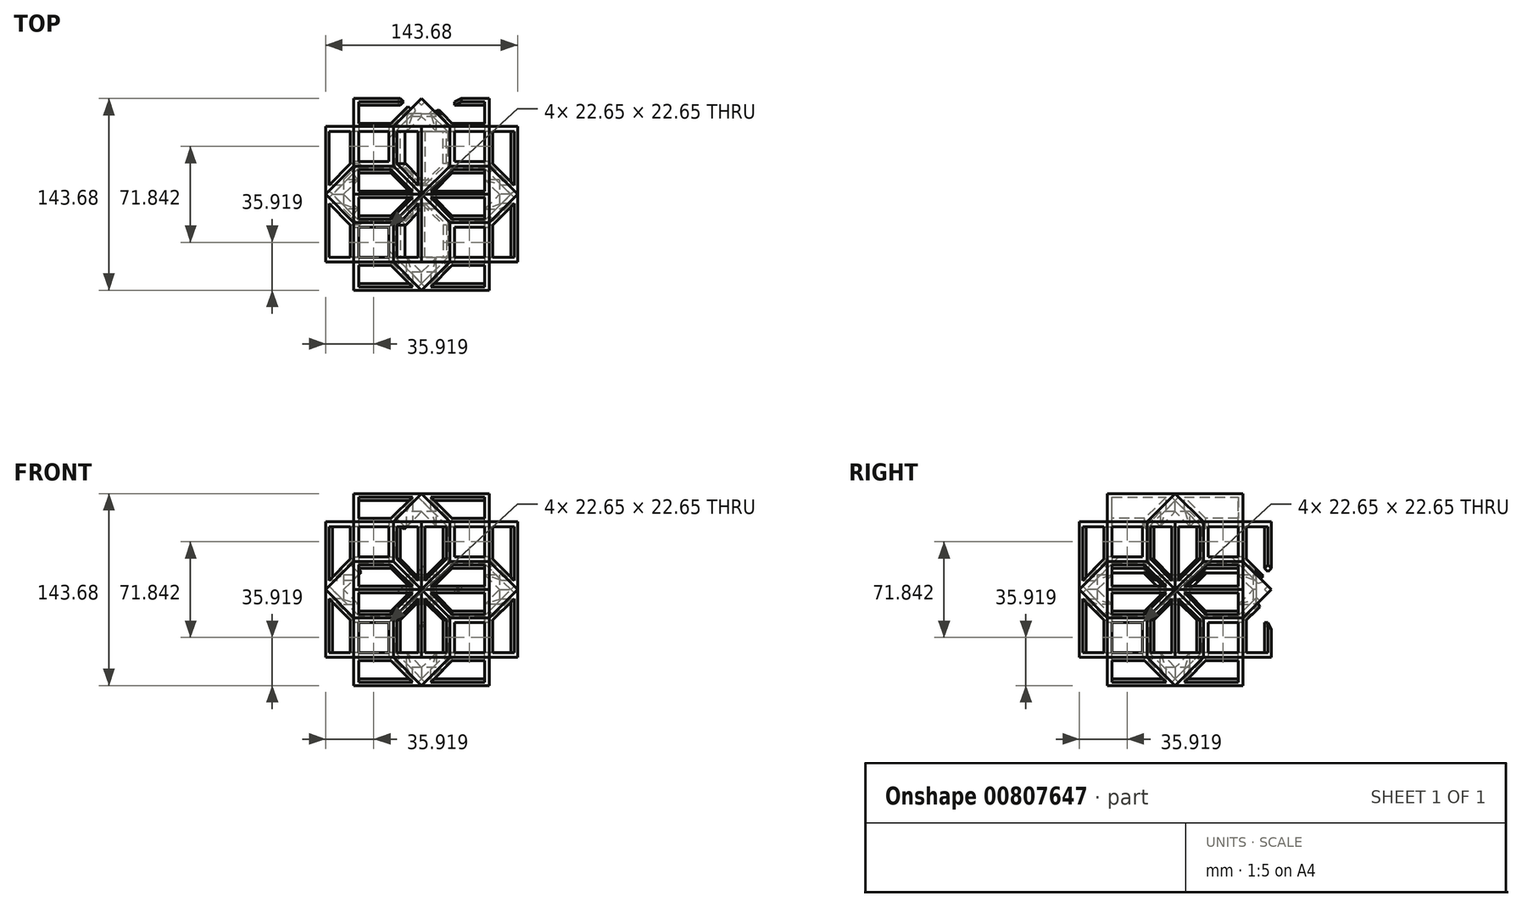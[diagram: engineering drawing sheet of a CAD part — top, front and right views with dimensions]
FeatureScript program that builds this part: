
annotation { "Feature Type Name" : "Feature", "Feature Type Description" : "" }
export const myFeature = defineFeature(function(context is Context, id is Id, definition is map)
    precondition{}
    {
        {
            var Q0;
            Q0=qCreatedBy(makeId("Top.planeOp"),FACE);
            var sketch = newSketch(context, id + "F0", { "sketchPlane" : qUnion([Q0])});
            skLineSegment(sketch, "E0.bottom", {"start": v(50.8, 50.8) * mm, "end": v(-50.8, 50.8) * mm});
            skLineSegment(sketch, "E0.top", {"start": v(50.8, -50.8) * mm, "end": v(-50.8, -50.8) * mm});
            skLineSegment(sketch, "E0.left", {"start": v(50.8, 50.8) * mm, "end": v(50.8, -50.8) * mm});
            skLineSegment(sketch, "E0.right", {"start": v(-50.8, 50.8) * mm, "end": v(-50.8, -50.8) * mm});
            skPoint(sketch, "E0.middle", {"position": v(0, 0) * mm});
            skLineSegment(sketch, "E1", {"start": v(-50.8, 50.8) * mm, "end": v(50.8, -50.8) * mm, "construction": true});
            skLineSegment(sketch, "E2", {"start": v(50.8, 50.8) * mm, "end": v(-50.8, -50.8) * mm, "construction": true});
            skLineSegment(sketch, "E3", {"start": v(0, 0) * mm, "end": v(-50.8, 0) * mm, "construction": true});
            skLineSegment(sketch, "E4", {"start": v(0, 0) * mm, "end": v(0, 50.8) * mm, "construction": true});
            skLineSegment(sketch, "E5.bottom", {"start": v(0, 71.84) * mm, "end": v(71.84, 0) * mm});
            skLineSegment(sketch, "E5.top", {"start": v(-71.84, 0) * mm, "end": v(0, -71.84) * mm});
            skLineSegment(sketch, "E5.left", {"start": v(0, 71.84) * mm, "end": v(-71.84, 0) * mm});
            skLineSegment(sketch, "E5.right", {"start": v(71.84, 0) * mm, "end": v(0, -71.84) * mm});
            skSolve(sketch);
        }
        {
            var Q0;
            {var subQ0=sQuery(id+"F0.wireOp",EDGE,"E0.right");var subQ1=sQuery(id+"F0.wireOp",EDGE,"E0.bottom");var subQ2=makeQuery(id+"F0.imprint","INTERSECT",VERTEX,{"derivedFrom":[subQ1,subQ0]});Q0=makeQuery(id+"F0.imprint","IMPRINT",FACE,{"disambiguationData":[TD([[makeQuery(id+"F0.imprint","IMPRINT",EDGE,{"disambiguationData":[TD([[subQ2,1.0]])],"derivedFrom":subQ1}),1.0]])]});}
            var Q1;
            {var subQ0=sQuery(id+"F0.wireOp",EDGE,"E5.left");var subQ1=sQuery(id+"F0.wireOp",EDGE,"E0.right");var subQ2=makeQuery(id+"F0.imprint","INTERSECT",VERTEX,{"derivedFrom":[subQ1,subQ0]});Q1=makeQuery(id+"F0.imprint","IMPRINT",FACE,{"disambiguationData":[TD([[makeQuery(id+"F0.imprint","IMPRINT",EDGE,{"disambiguationData":[TD([[subQ2,-1.0]])],"derivedFrom":subQ1}),-1.0]])]});}
            var Q2;
            {var subQ0=sQuery(id+"F0.wireOp",EDGE,"E0.right");var subQ1=sQuery(id+"F0.wireOp",EDGE,"E0.top");var subQ2=makeQuery(id+"F0.imprint","INTERSECT",VERTEX,{"derivedFrom":[subQ1,subQ0]});Q2=makeQuery(id+"F0.imprint","IMPRINT",FACE,{"disambiguationData":[TD([[makeQuery(id+"F0.imprint","IMPRINT",EDGE,{"disambiguationData":[TD([[subQ2,1.0]])],"derivedFrom":subQ1}),-1.0]])]});}
            var Q3;
            {var subQ0=sQuery(id+"F0.wireOp",EDGE,"E5.right");var subQ1=sQuery(id+"F0.wireOp",EDGE,"E0.top");var subQ2=makeQuery(id+"F0.imprint","INTERSECT",VERTEX,{"derivedFrom":[subQ1,subQ0]});Q3=makeQuery(id+"F0.imprint","IMPRINT",FACE,{"disambiguationData":[TD([[makeQuery(id+"F0.imprint","IMPRINT",EDGE,{"disambiguationData":[TD([[subQ2,-1.0]])],"derivedFrom":subQ1}),1.0]])]});}
            var Q4;
            {var subQ0=sQuery(id+"F0.wireOp",EDGE,"E0.left");var subQ1=sQuery(id+"F0.wireOp",EDGE,"E0.top");var subQ2=makeQuery(id+"F0.imprint","INTERSECT",VERTEX,{"derivedFrom":[subQ1,subQ0]});Q4=makeQuery(id+"F0.imprint","IMPRINT",FACE,{"disambiguationData":[TD([[makeQuery(id+"F0.imprint","IMPRINT",EDGE,{"disambiguationData":[TD([[subQ2,-1.0]])],"derivedFrom":subQ1}),-1.0]])]});}
            var Q5;
            {var subQ0=sQuery(id+"F0.wireOp",EDGE,"E0.left");var subQ1=sQuery(id+"F0.wireOp",EDGE,"E0.bottom");var subQ2=makeQuery(id+"F0.imprint","INTERSECT",VERTEX,{"derivedFrom":[subQ1,subQ0]});Q5=makeQuery(id+"F0.imprint","IMPRINT",FACE,{"disambiguationData":[TD([[makeQuery(id+"F0.imprint","IMPRINT",EDGE,{"disambiguationData":[TD([[subQ2,-1.0]])],"derivedFrom":subQ1}),1.0]])]});}
            var Q6;
            {var subQ0=sQuery(id+"F0.wireOp",EDGE,"E5.bottom");var subQ1=sQuery(id+"F0.wireOp",EDGE,"E0.left");var subQ2=makeQuery(id+"F0.imprint","INTERSECT",VERTEX,{"derivedFrom":[subQ1,subQ0]});Q6=makeQuery(id+"F0.imprint","IMPRINT",FACE,{"disambiguationData":[TD([[makeQuery(id+"F0.imprint","IMPRINT",EDGE,{"disambiguationData":[TD([[subQ2,-1.0]])],"derivedFrom":subQ1}),1.0]])]});}
            var Q7;
            {var subQ0=sQuery(id+"F0.wireOp",EDGE,"E5.bottom");var subQ1=sQuery(id+"F0.wireOp",EDGE,"E0.bottom");var subQ2=makeQuery(id+"F0.imprint","INTERSECT",VERTEX,{"derivedFrom":[subQ1,subQ0]});Q7=makeQuery(id+"F0.imprint","IMPRINT",FACE,{"disambiguationData":[TD([[makeQuery(id+"F0.imprint","IMPRINT",EDGE,{"disambiguationData":[TD([[subQ2,-1.0]])],"derivedFrom":subQ1}),-1.0]])]});}
            var Q8;
            {var subQ5=sQuery(id+"F0.wireOp",EDGE,"E5.bottom");var subQ13=sQuery(id+"F0.wireOp",EDGE,"E0.bottom");var subQ14=makeQuery(id+"F0.imprint","INTERSECT",VERTEX,{"derivedFrom":[subQ13,subQ5]});Q8=makeQuery(id+"F0.imprint","IMPRINT",FACE,{"disambiguationData":[TD([[makeQuery(id+"F0.imprint","IMPRINT",EDGE,{"disambiguationData":[TD([[subQ14,-1.0]])],"derivedFrom":subQ13}),1.0]])]});}
            extrude(context, id + "F1", {"entities" : qUnion([Q0, Q1, Q2, Q3, Q4, Q5, Q6, Q7, Q8]), "depth" : 101.6 * mm, "offsetDistance" : 25.4 * mm});
        }
        {
            var Q0;
            {var subQ0=sQuery(id+"F0.wireOp",EDGE,"E0.top");Q0=makeQuery(id+"F1.opExtrude","SWEPT_FACE",FACE,{"disambiguationData":[OSD([subQ0]),TDD([makeQuery(id+"F0.imprint","IMPRINT",EDGE,{"disambiguationData":[TD([[makeQuery(id+"F0.imprint","INTERSECT",VERTEX,{"derivedFrom":[subQ0,sQuery(id+"F0.wireOp",EDGE,"E0.right")]}),1.0]])],"derivedFrom":subQ0})])]});}
            var sketch = newSketch(context, id + "F2", { "sketchPlane" : qUnion([Q0])});
            skLineSegment(sketch, "E6.bottom", {"start": v(0, 122.64) * mm, "end": v(71.84, 50.8) * mm});
            skLineSegment(sketch, "E6.top", {"start": v(-71.84, 50.8) * mm, "end": v(0, -21.04) * mm});
            skLineSegment(sketch, "E6.left", {"start": v(0, 122.64) * mm, "end": v(-71.84, 50.8) * mm});
            skLineSegment(sketch, "E6.right", {"start": v(71.84, 50.8) * mm, "end": v(0, -21.04) * mm});
            skLineSegment(sketch, "E7", {"start": v(-50.8, 101.6) * mm, "end": v(50.8, 0) * mm, "construction": true});
            skLineSegment(sketch, "E8", {"start": v(50.8, 101.6) * mm, "end": v(-50.8, 0) * mm, "construction": true});
            skLineSegment(sketch, "E9", {"start": v(0, 50.8) * mm, "end": v(-50.8, 50.8) * mm, "construction": true});
            skLineSegment(sketch, "E10", {"start": v(0, 50.8) * mm, "end": v(0, 101.6) * mm, "construction": true});
            skSolve(sketch);
        }
        {
            var Q0;
            {var subQ6=sQuery(id+"F2.wireOp",EDGE,"E6.bottom");Q0=makeQuery(id+"F2.imprint","IMPRINT",FACE,{"disambiguationData":[TD([[makeQuery(id+"F2.imprint","IMPRINT",EDGE,{"derivedFrom":subQ6}),-1.0]])]});}
            var Q1;
            {var subQ0=sQuery(id+"F2.wireOp",EDGE,"E6.left");var subQ1=sQuery(id+"F2.wireOp",EDGE,"E6.top");var subQ2=makeQuery(id+"F2.imprint","INTERSECT",VERTEX,{"derivedFrom":[subQ1,subQ0]});Q1=makeQuery(id+"F2.imprint","IMPRINT",FACE,{"disambiguationData":[TD([[makeQuery(id+"F2.imprint","IMPRINT",EDGE,{"disambiguationData":[TD([[subQ2,-1.0]])],"derivedFrom":subQ1}),1.0]])]});}
            extrude(context, id + "F3", {"entities" : qUnion([Q0, Q1]), "operationType" : NewBodyOperationType.ADD, "oppositeDirection" : true, "depth" : 101.6 * mm, "offsetDistance" : 25.4 * mm});
        }
        {
            var Q0;
            {var subQ2=sQuery(id+"F0.wireOp",EDGE,"E0.right");var subQ4=sQuery(id+"F2.wireOp",EDGE,"E6.left");var subQ5=sQuery(id+"F2.wireOp",EDGE,"E6.top");var subQ7=sQuery(id+"F0.wireOp",EDGE,"E0.bottom");var subQ8=makeQuery(id+"F0.imprint","INTERSECT",VERTEX,{"derivedFrom":[subQ7,subQ2]});Q0=makeQuery(id+"F3.boolean.opBoolean","SPLIT",FACE,{"disambiguationData":[TD([makeQuery(id+"F3.opExtrude","SWEPT_FACE",FACE,{"disambiguationData":[OSD([subQ5]),TDD([makeQuery(id+"F2.imprint","IMPRINT",EDGE,{"disambiguationData":[TD([[makeQuery(id+"F2.imprint","INTERSECT",VERTEX,{"derivedFrom":[subQ5,subQ4]}),-1.0]])],"derivedFrom":subQ5})])]})])],"derivedFrom":makeQuery(id+"F1.opExtrude","SWEPT_FACE",FACE,{"disambiguationData":[OSD([subQ2]),TDD([makeQuery(id+"F0.imprint","IMPRINT",EDGE,{"disambiguationData":[TD([[subQ8,-1.0]])],"derivedFrom":subQ2})])]})});}
            var sketch = newSketch(context, id + "F4", { "sketchPlane" : qUnion([Q0])});
            skLineSegment(sketch, "E11.bottom", {"start": v(-71.84, 50.8) * mm, "end": v(0, -21.04) * mm});
            skLineSegment(sketch, "E11.top", {"start": v(0, 122.64) * mm, "end": v(71.84, 50.8) * mm});
            skLineSegment(sketch, "E11.left", {"start": v(-71.84, 50.8) * mm, "end": v(0, 122.64) * mm});
            skLineSegment(sketch, "E11.right", {"start": v(0, -21.04) * mm, "end": v(71.84, 50.8) * mm});
            skLineSegment(sketch, "E12", {"start": v(-50.8, 101.6) * mm, "end": v(50.8, 0) * mm, "construction": true});
            skLineSegment(sketch, "E13", {"start": v(50.8, 101.6) * mm, "end": v(-50.8, 0) * mm, "construction": true});
            skLineSegment(sketch, "E14", {"start": v(0, 50.8) * mm, "end": v(-50.8, 50.8) * mm, "construction": true});
            skLineSegment(sketch, "E15", {"start": v(0, 50.8) * mm, "end": v(0, 101.6) * mm, "construction": true});
            skSolve(sketch);
        }
        {
            var Q0;
            Q0=makeQuery(id+"F4.imprint","IMPRINT",FACE,{"disambiguationData":[TD([[makeQuery(id+"F4.imprint","IMPRINT",EDGE,{"derivedFrom":sQuery(id+"F4.wireOp",EDGE,"E11.top")}),-1.0]])]});
            extrude(context, id + "F5", {"entities" : qUnion([Q0]), "operationType" : NewBodyOperationType.ADD, "oppositeDirection" : true, "depth" : 101.6 * mm, "offsetDistance" : 25.4 * mm});
        }
        {
            var Q0;
            {var subQ0=sQuery(id+"F2.wireOp",EDGE,"E6.right");var subQ2=sQuery(id+"F0.wireOp",EDGE,"E0.top");var subQ3=sQuery(id+"F0.wireOp",EDGE,"E0.left");var subQ4=makeQuery(id+"F0.imprint","INTERSECT",VERTEX,{"derivedFrom":[subQ2,subQ3]});Q0=makeQuery(id+"F3.boolean.opBoolean","SPLIT",FACE,{"disambiguationData":[TD([makeQuery(id+"F3.opExtrude","SWEPT_FACE",FACE,{"disambiguationData":[OSD([subQ0])]})])],"derivedFrom":makeQuery(id+"F1.opExtrude","SWEPT_FACE",FACE,{"disambiguationData":[OSD([subQ3]),TDD([makeQuery(id+"F0.imprint","IMPRINT",EDGE,{"disambiguationData":[TD([[subQ4,1.0]])],"derivedFrom":subQ3})])]})});}
            var sketch = newSketch(context, id + "F6", { "sketchPlane" : qUnion([Q0])});
            skLineSegment(sketch, "E16.bottom", {"start": v(-50.8, 29.76) * mm, "end": v(-21.04, 29.76) * mm});
            skLineSegment(sketch, "E16.top", {"start": v(-50.8, 0) * mm, "end": v(-21.04, 0) * mm});
            skLineSegment(sketch, "E16.left", {"start": v(-50.8, 29.76) * mm, "end": v(-50.8, 0) * mm});
            skLineSegment(sketch, "E16.right", {"start": v(-21.04, 29.76) * mm, "end": v(-21.04, 0) * mm});
            skLineSegment(sketch, "E17.0", {"start": v(-24.6, 26.2) * mm, "end": v(-24.6, 3.56) * mm});
            skLineSegment(sketch, "E17.1", {"start": v(-47.24, 26.2) * mm, "end": v(-24.6, 26.2) * mm});
            skLineSegment(sketch, "E17.2", {"start": v(-47.24, 26.2) * mm, "end": v(-47.24, 3.56) * mm});
            skLineSegment(sketch, "E17.3", {"start": v(-47.24, 3.56) * mm, "end": v(-24.6, 3.56) * mm});
            skSolve(sketch);
        }
        {
            var Q0;
            Q0=makeQuery(id+"F6.imprint","IMPRINT",FACE,{"disambiguationData":[TD([[makeQuery(id+"F6.imprint","IMPRINT",EDGE,{"derivedFrom":sQuery(id+"F6.wireOp",EDGE,"E17.0")}),-1.0]])]});
            extrude(context, id + "F7", {"entities" : qUnion([Q0]), "operationType" : NewBodyOperationType.ADD, "oppositeDirection" : true, "depth" : 5.08 * mm, "offsetDistance" : 25.4 * mm});
        }
        {
            var Q0;
            {var subQ2=sQuery(id+"F0.wireOp",EDGE,"E0.right");var subQ4=sQuery(id+"F2.wireOp",EDGE,"E6.left");var subQ5=sQuery(id+"F2.wireOp",EDGE,"E6.top");var subQ7=sQuery(id+"F0.wireOp",EDGE,"E0.bottom");var subQ8=makeQuery(id+"F0.imprint","INTERSECT",VERTEX,{"derivedFrom":[subQ7,subQ2]});Q0=makeQuery(id+"F3.boolean.opBoolean","SPLIT",FACE,{"disambiguationData":[TD([makeQuery(id+"F3.opExtrude","SWEPT_FACE",FACE,{"disambiguationData":[OSD([subQ4]),TDD([makeQuery(id+"F2.imprint","IMPRINT",EDGE,{"disambiguationData":[TD([[makeQuery(id+"F2.imprint","INTERSECT",VERTEX,{"derivedFrom":[subQ5,subQ4]}),1.0]])],"derivedFrom":subQ4})])]})])],"derivedFrom":makeQuery(id+"F1.opExtrude","SWEPT_FACE",FACE,{"disambiguationData":[OSD([subQ2]),TDD([makeQuery(id+"F0.imprint","IMPRINT",EDGE,{"disambiguationData":[TD([[subQ8,-1.0]])],"derivedFrom":subQ2})])]})});}
            var Q1;
            {var subQ0=sQuery(id+"F0.wireOp",EDGE,"E0.right");var subQ1=sQuery(id+"F0.wireOp",EDGE,"E0.top");var subQ2=makeQuery(id+"F0.imprint","INTERSECT",VERTEX,{"derivedFrom":[subQ1,subQ0]});var subQ4=sQuery(id+"F2.wireOp",EDGE,"E6.left");var subQ5=sQuery(id+"F2.wireOp",EDGE,"E6.top");Q1=makeQuery(id+"F3.boolean.opBoolean","SPLIT",FACE,{"disambiguationData":[TD([makeQuery(id+"F3.opExtrude","SWEPT_FACE",FACE,{"disambiguationData":[OSD([subQ4]),TDD([makeQuery(id+"F2.imprint","IMPRINT",EDGE,{"disambiguationData":[TD([[makeQuery(id+"F2.imprint","INTERSECT",VERTEX,{"derivedFrom":[subQ5,subQ4]}),1.0]])],"derivedFrom":subQ4})])]})])],"derivedFrom":makeQuery(id+"F1.opExtrude","SWEPT_FACE",FACE,{"disambiguationData":[OSD([subQ0]),TDD([makeQuery(id+"F0.imprint","IMPRINT",EDGE,{"disambiguationData":[TD([[subQ2,1.0]])],"derivedFrom":subQ0})])]})});}
            var Q2;
            {var subQ0=sQuery(id+"F0.wireOp",EDGE,"E5.left");var subQ1=sQuery(id+"F0.wireOp",EDGE,"E5.top");var subQ2=makeQuery(id+"F0.imprint","INTERSECT",VERTEX,{"derivedFrom":[subQ1,subQ0]});var subQ3=sQuery(id+"F0.wireOp",EDGE,"E0.right");var subQ5=makeQuery(id+"F1.opExtrude","SWEPT_FACE",FACE,{"disambiguationData":[OSD([subQ0]),TDD([makeQuery(id+"F0.imprint","IMPRINT",EDGE,{"disambiguationData":[TD([[subQ2,1.0]])],"derivedFrom":subQ0})])]});var subQ9=sQuery(id+"F0.wireOp",EDGE,"E0.top");var subQ11=sQuery(id+"F0.wireOp",EDGE,"E0.bottom");Q2=makeQuery(id+"F3.boolean.opBoolean","SPLIT",FACE,{"disambiguationData":[TD([makeQuery(id+"F1.opExtrude","CAP_FACE",FACE,{"disambiguationData":[OSD([subQ11,subQ9,sQuery(id+"F0.wireOp",EDGE,"E0.left"),subQ3,sQuery(id+"F0.wireOp",EDGE,"E5.bottom"),subQ1,subQ0,sQuery(id+"F0.wireOp",EDGE,"E5.right")])],"isStart":true})])],"derivedFrom":subQ5});}
            var Q3;
            {var subQ0=sQuery(id+"F0.wireOp",EDGE,"E5.left");var subQ1=sQuery(id+"F0.wireOp",EDGE,"E5.top");var subQ2=makeQuery(id+"F0.imprint","INTERSECT",VERTEX,{"derivedFrom":[subQ1,subQ0]});var subQ3=sQuery(id+"F0.wireOp",EDGE,"E0.right");var subQ7=sQuery(id+"F0.wireOp",EDGE,"E0.top");var subQ10=makeQuery(id+"F1.opExtrude","SWEPT_FACE",FACE,{"disambiguationData":[OSD([subQ1]),TDD([makeQuery(id+"F0.imprint","IMPRINT",EDGE,{"disambiguationData":[TD([[subQ2,-1.0]])],"derivedFrom":subQ1})])]});Q3=makeQuery(id+"F3.boolean.opBoolean","SPLIT",FACE,{"disambiguationData":[TD([makeQuery(id+"F1.opExtrude","CAP_FACE",FACE,{"disambiguationData":[OSD([sQuery(id+"F0.wireOp",EDGE,"E0.bottom"),subQ7,sQuery(id+"F0.wireOp",EDGE,"E0.left"),subQ3,sQuery(id+"F0.wireOp",EDGE,"E5.bottom"),subQ1,subQ0,sQuery(id+"F0.wireOp",EDGE,"E5.right")])],"isStart":false})])],"derivedFrom":subQ10});}
            var Q4;
            {var subQ0=sQuery(id+"F0.wireOp",EDGE,"E5.right");var subQ1=sQuery(id+"F0.wireOp",EDGE,"E5.top");var subQ2=makeQuery(id+"F0.imprint","INTERSECT",VERTEX,{"derivedFrom":[subQ1,subQ0]});var subQ3=sQuery(id+"F0.wireOp",EDGE,"E0.top");var subQ5=sQuery(id+"F2.wireOp",EDGE,"E6.right");var subQ6=sQuery(id+"F2.wireOp",EDGE,"E6.left");var subQ7=sQuery(id+"F2.wireOp",EDGE,"E6.top");var subQ8=sQuery(id+"F0.wireOp",EDGE,"E0.right");var subQ9=makeQuery(id+"F0.imprint","IMPRINT",EDGE,{"disambiguationData":[TD([[makeQuery(id+"F0.imprint","INTERSECT",VERTEX,{"derivedFrom":[subQ3,subQ8]}),1.0]])],"derivedFrom":subQ3});var subQ10=sQuery(id+"F0.wireOp",EDGE,"E0.left");var subQ12=makeQuery(id+"F1.opExtrude","CAP_FACE",FACE,{"disambiguationData":[OSD([sQuery(id+"F0.wireOp",EDGE,"E0.bottom"),subQ3,subQ10,subQ8,sQuery(id+"F0.wireOp",EDGE,"E5.bottom"),subQ1,sQuery(id+"F0.wireOp",EDGE,"E5.left"),subQ0])],"isStart":true});Q4=makeQuery(id+"F3.boolean.opBoolean","SPLIT",FACE,{"disambiguationData":[TD([subQ12,makeQuery(id+"F1.opExtrude","SWEPT_FACE",FACE,{"disambiguationData":[OSD([subQ3]),TDD([makeQuery(id+"F0.imprint","IMPRINT",EDGE,{"disambiguationData":[TD([[makeQuery(id+"F0.imprint","INTERSECT",VERTEX,{"derivedFrom":[subQ3,subQ10]}),-1.0]])],"derivedFrom":subQ3})])]}),makeQuery(id+"F1.opExtrude","SWEPT_FACE",FACE,{"disambiguationData":[OSD([subQ3]),TDD([subQ9])]}),makeQuery(id+"F1.opExtrude","SWEPT_FACE",FACE,{"disambiguationData":[OSD([subQ1]),TDD([makeQuery(id+"F0.imprint","IMPRINT",EDGE,{"disambiguationData":[TD([[subQ2,1.0]])],"derivedFrom":subQ1})])]}),makeQuery(id+"F1.opExtrude","SWEPT_FACE",FACE,{"disambiguationData":[OSD([subQ0]),TDD([makeQuery(id+"F0.imprint","IMPRINT",EDGE,{"disambiguationData":[TD([[subQ2,1.0]])],"derivedFrom":subQ0})])]}),makeQuery(id+"F3.opExtrude","CAP_FACE",FACE,{"disambiguationData":[OSD([subQ3,subQ1,sQuery(id+"F2.wireOp",EDGE,"E6.bottom"),subQ7,subQ6,subQ5])],"isStart":true}),makeQuery(id+"F3.opExtrude","CAP_FACE",FACE,{"disambiguationData":[OSD([subQ3,subQ8,subQ7,subQ6])],"isStart":true}),makeQuery(id+"F3.opExtrude","SWEPT_FACE",FACE,{"disambiguationData":[OSD([subQ7]),TDD([makeQuery(id+"F2.imprint","IMPRINT",EDGE,{"disambiguationData":[TD([[makeQuery(id+"F2.imprint","INTERSECT",VERTEX,{"derivedFrom":[subQ7,subQ5]}),1.0]])],"derivedFrom":subQ7})])]}),makeQuery(id+"F3.opExtrude","SWEPT_FACE",FACE,{"disambiguationData":[OSD([subQ5])]})])],"derivedFrom":subQ12});}
            var Q5;
            {var subQ0=sQuery(id+"F2.wireOp",EDGE,"E6.right");var subQ2=sQuery(id+"F2.wireOp",EDGE,"E6.top");var subQ7=sQuery(id+"F0.wireOp",EDGE,"E0.bottom");var subQ9=sQuery(id+"F0.wireOp",EDGE,"E0.right");var subQ10=makeQuery(id+"F0.imprint","INTERSECT",VERTEX,{"derivedFrom":[subQ7,subQ9]});var subQ13=makeQuery(id+"F3.opExtrude","SWEPT_FACE",FACE,{"disambiguationData":[OSD([subQ2]),TDD([makeQuery(id+"F2.imprint","IMPRINT",EDGE,{"disambiguationData":[TD([[makeQuery(id+"F2.imprint","INTERSECT",VERTEX,{"derivedFrom":[subQ2,subQ0]}),1.0]])],"derivedFrom":subQ2})])]});Q5=makeQuery(id+"F5.boolean.opBoolean","SPLIT",FACE,{"disambiguationData":[TD([makeQuery(id+"F1.opExtrude","SWEPT_FACE",FACE,{"disambiguationData":[OSD([subQ7]),TDD([makeQuery(id+"F0.imprint","IMPRINT",EDGE,{"disambiguationData":[TD([[subQ10,1.0]])],"derivedFrom":subQ7})])]})])],"derivedFrom":subQ13});}
            var Q6;
            {var subQ0=sQuery(id+"F0.wireOp",EDGE,"E0.right");var subQ1=sQuery(id+"F0.wireOp",EDGE,"E0.bottom");var subQ2=sQuery(id+"F0.wireOp",EDGE,"E5.left");var subQ4=sQuery(id+"F0.wireOp",EDGE,"E5.bottom");var subQ5=makeQuery(id+"F0.imprint","INTERSECT",VERTEX,{"derivedFrom":[subQ4,subQ2]});var subQ6=sQuery(id+"F2.wireOp",EDGE,"E6.right");var subQ7=sQuery(id+"F2.wireOp",EDGE,"E6.left");var subQ8=sQuery(id+"F2.wireOp",EDGE,"E6.top");var subQ9=sQuery(id+"F0.wireOp",EDGE,"E5.top");var subQ10=sQuery(id+"F0.wireOp",EDGE,"E0.top");var subQ11=sQuery(id+"F0.wireOp",EDGE,"E0.left");var subQ12=makeQuery(id+"F1.opExtrude","CAP_FACE",FACE,{"disambiguationData":[OSD([subQ1,subQ10,subQ11,subQ0,subQ4,subQ9,subQ2,sQuery(id+"F0.wireOp",EDGE,"E5.right")])],"isStart":true});Q6=makeQuery(id+"F3.boolean.opBoolean","SPLIT",FACE,{"disambiguationData":[TD([makeQuery(id+"F1.opExtrude","SWEPT_FACE",FACE,{"disambiguationData":[OSD([subQ1]),TDD([makeQuery(id+"F0.imprint","IMPRINT",EDGE,{"disambiguationData":[TD([[makeQuery(id+"F0.imprint","INTERSECT",VERTEX,{"derivedFrom":[subQ1,subQ11]}),-1.0]])],"derivedFrom":subQ1})])]}),subQ12,makeQuery(id+"F1.opExtrude","SWEPT_FACE",FACE,{"disambiguationData":[OSD([subQ1]),TDD([makeQuery(id+"F0.imprint","IMPRINT",EDGE,{"disambiguationData":[TD([[makeQuery(id+"F0.imprint","INTERSECT",VERTEX,{"derivedFrom":[subQ1,subQ0]}),1.0]])],"derivedFrom":subQ1})])]}),makeQuery(id+"F1.opExtrude","SWEPT_FACE",FACE,{"disambiguationData":[OSD([subQ4]),TDD([makeQuery(id+"F0.imprint","IMPRINT",EDGE,{"disambiguationData":[TD([[subQ5,-1.0]])],"derivedFrom":subQ4})])]}),makeQuery(id+"F1.opExtrude","SWEPT_FACE",FACE,{"disambiguationData":[OSD([subQ2]),TDD([makeQuery(id+"F0.imprint","IMPRINT",EDGE,{"disambiguationData":[TD([[subQ5,-1.0]])],"derivedFrom":subQ2})])]}),makeQuery(id+"F3.opExtrude","CAP_FACE",FACE,{"disambiguationData":[OSD([subQ10,subQ9,sQuery(id+"F2.wireOp",EDGE,"E6.bottom"),subQ8,subQ7,subQ6])],"isStart":false}),makeQuery(id+"F3.opExtrude","CAP_FACE",FACE,{"disambiguationData":[OSD([subQ10,subQ0,subQ8,subQ7])],"isStart":false}),makeQuery(id+"F3.opExtrude","SWEPT_FACE",FACE,{"disambiguationData":[OSD([subQ8]),TDD([makeQuery(id+"F2.imprint","IMPRINT",EDGE,{"disambiguationData":[TD([[makeQuery(id+"F2.imprint","INTERSECT",VERTEX,{"derivedFrom":[subQ8,subQ6]}),1.0]])],"derivedFrom":subQ8})])]}),makeQuery(id+"F3.opExtrude","SWEPT_FACE",FACE,{"disambiguationData":[OSD([subQ6])]})])],"derivedFrom":subQ12});}
            var Q7;
            {var subQ0=sQuery(id+"F0.wireOp",EDGE,"E5.right");var subQ1=sQuery(id+"F0.wireOp",EDGE,"E5.top");var subQ2=makeQuery(id+"F0.imprint","INTERSECT",VERTEX,{"derivedFrom":[subQ1,subQ0]});var subQ5=sQuery(id+"F2.wireOp",EDGE,"E6.bottom");var subQ7=makeQuery(id+"F1.opExtrude","SWEPT_FACE",FACE,{"disambiguationData":[OSD([subQ0]),TDD([makeQuery(id+"F0.imprint","IMPRINT",EDGE,{"disambiguationData":[TD([[subQ2,1.0]])],"derivedFrom":subQ0})])]});Q7=makeQuery(id+"F5.boolean.opBoolean","SPLIT",FACE,{"disambiguationData":[TD([makeQuery(id+"F3.opExtrude","SWEPT_FACE",FACE,{"disambiguationData":[OSD([subQ5])]})])],"derivedFrom":subQ7});}
            var Q8;
            {var subQ0=sQuery(id+"F2.wireOp",EDGE,"E6.right");var subQ2=sQuery(id+"F2.wireOp",EDGE,"E6.top");var subQ4=sQuery(id+"F0.wireOp",EDGE,"E0.top");var subQ7=sQuery(id+"F0.wireOp",EDGE,"E0.right");var subQ8=makeQuery(id+"F0.imprint","IMPRINT",EDGE,{"disambiguationData":[TD([[makeQuery(id+"F0.imprint","INTERSECT",VERTEX,{"derivedFrom":[subQ4,subQ7]}),1.0]])],"derivedFrom":subQ4});var subQ13=makeQuery(id+"F3.opExtrude","SWEPT_FACE",FACE,{"disambiguationData":[OSD([subQ2]),TDD([makeQuery(id+"F2.imprint","IMPRINT",EDGE,{"disambiguationData":[TD([[makeQuery(id+"F2.imprint","INTERSECT",VERTEX,{"derivedFrom":[subQ2,subQ0]}),1.0]])],"derivedFrom":subQ2})])]});Q8=makeQuery(id+"F5.boolean.opBoolean","SPLIT",FACE,{"disambiguationData":[TD([makeQuery(id+"F1.opExtrude","SWEPT_FACE",FACE,{"disambiguationData":[OSD([subQ4]),TDD([subQ8])]})])],"derivedFrom":subQ13});}
            var Q9;
            {var subQ0=sQuery(id+"F2.wireOp",EDGE,"E6.right");var subQ2=sQuery(id+"F0.wireOp",EDGE,"E0.top");var subQ3=sQuery(id+"F0.wireOp",EDGE,"E0.left");var subQ4=makeQuery(id+"F0.imprint","INTERSECT",VERTEX,{"derivedFrom":[subQ2,subQ3]});Q9=makeQuery(id+"F3.boolean.opBoolean","SPLIT",FACE,{"disambiguationData":[TD([makeQuery(id+"F3.opExtrude","SWEPT_FACE",FACE,{"disambiguationData":[OSD([subQ0])]})])],"derivedFrom":makeQuery(id+"F1.opExtrude","SWEPT_FACE",FACE,{"disambiguationData":[OSD([subQ3]),TDD([makeQuery(id+"F0.imprint","IMPRINT",EDGE,{"disambiguationData":[TD([[subQ4,1.0]])],"derivedFrom":subQ3})])]})});}
            var Q10;
            {var subQ0=sQuery(id+"F0.wireOp",EDGE,"E5.right");var subQ1=sQuery(id+"F0.wireOp",EDGE,"E5.top");var subQ2=makeQuery(id+"F0.imprint","INTERSECT",VERTEX,{"derivedFrom":[subQ1,subQ0]});var subQ5=makeQuery(id+"F1.opExtrude","SWEPT_FACE",FACE,{"disambiguationData":[OSD([subQ1]),TDD([makeQuery(id+"F0.imprint","IMPRINT",EDGE,{"disambiguationData":[TD([[subQ2,1.0]])],"derivedFrom":subQ1})])]});var subQ6=sQuery(id+"F2.wireOp",EDGE,"E6.right");var subQ8=sQuery(id+"F2.wireOp",EDGE,"E6.top");Q10=makeQuery(id+"F5.boolean.opBoolean","SPLIT",FACE,{"disambiguationData":[TD([makeQuery(id+"F3.opExtrude","SWEPT_FACE",FACE,{"disambiguationData":[OSD([subQ8]),TDD([makeQuery(id+"F2.imprint","IMPRINT",EDGE,{"disambiguationData":[TD([[makeQuery(id+"F2.imprint","INTERSECT",VERTEX,{"derivedFrom":[subQ8,subQ6]}),1.0]])],"derivedFrom":subQ8})])]})])],"derivedFrom":subQ5});}
            var Q11;
            {var subQ3=sQuery(id+"F0.wireOp",EDGE,"E0.right");var subQ5=sQuery(id+"F0.wireOp",EDGE,"E0.top");var subQ6=makeQuery(id+"F0.imprint","INTERSECT",VERTEX,{"derivedFrom":[subQ5,subQ3]});var subQ7=sQuery(id+"F2.wireOp",EDGE,"E6.left");var subQ8=sQuery(id+"F2.wireOp",EDGE,"E6.top");var subQ9=makeQuery(id+"F2.imprint","INTERSECT",VERTEX,{"derivedFrom":[subQ8,subQ7]});var subQ11=makeQuery(id+"F3.opExtrude","SWEPT_FACE",FACE,{"disambiguationData":[OSD([subQ7]),TDD([makeQuery(id+"F2.imprint","IMPRINT",EDGE,{"disambiguationData":[TD([[subQ9,1.0]])],"derivedFrom":subQ7})])]});Q11=makeQuery(id+"F3.boolean.opBoolean","SPLIT",FACE,{"disambiguationData":[TD([makeQuery(id+"F1.opExtrude","SWEPT_FACE",FACE,{"disambiguationData":[OSD([subQ5]),TDD([makeQuery(id+"F0.imprint","IMPRINT",EDGE,{"disambiguationData":[TD([[subQ6,1.0]])],"derivedFrom":subQ5})])]})])],"derivedFrom":subQ11});}
            var Q12;
            {var subQ0=sQuery(id+"F0.wireOp",EDGE,"E5.left");var subQ1=sQuery(id+"F0.wireOp",EDGE,"E5.top");var subQ2=makeQuery(id+"F0.imprint","INTERSECT",VERTEX,{"derivedFrom":[subQ1,subQ0]});var subQ3=sQuery(id+"F0.wireOp",EDGE,"E0.right");var subQ7=sQuery(id+"F0.wireOp",EDGE,"E0.top");var subQ10=makeQuery(id+"F1.opExtrude","SWEPT_FACE",FACE,{"disambiguationData":[OSD([subQ1]),TDD([makeQuery(id+"F0.imprint","IMPRINT",EDGE,{"disambiguationData":[TD([[subQ2,-1.0]])],"derivedFrom":subQ1})])]});Q12=makeQuery(id+"F3.boolean.opBoolean","SPLIT",FACE,{"disambiguationData":[TD([makeQuery(id+"F1.opExtrude","CAP_FACE",FACE,{"disambiguationData":[OSD([sQuery(id+"F0.wireOp",EDGE,"E0.bottom"),subQ7,sQuery(id+"F0.wireOp",EDGE,"E0.left"),subQ3,sQuery(id+"F0.wireOp",EDGE,"E5.bottom"),subQ1,subQ0,sQuery(id+"F0.wireOp",EDGE,"E5.right")])],"isStart":true})])],"derivedFrom":subQ10});}
            var Q13;
            {var subQ2=sQuery(id+"F0.wireOp",EDGE,"E0.right");var subQ4=sQuery(id+"F2.wireOp",EDGE,"E6.left");var subQ5=sQuery(id+"F2.wireOp",EDGE,"E6.top");var subQ7=sQuery(id+"F0.wireOp",EDGE,"E0.bottom");var subQ8=makeQuery(id+"F0.imprint","INTERSECT",VERTEX,{"derivedFrom":[subQ7,subQ2]});Q13=makeQuery(id+"F3.boolean.opBoolean","SPLIT",FACE,{"disambiguationData":[TD([makeQuery(id+"F3.opExtrude","SWEPT_FACE",FACE,{"disambiguationData":[OSD([subQ5]),TDD([makeQuery(id+"F2.imprint","IMPRINT",EDGE,{"disambiguationData":[TD([[makeQuery(id+"F2.imprint","INTERSECT",VERTEX,{"derivedFrom":[subQ5,subQ4]}),-1.0]])],"derivedFrom":subQ5})])]})])],"derivedFrom":makeQuery(id+"F1.opExtrude","SWEPT_FACE",FACE,{"disambiguationData":[OSD([subQ2]),TDD([makeQuery(id+"F0.imprint","IMPRINT",EDGE,{"disambiguationData":[TD([[subQ8,-1.0]])],"derivedFrom":subQ2})])]})});}
            var Q14;
            {var subQ3=sQuery(id+"F0.wireOp",EDGE,"E0.right");var subQ5=sQuery(id+"F0.wireOp",EDGE,"E0.top");var subQ6=makeQuery(id+"F0.imprint","INTERSECT",VERTEX,{"derivedFrom":[subQ5,subQ3]});var subQ7=sQuery(id+"F2.wireOp",EDGE,"E6.left");var subQ8=sQuery(id+"F2.wireOp",EDGE,"E6.top");var subQ9=makeQuery(id+"F2.imprint","INTERSECT",VERTEX,{"derivedFrom":[subQ8,subQ7]});var subQ11=makeQuery(id+"F3.opExtrude","SWEPT_FACE",FACE,{"disambiguationData":[OSD([subQ8]),TDD([makeQuery(id+"F2.imprint","IMPRINT",EDGE,{"disambiguationData":[TD([[subQ9,-1.0]])],"derivedFrom":subQ8})])]});Q14=makeQuery(id+"F3.boolean.opBoolean","SPLIT",FACE,{"disambiguationData":[TD([makeQuery(id+"F1.opExtrude","SWEPT_FACE",FACE,{"disambiguationData":[OSD([subQ5]),TDD([makeQuery(id+"F0.imprint","IMPRINT",EDGE,{"disambiguationData":[TD([[subQ6,1.0]])],"derivedFrom":subQ5})])]})])],"derivedFrom":subQ11});}
            var Q15;
            {var subQ1=sQuery(id+"F0.wireOp",EDGE,"E5.top");var subQ3=sQuery(id+"F0.wireOp",EDGE,"E0.top");var subQ5=sQuery(id+"F2.wireOp",EDGE,"E6.right");var subQ6=sQuery(id+"F2.wireOp",EDGE,"E6.left");var subQ7=sQuery(id+"F2.wireOp",EDGE,"E6.top");var subQ8=makeQuery(id+"F3.opExtrude","CAP_FACE",FACE,{"disambiguationData":[OSD([subQ3,subQ1,sQuery(id+"F2.wireOp",EDGE,"E6.bottom"),subQ7,subQ6,subQ5])],"isStart":true});Q15=makeQuery(id+"F3.boolean.opBoolean","SPLIT",FACE,{"disambiguationData":[TD([makeQuery(id+"F3.opExtrude","SWEPT_FACE",FACE,{"disambiguationData":[OSD([subQ5])]})])],"derivedFrom":subQ8});}
            var Q16;
            {var subQ3=sQuery(id+"F0.wireOp",EDGE,"E0.right");var subQ5=sQuery(id+"F2.wireOp",EDGE,"E6.left");var subQ6=sQuery(id+"F2.wireOp",EDGE,"E6.top");var subQ7=makeQuery(id+"F2.imprint","INTERSECT",VERTEX,{"derivedFrom":[subQ6,subQ5]});var subQ10=makeQuery(id+"F3.opExtrude","SWEPT_FACE",FACE,{"disambiguationData":[OSD([subQ6]),TDD([makeQuery(id+"F2.imprint","IMPRINT",EDGE,{"disambiguationData":[TD([[subQ7,-1.0]])],"derivedFrom":subQ6})])]});var subQ11=sQuery(id+"F0.wireOp",EDGE,"E0.bottom");var subQ12=makeQuery(id+"F0.imprint","INTERSECT",VERTEX,{"derivedFrom":[subQ11,subQ3]});Q16=makeQuery(id+"F3.boolean.opBoolean","SPLIT",FACE,{"disambiguationData":[TD([makeQuery(id+"F1.opExtrude","SWEPT_FACE",FACE,{"disambiguationData":[OSD([subQ11]),TDD([makeQuery(id+"F0.imprint","IMPRINT",EDGE,{"disambiguationData":[TD([[subQ12,1.0]])],"derivedFrom":subQ11})])]})])],"derivedFrom":subQ10});}
            var Q17;
            {var subQ0=sQuery(id+"F0.wireOp",EDGE,"E5.left");var subQ1=sQuery(id+"F0.wireOp",EDGE,"E5.top");var subQ2=makeQuery(id+"F0.imprint","INTERSECT",VERTEX,{"derivedFrom":[subQ1,subQ0]});var subQ3=sQuery(id+"F0.wireOp",EDGE,"E0.right");var subQ5=makeQuery(id+"F1.opExtrude","SWEPT_FACE",FACE,{"disambiguationData":[OSD([subQ0]),TDD([makeQuery(id+"F0.imprint","IMPRINT",EDGE,{"disambiguationData":[TD([[subQ2,1.0]])],"derivedFrom":subQ0})])]});var subQ9=sQuery(id+"F0.wireOp",EDGE,"E0.top");var subQ11=sQuery(id+"F0.wireOp",EDGE,"E0.bottom");Q17=makeQuery(id+"F3.boolean.opBoolean","SPLIT",FACE,{"disambiguationData":[TD([makeQuery(id+"F1.opExtrude","CAP_FACE",FACE,{"disambiguationData":[OSD([subQ11,subQ9,sQuery(id+"F0.wireOp",EDGE,"E0.left"),subQ3,sQuery(id+"F0.wireOp",EDGE,"E5.bottom"),subQ1,subQ0,sQuery(id+"F0.wireOp",EDGE,"E5.right")])],"isStart":false})])],"derivedFrom":subQ5});}
            var Q18;
            {var subQ0=sQuery(id+"F0.wireOp",EDGE,"E5.right");var subQ1=sQuery(id+"F0.wireOp",EDGE,"E5.top");var subQ2=makeQuery(id+"F0.imprint","INTERSECT",VERTEX,{"derivedFrom":[subQ1,subQ0]});var subQ5=makeQuery(id+"F1.opExtrude","SWEPT_FACE",FACE,{"disambiguationData":[OSD([subQ1]),TDD([makeQuery(id+"F0.imprint","IMPRINT",EDGE,{"disambiguationData":[TD([[subQ2,1.0]])],"derivedFrom":subQ1})])]});var subQ7=sQuery(id+"F2.wireOp",EDGE,"E6.left");var subQ9=sQuery(id+"F2.wireOp",EDGE,"E6.bottom");Q18=makeQuery(id+"F5.boolean.opBoolean","SPLIT",FACE,{"disambiguationData":[TD([makeQuery(id+"F3.opExtrude","SWEPT_FACE",FACE,{"disambiguationData":[OSD([subQ7]),TDD([makeQuery(id+"F2.imprint","IMPRINT",EDGE,{"disambiguationData":[TD([[makeQuery(id+"F2.imprint","INTERSECT",VERTEX,{"derivedFrom":[subQ9,subQ7]}),-1.0]])],"derivedFrom":subQ7})])]})])],"derivedFrom":subQ5});}
            var Q19;
            {var subQ0=sQuery(id+"F0.wireOp",EDGE,"E5.right");var subQ1=sQuery(id+"F0.wireOp",EDGE,"E5.top");var subQ2=sQuery(id+"F0.wireOp",EDGE,"E0.top");var subQ4=sQuery(id+"F0.wireOp",EDGE,"E5.left");var subQ5=sQuery(id+"F0.wireOp",EDGE,"E0.right");var subQ6=sQuery(id+"F2.wireOp",EDGE,"E6.left");var subQ7=sQuery(id+"F2.wireOp",EDGE,"E6.top");var subQ8=sQuery(id+"F2.wireOp",EDGE,"E6.bottom");var subQ9=makeQuery(id+"F0.imprint","INTERSECT",VERTEX,{"derivedFrom":[subQ2,subQ5]});var subQ10=makeQuery(id+"F0.imprint","IMPRINT",EDGE,{"disambiguationData":[TD([[subQ9,1.0]])],"derivedFrom":subQ2});var subQ11=makeQuery(id+"F1.opExtrude","SWEPT_FACE",FACE,{"disambiguationData":[OSD([subQ2]),TDD([subQ10])]});var subQ12=makeQuery(id+"F3.opExtrude","CAP_FACE",FACE,{"disambiguationData":[OSD([subQ2,subQ5,subQ7,subQ6])],"isStart":true});var subQ13=sQuery(id+"F4.wireOp",EDGE,"E11.top");Q19=makeQuery(id+"F5.boolean.opBoolean","SPLIT",FACE,{"disambiguationData":[TD([makeQuery(id+"F1.opExtrude","CAP_FACE",FACE,{"disambiguationData":[OSD([sQuery(id+"F0.wireOp",EDGE,"E0.bottom"),subQ2,sQuery(id+"F0.wireOp",EDGE,"E0.left"),subQ5,sQuery(id+"F0.wireOp",EDGE,"E5.bottom"),subQ1,subQ4,subQ0])],"isStart":false}),subQ11,makeQuery(id+"F1.opExtrude","SWEPT_FACE",FACE,{"disambiguationData":[OSD([subQ5]),TDD([makeQuery(id+"F0.imprint","IMPRINT",EDGE,{"disambiguationData":[TD([[subQ9,1.0]])],"derivedFrom":subQ5})])]}),makeQuery(id+"F1.opExtrude","SWEPT_FACE",FACE,{"disambiguationData":[OSD([subQ1]),TDD([makeQuery(id+"F0.imprint","IMPRINT",EDGE,{"disambiguationData":[TD([[makeQuery(id+"F0.imprint","INTERSECT",VERTEX,{"derivedFrom":[subQ1,subQ0]}),1.0]])],"derivedFrom":subQ1})])]}),makeQuery(id+"F3.opExtrude","CAP_FACE",FACE,{"disambiguationData":[OSD([subQ2,subQ1,subQ8,subQ7,subQ6,sQuery(id+"F2.wireOp",EDGE,"E6.right")])],"isStart":true}),subQ12,makeQuery(id+"F3.opExtrude","SWEPT_FACE",FACE,{"disambiguationData":[OSD([subQ6]),TDD([makeQuery(id+"F2.imprint","IMPRINT",EDGE,{"disambiguationData":[TD([[makeQuery(id+"F2.imprint","INTERSECT",VERTEX,{"derivedFrom":[subQ8,subQ6]}),-1.0]])],"derivedFrom":subQ6})])]}),makeQuery(id+"F3.opExtrude","SWEPT_FACE",FACE,{"disambiguationData":[OSD([subQ6]),TDD([makeQuery(id+"F2.imprint","IMPRINT",EDGE,{"disambiguationData":[TD([[makeQuery(id+"F2.imprint","INTERSECT",VERTEX,{"derivedFrom":[subQ7,subQ6]}),1.0]])],"derivedFrom":subQ6})])]}),makeQuery(id+"F5.opExtrude","CAP_FACE",FACE,{"disambiguationData":[OSD([subQ2,subQ5,subQ4,subQ7,sQuery(id+"F4.wireOp",EDGE,"E11.bottom"),subQ13,sQuery(id+"F4.wireOp",EDGE,"E11.left"),sQuery(id+"F4.wireOp",EDGE,"E11.right")])],"isStart":true}),makeQuery(id+"F5.opExtrude","SWEPT_FACE",FACE,{"disambiguationData":[OSD([subQ13])]})])],"derivedFrom":makeQuery(id+"F3.boolean.opBoolean","MERGE",FACE,{"derivedFrom":[subQ11,subQ12]})});}
            var Q20;
            {var subQ1=sQuery(id+"F0.wireOp",EDGE,"E5.left");var subQ3=sQuery(id+"F0.wireOp",EDGE,"E5.bottom");var subQ5=sQuery(id+"F0.wireOp",EDGE,"E0.left");var subQ7=sQuery(id+"F0.wireOp",EDGE,"E0.bottom");var subQ10=sQuery(id+"F2.wireOp",EDGE,"E6.right");var subQ16=makeQuery(id+"F1.opExtrude","SWEPT_FACE",FACE,{"disambiguationData":[OSD([subQ3]),TDD([makeQuery(id+"F0.imprint","IMPRINT",EDGE,{"disambiguationData":[TD([[makeQuery(id+"F0.imprint","INTERSECT",VERTEX,{"derivedFrom":[subQ3,subQ1]}),-1.0]])],"derivedFrom":subQ3})])]});var subQ17=makeQuery(id+"F3.opExtrude","SWEPT_FACE",FACE,{"disambiguationData":[OSD([subQ10])]});var subQ18=makeQuery(id+"F1.opExtrude","SWEPT_FACE",FACE,{"disambiguationData":[OSD([subQ7]),TDD([makeQuery(id+"F0.imprint","IMPRINT",EDGE,{"disambiguationData":[TD([[makeQuery(id+"F0.imprint","INTERSECT",VERTEX,{"derivedFrom":[subQ7,subQ5]}),-1.0]])],"derivedFrom":subQ7})])]});Q20=makeQuery(id+"F5.boolean.opBoolean","SPLIT",FACE,{"disambiguationData":[TD([subQ18])],"derivedFrom":makeQuery(id+"F3.boolean.opBoolean","SPLIT",FACE,{"disambiguationData":[TD([subQ16])],"derivedFrom":subQ17})});}
            var Q21;
            {var subQ3=sQuery(id+"F0.wireOp",EDGE,"E0.top");var subQ7=sQuery(id+"F0.wireOp",EDGE,"E0.left");var subQ8=makeQuery(id+"F0.imprint","INTERSECT",VERTEX,{"derivedFrom":[subQ3,subQ7]});var subQ10=sQuery(id+"F4.wireOp",EDGE,"E11.top");var subQ11=makeQuery(id+"F5.opExtrude","SWEPT_FACE",FACE,{"disambiguationData":[OSD([subQ10])]});Q21=makeQuery(id+"F5.boolean.opBoolean","SPLIT",FACE,{"disambiguationData":[TD([makeQuery(id+"F1.opExtrude","SWEPT_FACE",FACE,{"disambiguationData":[OSD([subQ3]),TDD([makeQuery(id+"F0.imprint","IMPRINT",EDGE,{"disambiguationData":[TD([[subQ8,-1.0]])],"derivedFrom":subQ3})])]})])],"derivedFrom":subQ11});}
            var Q22;
            {var subQ0=sQuery(id+"F0.wireOp",EDGE,"E5.left");var subQ1=sQuery(id+"F0.wireOp",EDGE,"E5.top");var subQ2=makeQuery(id+"F0.imprint","INTERSECT",VERTEX,{"derivedFrom":[subQ1,subQ0]});var subQ3=sQuery(id+"F0.wireOp",EDGE,"E0.right");var subQ5=makeQuery(id+"F1.opExtrude","SWEPT_FACE",FACE,{"disambiguationData":[OSD([subQ1]),TDD([makeQuery(id+"F0.imprint","IMPRINT",EDGE,{"disambiguationData":[TD([[subQ2,-1.0]])],"derivedFrom":subQ1})])]});var subQ6=sQuery(id+"F0.wireOp",EDGE,"E5.right");var subQ7=sQuery(id+"F0.wireOp",EDGE,"E5.bottom");var subQ8=sQuery(id+"F0.wireOp",EDGE,"E0.top");var subQ9=sQuery(id+"F0.wireOp",EDGE,"E0.bottom");var subQ10=makeQuery(id+"F1.opExtrude","CAP_FACE",FACE,{"disambiguationData":[OSD([subQ9,subQ8,sQuery(id+"F0.wireOp",EDGE,"E0.left"),subQ3,subQ7,subQ1,subQ0,subQ6])],"isStart":true});var subQ11=sQuery(id+"F4.wireOp",EDGE,"E11.right");var subQ12=makeQuery(id+"F0.imprint","INTERSECT",VERTEX,{"derivedFrom":[subQ8,subQ3]});var subQ13=makeQuery(id+"F1.opExtrude","SWEPT_FACE",FACE,{"disambiguationData":[OSD([subQ3]),TDD([makeQuery(id+"F0.imprint","IMPRINT",EDGE,{"disambiguationData":[TD([[subQ12,1.0]])],"derivedFrom":subQ3})])]});var subQ14=sQuery(id+"F4.wireOp",EDGE,"E11.bottom");var subQ15=sQuery(id+"F2.wireOp",EDGE,"E6.left");var subQ16=sQuery(id+"F2.wireOp",EDGE,"E6.top");var subQ17=makeQuery(id+"F0.imprint","INTERSECT",VERTEX,{"derivedFrom":[subQ9,subQ3]});var subQ19=makeQuery(id+"F0.imprint","IMPRINT",EDGE,{"disambiguationData":[TD([[subQ17,-1.0]])],"derivedFrom":subQ3});var subQ20=makeQuery(id+"F1.opExtrude","SWEPT_FACE",FACE,{"disambiguationData":[OSD([subQ3]),TDD([subQ19])]});var subQ21=makeQuery(id+"F1.opExtrude","SWEPT_FACE",FACE,{"disambiguationData":[OSD([subQ0]),TDD([makeQuery(id+"F0.imprint","IMPRINT",EDGE,{"disambiguationData":[TD([[subQ2,1.0]])],"derivedFrom":subQ0})])]});var subQ22=sQuery(id+"F2.wireOp",EDGE,"E6.right");var subQ23=sQuery(id+"F2.wireOp",EDGE,"E6.bottom");var subQ25=makeQuery(id+"F0.imprint","IMPRINT",EDGE,{"disambiguationData":[TD([[subQ12,1.0]])],"derivedFrom":subQ8});Q22=makeQuery(id+"F5.boolean.opBoolean","SPLIT",FACE,{"disambiguationData":[TD([subQ10,subQ20,subQ13,subQ5,subQ21,makeQuery(id+"F5.opExtrude","CAP_FACE",FACE,{"disambiguationData":[OSD([subQ8,subQ3,subQ0,subQ16,subQ14,sQuery(id+"F4.wireOp",EDGE,"E11.top"),sQuery(id+"F4.wireOp",EDGE,"E11.left"),subQ11])],"isStart":true}),makeQuery(id+"F5.opExtrude","SWEPT_FACE",FACE,{"disambiguationData":[OSD([subQ14]),TDD([makeQuery(id+"F4.imprint","IMPRINT",EDGE,{"disambiguationData":[TD([[makeQuery(id+"F4.imprint","INTERSECT",VERTEX,{"derivedFrom":[subQ14,subQ11]}),1.0]])],"derivedFrom":subQ14})])]}),makeQuery(id+"F5.opExtrude","SWEPT_FACE",FACE,{"disambiguationData":[OSD([subQ11])]})])],"derivedFrom":makeQuery(id+"F3.boolean.opBoolean","SPLIT",FACE,{"disambiguationData":[TD([subQ10,makeQuery(id+"F1.opExtrude","SWEPT_FACE",FACE,{"disambiguationData":[OSD([subQ9]),TDD([makeQuery(id+"F0.imprint","IMPRINT",EDGE,{"disambiguationData":[TD([[subQ17,1.0]])],"derivedFrom":subQ9})])]}),makeQuery(id+"F1.opExtrude","SWEPT_FACE",FACE,{"disambiguationData":[OSD([subQ8]),TDD([subQ25])]}),subQ20,subQ13,subQ5,makeQuery(id+"F1.opExtrude","SWEPT_FACE",FACE,{"disambiguationData":[OSD([subQ1]),TDD([makeQuery(id+"F0.imprint","IMPRINT",EDGE,{"disambiguationData":[TD([[makeQuery(id+"F0.imprint","INTERSECT",VERTEX,{"derivedFrom":[subQ1,subQ6]}),1.0]])],"derivedFrom":subQ1})])]}),makeQuery(id+"F1.opExtrude","SWEPT_FACE",FACE,{"disambiguationData":[OSD([subQ0]),TDD([makeQuery(id+"F0.imprint","IMPRINT",EDGE,{"disambiguationData":[TD([[makeQuery(id+"F0.imprint","INTERSECT",VERTEX,{"derivedFrom":[subQ7,subQ0]}),-1.0]])],"derivedFrom":subQ0})])]}),subQ21,makeQuery(id+"F3.opExtrude","CAP_FACE",FACE,{"disambiguationData":[OSD([subQ8,subQ1,subQ23,subQ16,subQ15,subQ22])],"isStart":true}),makeQuery(id+"F3.opExtrude","CAP_FACE",FACE,{"disambiguationData":[OSD([subQ8,subQ1,subQ23,subQ16,subQ15,subQ22])],"isStart":false}),makeQuery(id+"F3.opExtrude","CAP_FACE",FACE,{"disambiguationData":[OSD([subQ8,subQ3,subQ16,subQ15])],"isStart":true}),makeQuery(id+"F3.opExtrude","CAP_FACE",FACE,{"disambiguationData":[OSD([subQ8,subQ3,subQ16,subQ15])],"isStart":false}),makeQuery(id+"F3.opExtrude","SWEPT_FACE",FACE,{"disambiguationData":[OSD([subQ16]),TDD([makeQuery(id+"F2.imprint","IMPRINT",EDGE,{"disambiguationData":[TD([[makeQuery(id+"F2.imprint","INTERSECT",VERTEX,{"derivedFrom":[subQ16,subQ22]}),1.0]])],"derivedFrom":subQ16})])]})])],"derivedFrom":subQ10})});}
            var Q23;
            {var subQ3=sQuery(id+"F0.wireOp",EDGE,"E0.bottom");var subQ5=sQuery(id+"F0.wireOp",EDGE,"E0.right");var subQ6=makeQuery(id+"F0.imprint","INTERSECT",VERTEX,{"derivedFrom":[subQ3,subQ5]});var subQ7=makeQuery(id+"F1.opExtrude","SWEPT_FACE",FACE,{"disambiguationData":[OSD([subQ3]),TDD([makeQuery(id+"F0.imprint","IMPRINT",EDGE,{"disambiguationData":[TD([[subQ6,1.0]])],"derivedFrom":subQ3})])]});var subQ14=sQuery(id+"F4.wireOp",EDGE,"E11.bottom");var subQ15=sQuery(id+"F4.wireOp",EDGE,"E11.left");var subQ16=makeQuery(id+"F5.opExtrude","SWEPT_FACE",FACE,{"disambiguationData":[OSD([subQ14]),TDD([makeQuery(id+"F4.imprint","IMPRINT",EDGE,{"disambiguationData":[TD([[makeQuery(id+"F4.imprint","INTERSECT",VERTEX,{"derivedFrom":[subQ14,subQ15]}),-1.0]])],"derivedFrom":subQ14})])]});Q23=makeQuery(id+"F5.boolean.opBoolean","SPLIT",FACE,{"disambiguationData":[TD([subQ7])],"derivedFrom":subQ16});}
            var Q24;
            {var subQ0=sQuery(id+"F0.wireOp",EDGE,"E5.left");var subQ1=sQuery(id+"F0.wireOp",EDGE,"E5.top");var subQ2=makeQuery(id+"F0.imprint","INTERSECT",VERTEX,{"derivedFrom":[subQ1,subQ0]});var subQ3=sQuery(id+"F0.wireOp",EDGE,"E0.right");var subQ5=makeQuery(id+"F1.opExtrude","SWEPT_FACE",FACE,{"disambiguationData":[OSD([subQ1]),TDD([makeQuery(id+"F0.imprint","IMPRINT",EDGE,{"disambiguationData":[TD([[subQ2,-1.0]])],"derivedFrom":subQ1})])]});var subQ6=sQuery(id+"F0.wireOp",EDGE,"E5.right");var subQ7=sQuery(id+"F0.wireOp",EDGE,"E5.bottom");var subQ8=sQuery(id+"F0.wireOp",EDGE,"E0.top");var subQ9=sQuery(id+"F0.wireOp",EDGE,"E0.bottom");var subQ10=makeQuery(id+"F1.opExtrude","CAP_FACE",FACE,{"disambiguationData":[OSD([subQ9,subQ8,sQuery(id+"F0.wireOp",EDGE,"E0.left"),subQ3,subQ7,subQ1,subQ0,subQ6])],"isStart":true});var subQ11=sQuery(id+"F4.wireOp",EDGE,"E11.right");var subQ12=makeQuery(id+"F0.imprint","INTERSECT",VERTEX,{"derivedFrom":[subQ8,subQ3]});var subQ13=makeQuery(id+"F1.opExtrude","SWEPT_FACE",FACE,{"disambiguationData":[OSD([subQ3]),TDD([makeQuery(id+"F0.imprint","IMPRINT",EDGE,{"disambiguationData":[TD([[subQ12,1.0]])],"derivedFrom":subQ3})])]});var subQ15=makeQuery(id+"F0.imprint","IMPRINT",EDGE,{"disambiguationData":[TD([[subQ12,1.0]])],"derivedFrom":subQ8});var subQ16=makeQuery(id+"F1.opExtrude","SWEPT_FACE",FACE,{"disambiguationData":[OSD([subQ8]),TDD([subQ15])]});var subQ17=sQuery(id+"F2.wireOp",EDGE,"E6.left");var subQ18=sQuery(id+"F2.wireOp",EDGE,"E6.top");var subQ19=makeQuery(id+"F3.opExtrude","CAP_FACE",FACE,{"disambiguationData":[OSD([subQ8,subQ3,subQ18,subQ17])],"isStart":true});var subQ20=makeQuery(id+"F1.opExtrude","SWEPT_FACE",FACE,{"disambiguationData":[OSD([subQ1]),TDD([makeQuery(id+"F0.imprint","IMPRINT",EDGE,{"disambiguationData":[TD([[makeQuery(id+"F0.imprint","INTERSECT",VERTEX,{"derivedFrom":[subQ1,subQ6]}),1.0]])],"derivedFrom":subQ1})])]});var subQ21=sQuery(id+"F2.wireOp",EDGE,"E6.right");var subQ22=sQuery(id+"F2.wireOp",EDGE,"E6.bottom");var subQ23=makeQuery(id+"F3.opExtrude","CAP_FACE",FACE,{"disambiguationData":[OSD([subQ8,subQ1,subQ22,subQ18,subQ17,subQ21])],"isStart":true});var subQ24=makeQuery(id+"F3.opExtrude","SWEPT_FACE",FACE,{"disambiguationData":[OSD([subQ18]),TDD([makeQuery(id+"F2.imprint","IMPRINT",EDGE,{"disambiguationData":[TD([[makeQuery(id+"F2.imprint","INTERSECT",VERTEX,{"derivedFrom":[subQ18,subQ21]}),1.0]])],"derivedFrom":subQ18})])]});var subQ27=makeQuery(id+"F0.imprint","INTERSECT",VERTEX,{"derivedFrom":[subQ9,subQ3]});Q24=makeQuery(id+"F5.boolean.opBoolean","SPLIT",FACE,{"disambiguationData":[TD([subQ10,subQ16,subQ13,subQ5,subQ20,subQ23,subQ19,subQ24,makeQuery(id+"F5.opExtrude","CAP_FACE",FACE,{"disambiguationData":[OSD([subQ8,subQ3,subQ0,subQ18,sQuery(id+"F4.wireOp",EDGE,"E11.bottom"),sQuery(id+"F4.wireOp",EDGE,"E11.top"),sQuery(id+"F4.wireOp",EDGE,"E11.left"),subQ11])],"isStart":true}),makeQuery(id+"F5.opExtrude","SWEPT_FACE",FACE,{"disambiguationData":[OSD([subQ11])]})])],"derivedFrom":makeQuery(id+"F3.boolean.opBoolean","SPLIT",FACE,{"disambiguationData":[TD([subQ10,makeQuery(id+"F1.opExtrude","SWEPT_FACE",FACE,{"disambiguationData":[OSD([subQ9]),TDD([makeQuery(id+"F0.imprint","IMPRINT",EDGE,{"disambiguationData":[TD([[subQ27,1.0]])],"derivedFrom":subQ9})])]}),subQ16,makeQuery(id+"F1.opExtrude","SWEPT_FACE",FACE,{"disambiguationData":[OSD([subQ3]),TDD([makeQuery(id+"F0.imprint","IMPRINT",EDGE,{"disambiguationData":[TD([[subQ27,-1.0]])],"derivedFrom":subQ3})])]}),subQ13,subQ5,subQ20,makeQuery(id+"F1.opExtrude","SWEPT_FACE",FACE,{"disambiguationData":[OSD([subQ0]),TDD([makeQuery(id+"F0.imprint","IMPRINT",EDGE,{"disambiguationData":[TD([[makeQuery(id+"F0.imprint","INTERSECT",VERTEX,{"derivedFrom":[subQ7,subQ0]}),-1.0]])],"derivedFrom":subQ0})])]}),makeQuery(id+"F1.opExtrude","SWEPT_FACE",FACE,{"disambiguationData":[OSD([subQ0]),TDD([makeQuery(id+"F0.imprint","IMPRINT",EDGE,{"disambiguationData":[TD([[subQ2,1.0]])],"derivedFrom":subQ0})])]}),subQ23,makeQuery(id+"F3.opExtrude","CAP_FACE",FACE,{"disambiguationData":[OSD([subQ8,subQ1,subQ22,subQ18,subQ17,subQ21])],"isStart":false}),subQ19,makeQuery(id+"F3.opExtrude","CAP_FACE",FACE,{"disambiguationData":[OSD([subQ8,subQ3,subQ18,subQ17])],"isStart":false}),subQ24])],"derivedFrom":subQ10})});}
            var Q25;
            {var subQ1=sQuery(id+"F2.wireOp",EDGE,"E6.top");var subQ3=sQuery(id+"F0.wireOp",EDGE,"E0.right");var subQ4=sQuery(id+"F0.wireOp",EDGE,"E0.top");var subQ8=sQuery(id+"F4.wireOp",EDGE,"E11.bottom");var subQ9=sQuery(id+"F0.wireOp",EDGE,"E0.bottom");var subQ10=makeQuery(id+"F0.imprint","INTERSECT",VERTEX,{"derivedFrom":[subQ9,subQ3]});var subQ11=sQuery(id+"F0.wireOp",EDGE,"E5.left");var subQ13=makeQuery(id+"F1.opExtrude","SWEPT_FACE",FACE,{"disambiguationData":[OSD([subQ9]),TDD([makeQuery(id+"F0.imprint","IMPRINT",EDGE,{"disambiguationData":[TD([[subQ10,1.0]])],"derivedFrom":subQ9})])]});var subQ14=sQuery(id+"F4.wireOp",EDGE,"E11.left");Q25=makeQuery(id+"F5.boolean.opBoolean","SPLIT",FACE,{"disambiguationData":[TD([subQ13])],"derivedFrom":makeQuery(id+"F5.opExtrude","CAP_FACE",FACE,{"disambiguationData":[OSD([subQ4,subQ3,subQ11,subQ1,subQ8,sQuery(id+"F4.wireOp",EDGE,"E11.top"),subQ14,sQuery(id+"F4.wireOp",EDGE,"E11.right")])],"isStart":true})});}
            var Q26;
            {var subQ0=sQuery(id+"F0.wireOp",EDGE,"E0.left");var subQ1=sQuery(id+"F0.wireOp",EDGE,"E0.top");var subQ2=makeQuery(id+"F0.imprint","INTERSECT",VERTEX,{"derivedFrom":[subQ1,subQ0]});var subQ3=sQuery(id+"F0.wireOp",EDGE,"E5.right");var subQ5=makeQuery(id+"F1.opExtrude","SWEPT_FACE",FACE,{"disambiguationData":[OSD([subQ0]),TDD([makeQuery(id+"F0.imprint","IMPRINT",EDGE,{"disambiguationData":[TD([[subQ2,1.0]])],"derivedFrom":subQ0})])]});var subQ6=sQuery(id+"F0.wireOp",EDGE,"E5.bottom");var subQ7=makeQuery(id+"F0.imprint","INTERSECT",VERTEX,{"derivedFrom":[subQ6,subQ3]});var subQ9=makeQuery(id+"F1.opExtrude","SWEPT_FACE",FACE,{"disambiguationData":[OSD([subQ6]),TDD([makeQuery(id+"F0.imprint","IMPRINT",EDGE,{"disambiguationData":[TD([[subQ7,1.0]])],"derivedFrom":subQ6})])]});var subQ10=sQuery(id+"F0.wireOp",EDGE,"E0.bottom");var subQ11=makeQuery(id+"F0.imprint","INTERSECT",VERTEX,{"derivedFrom":[subQ10,subQ0]});var subQ12=makeQuery(id+"F1.opExtrude","SWEPT_FACE",FACE,{"disambiguationData":[OSD([subQ0]),TDD([makeQuery(id+"F0.imprint","IMPRINT",EDGE,{"disambiguationData":[TD([[subQ11,-1.0]])],"derivedFrom":subQ0})])]});var subQ13=sQuery(id+"F0.wireOp",EDGE,"E5.left");var subQ14=sQuery(id+"F0.wireOp",EDGE,"E5.top");var subQ15=sQuery(id+"F0.wireOp",EDGE,"E0.right");var subQ16=makeQuery(id+"F1.opExtrude","CAP_FACE",FACE,{"disambiguationData":[OSD([subQ10,subQ1,subQ0,subQ15,subQ6,subQ14,subQ13,subQ3])],"isStart":true});var subQ17=sQuery(id+"F4.wireOp",EDGE,"E11.right");var subQ18=makeQuery(id+"F1.opExtrude","SWEPT_FACE",FACE,{"disambiguationData":[OSD([subQ3]),TDD([makeQuery(id+"F0.imprint","IMPRINT",EDGE,{"disambiguationData":[TD([[subQ7,-1.0]])],"derivedFrom":subQ3})])]});var subQ19=sQuery(id+"F4.wireOp",EDGE,"E11.bottom");var subQ20=sQuery(id+"F2.wireOp",EDGE,"E6.top");var subQ21=sQuery(id+"F2.wireOp",EDGE,"E6.left");var subQ24=sQuery(id+"F2.wireOp",EDGE,"E6.right");var subQ25=sQuery(id+"F2.wireOp",EDGE,"E6.bottom");Q26=makeQuery(id+"F5.boolean.opBoolean","SPLIT",FACE,{"disambiguationData":[TD([subQ16,subQ12,subQ5,subQ9,subQ18,makeQuery(id+"F5.opExtrude","CAP_FACE",FACE,{"disambiguationData":[OSD([subQ1,subQ15,subQ13,subQ20,subQ19,sQuery(id+"F4.wireOp",EDGE,"E11.top"),sQuery(id+"F4.wireOp",EDGE,"E11.left"),subQ17])],"isStart":false}),makeQuery(id+"F5.opExtrude","SWEPT_FACE",FACE,{"disambiguationData":[OSD([subQ19]),TDD([makeQuery(id+"F4.imprint","IMPRINT",EDGE,{"disambiguationData":[TD([[makeQuery(id+"F4.imprint","INTERSECT",VERTEX,{"derivedFrom":[subQ19,subQ17]}),1.0]])],"derivedFrom":subQ19})])]}),makeQuery(id+"F5.opExtrude","SWEPT_FACE",FACE,{"disambiguationData":[OSD([subQ17])]})])],"derivedFrom":makeQuery(id+"F3.boolean.opBoolean","SPLIT",FACE,{"disambiguationData":[TD([makeQuery(id+"F1.opExtrude","SWEPT_FACE",FACE,{"disambiguationData":[OSD([subQ10]),TDD([makeQuery(id+"F0.imprint","IMPRINT",EDGE,{"disambiguationData":[TD([[subQ11,-1.0]])],"derivedFrom":subQ10})])]}),subQ16,makeQuery(id+"F1.opExtrude","SWEPT_FACE",FACE,{"disambiguationData":[OSD([subQ1]),TDD([makeQuery(id+"F0.imprint","IMPRINT",EDGE,{"disambiguationData":[TD([[subQ2,-1.0]])],"derivedFrom":subQ1})])]}),subQ12,subQ5,makeQuery(id+"F1.opExtrude","SWEPT_FACE",FACE,{"disambiguationData":[OSD([subQ6]),TDD([makeQuery(id+"F0.imprint","IMPRINT",EDGE,{"disambiguationData":[TD([[makeQuery(id+"F0.imprint","INTERSECT",VERTEX,{"derivedFrom":[subQ6,subQ13]}),-1.0]])],"derivedFrom":subQ6})])]}),subQ9,subQ18,makeQuery(id+"F1.opExtrude","SWEPT_FACE",FACE,{"disambiguationData":[OSD([subQ3]),TDD([makeQuery(id+"F0.imprint","IMPRINT",EDGE,{"disambiguationData":[TD([[makeQuery(id+"F0.imprint","INTERSECT",VERTEX,{"derivedFrom":[subQ14,subQ3]}),1.0]])],"derivedFrom":subQ3})])]}),makeQuery(id+"F3.opExtrude","CAP_FACE",FACE,{"disambiguationData":[OSD([subQ1,subQ14,subQ25,subQ20,subQ21,subQ24])],"isStart":true}),makeQuery(id+"F3.opExtrude","CAP_FACE",FACE,{"disambiguationData":[OSD([subQ1,subQ14,subQ25,subQ20,subQ21,subQ24])],"isStart":false}),makeQuery(id+"F3.opExtrude","SWEPT_FACE",FACE,{"disambiguationData":[OSD([subQ24])]})])],"derivedFrom":subQ16})});}
            var Q27;
            {var subQ0=sQuery(id+"F0.wireOp",EDGE,"E5.left");var subQ3=sQuery(id+"F0.wireOp",EDGE,"E0.right");var subQ5=sQuery(id+"F0.wireOp",EDGE,"E0.top");var subQ8=sQuery(id+"F4.wireOp",EDGE,"E11.right");var subQ9=sQuery(id+"F4.wireOp",EDGE,"E11.bottom");var subQ10=sQuery(id+"F2.wireOp",EDGE,"E6.top");Q27=makeQuery(id+"F5.boolean.opBoolean","SPLIT",FACE,{"disambiguationData":[TD([makeQuery(id+"F5.opExtrude","SWEPT_FACE",FACE,{"disambiguationData":[OSD([subQ9]),TDD([makeQuery(id+"F4.imprint","IMPRINT",EDGE,{"disambiguationData":[TD([[makeQuery(id+"F4.imprint","INTERSECT",VERTEX,{"derivedFrom":[subQ9,subQ8]}),1.0]])],"derivedFrom":subQ9})])]})])],"derivedFrom":makeQuery(id+"F5.opExtrude","CAP_FACE",FACE,{"disambiguationData":[OSD([subQ5,subQ3,subQ0,subQ10,subQ9,sQuery(id+"F4.wireOp",EDGE,"E11.top"),sQuery(id+"F4.wireOp",EDGE,"E11.left"),subQ8])],"isStart":true})});}
            var Q28;
            {var subQ0=sQuery(id+"F0.wireOp",EDGE,"E0.left");var subQ1=sQuery(id+"F0.wireOp",EDGE,"E0.bottom");var subQ2=makeQuery(id+"F0.imprint","INTERSECT",VERTEX,{"derivedFrom":[subQ1,subQ0]});var subQ3=sQuery(id+"F0.wireOp",EDGE,"E5.bottom");var subQ5=makeQuery(id+"F1.opExtrude","SWEPT_FACE",FACE,{"disambiguationData":[OSD([subQ0]),TDD([makeQuery(id+"F0.imprint","IMPRINT",EDGE,{"disambiguationData":[TD([[subQ2,-1.0]])],"derivedFrom":subQ0})])]});var subQ6=sQuery(id+"F0.wireOp",EDGE,"E5.right");var subQ7=sQuery(id+"F0.wireOp",EDGE,"E5.left");var subQ8=sQuery(id+"F0.wireOp",EDGE,"E5.top");var subQ9=sQuery(id+"F0.wireOp",EDGE,"E0.right");var subQ10=sQuery(id+"F0.wireOp",EDGE,"E0.top");var subQ11=makeQuery(id+"F1.opExtrude","CAP_FACE",FACE,{"disambiguationData":[OSD([subQ1,subQ10,subQ0,subQ9,subQ3,subQ8,subQ7,subQ6])],"isStart":true});var subQ13=makeQuery(id+"F1.opExtrude","SWEPT_FACE",FACE,{"disambiguationData":[OSD([subQ3]),TDD([makeQuery(id+"F0.imprint","IMPRINT",EDGE,{"disambiguationData":[TD([[makeQuery(id+"F0.imprint","INTERSECT",VERTEX,{"derivedFrom":[subQ3,subQ7]}),-1.0]])],"derivedFrom":subQ3})])]});var subQ14=sQuery(id+"F2.wireOp",EDGE,"E6.right");var subQ15=makeQuery(id+"F3.opExtrude","SWEPT_FACE",FACE,{"disambiguationData":[OSD([subQ14])]});var subQ16=makeQuery(id+"F1.opExtrude","SWEPT_FACE",FACE,{"disambiguationData":[OSD([subQ1]),TDD([makeQuery(id+"F0.imprint","IMPRINT",EDGE,{"disambiguationData":[TD([[subQ2,-1.0]])],"derivedFrom":subQ1})])]});var subQ17=makeQuery(id+"F0.imprint","INTERSECT",VERTEX,{"derivedFrom":[subQ3,subQ6]});var subQ18=makeQuery(id+"F1.opExtrude","SWEPT_FACE",FACE,{"disambiguationData":[OSD([subQ3]),TDD([makeQuery(id+"F0.imprint","IMPRINT",EDGE,{"disambiguationData":[TD([[subQ17,1.0]])],"derivedFrom":subQ3})])]});var subQ19=sQuery(id+"F2.wireOp",EDGE,"E6.left");var subQ20=sQuery(id+"F2.wireOp",EDGE,"E6.top");var subQ21=sQuery(id+"F2.wireOp",EDGE,"E6.bottom");var subQ22=makeQuery(id+"F3.opExtrude","CAP_FACE",FACE,{"disambiguationData":[OSD([subQ10,subQ8,subQ21,subQ20,subQ19,subQ14])],"isStart":false});var subQ23=sQuery(id+"F4.wireOp",EDGE,"E11.right");var subQ24=sQuery(id+"F4.wireOp",EDGE,"E11.bottom");var subQ28=makeQuery(id+"F0.imprint","INTERSECT",VERTEX,{"derivedFrom":[subQ10,subQ0]});Q28=makeQuery(id+"F5.boolean.opBoolean","SPLIT",FACE,{"disambiguationData":[TD([subQ16,subQ11,subQ5,subQ13,subQ18,subQ22,subQ15,makeQuery(id+"F5.opExtrude","CAP_FACE",FACE,{"disambiguationData":[OSD([subQ10,subQ9,subQ7,subQ20,subQ24,sQuery(id+"F4.wireOp",EDGE,"E11.top"),sQuery(id+"F4.wireOp",EDGE,"E11.left"),subQ23])],"isStart":false}),makeQuery(id+"F5.opExtrude","SWEPT_FACE",FACE,{"disambiguationData":[OSD([subQ24]),TDD([makeQuery(id+"F4.imprint","IMPRINT",EDGE,{"disambiguationData":[TD([[makeQuery(id+"F4.imprint","INTERSECT",VERTEX,{"derivedFrom":[subQ24,subQ23]}),1.0]])],"derivedFrom":subQ24})])]})])],"derivedFrom":makeQuery(id+"F3.boolean.opBoolean","SPLIT",FACE,{"disambiguationData":[TD([subQ16,subQ11,makeQuery(id+"F1.opExtrude","SWEPT_FACE",FACE,{"disambiguationData":[OSD([subQ10]),TDD([makeQuery(id+"F0.imprint","IMPRINT",EDGE,{"disambiguationData":[TD([[subQ28,-1.0]])],"derivedFrom":subQ10})])]}),subQ5,makeQuery(id+"F1.opExtrude","SWEPT_FACE",FACE,{"disambiguationData":[OSD([subQ0]),TDD([makeQuery(id+"F0.imprint","IMPRINT",EDGE,{"disambiguationData":[TD([[subQ28,1.0]])],"derivedFrom":subQ0})])]}),subQ13,subQ18,makeQuery(id+"F1.opExtrude","SWEPT_FACE",FACE,{"disambiguationData":[OSD([subQ6]),TDD([makeQuery(id+"F0.imprint","IMPRINT",EDGE,{"disambiguationData":[TD([[subQ17,-1.0]])],"derivedFrom":subQ6})])]}),makeQuery(id+"F1.opExtrude","SWEPT_FACE",FACE,{"disambiguationData":[OSD([subQ6]),TDD([makeQuery(id+"F0.imprint","IMPRINT",EDGE,{"disambiguationData":[TD([[makeQuery(id+"F0.imprint","INTERSECT",VERTEX,{"derivedFrom":[subQ8,subQ6]}),1.0]])],"derivedFrom":subQ6})])]}),makeQuery(id+"F3.opExtrude","CAP_FACE",FACE,{"disambiguationData":[OSD([subQ10,subQ8,subQ21,subQ20,subQ19,subQ14])],"isStart":true}),subQ22,subQ15])],"derivedFrom":subQ11})});}
            var Q29;
            {var subQ6=sQuery(id+"F0.wireOp",EDGE,"E5.right");var subQ8=sQuery(id+"F0.wireOp",EDGE,"E5.bottom");var subQ12=sQuery(id+"F4.wireOp",EDGE,"E11.right");var subQ13=makeQuery(id+"F5.opExtrude","SWEPT_FACE",FACE,{"disambiguationData":[OSD([subQ12])]});Q29=makeQuery(id+"F5.boolean.opBoolean","SPLIT",FACE,{"disambiguationData":[TD([makeQuery(id+"F1.opExtrude","SWEPT_FACE",FACE,{"disambiguationData":[OSD([subQ6]),TDD([makeQuery(id+"F0.imprint","IMPRINT",EDGE,{"disambiguationData":[TD([[makeQuery(id+"F0.imprint","INTERSECT",VERTEX,{"derivedFrom":[subQ8,subQ6]}),-1.0]])],"derivedFrom":subQ6})])]})])],"derivedFrom":subQ13});}
            var Q30;
            {var subQ0=sQuery(id+"F0.wireOp",EDGE,"E0.left");var subQ1=sQuery(id+"F0.wireOp",EDGE,"E0.bottom");var subQ2=makeQuery(id+"F0.imprint","INTERSECT",VERTEX,{"derivedFrom":[subQ1,subQ0]});var subQ3=sQuery(id+"F0.wireOp",EDGE,"E5.bottom");var subQ4=sQuery(id+"F4.wireOp",EDGE,"E11.bottom");var subQ5=sQuery(id+"F0.wireOp",EDGE,"E0.right");var subQ7=sQuery(id+"F0.wireOp",EDGE,"E5.left");var subQ9=sQuery(id+"F2.wireOp",EDGE,"E6.left");var subQ10=sQuery(id+"F2.wireOp",EDGE,"E6.top");var subQ11=sQuery(id+"F0.wireOp",EDGE,"E0.top");var subQ13=sQuery(id+"F0.wireOp",EDGE,"E5.top");var subQ14=makeQuery(id+"F1.opExtrude","CAP_FACE",FACE,{"disambiguationData":[OSD([subQ1,subQ11,subQ0,subQ5,subQ3,subQ13,subQ7,sQuery(id+"F0.wireOp",EDGE,"E5.right")])],"isStart":true});var subQ15=sQuery(id+"F4.wireOp",EDGE,"E11.left");var subQ17=sQuery(id+"F2.wireOp",EDGE,"E6.right");var subQ18=makeQuery(id+"F1.opExtrude","SWEPT_FACE",FACE,{"disambiguationData":[OSD([subQ1]),TDD([makeQuery(id+"F0.imprint","IMPRINT",EDGE,{"disambiguationData":[TD([[subQ2,-1.0]])],"derivedFrom":subQ1})])]});var subQ19=makeQuery(id+"F3.opExtrude","CAP_FACE",FACE,{"disambiguationData":[OSD([subQ11,subQ13,sQuery(id+"F2.wireOp",EDGE,"E6.bottom"),subQ10,subQ9,subQ17])],"isStart":false});Q30=makeQuery(id+"F5.boolean.opBoolean","SPLIT",FACE,{"disambiguationData":[TD([subQ18,subQ14,makeQuery(id+"F1.opExtrude","SWEPT_FACE",FACE,{"disambiguationData":[OSD([subQ0]),TDD([makeQuery(id+"F0.imprint","IMPRINT",EDGE,{"disambiguationData":[TD([[subQ2,-1.0]])],"derivedFrom":subQ0})])]}),makeQuery(id+"F1.opExtrude","SWEPT_FACE",FACE,{"disambiguationData":[OSD([subQ3]),TDD([makeQuery(id+"F0.imprint","IMPRINT",EDGE,{"disambiguationData":[TD([[makeQuery(id+"F0.imprint","INTERSECT",VERTEX,{"derivedFrom":[subQ3,subQ7]}),-1.0]])],"derivedFrom":subQ3})])]}),subQ19,makeQuery(id+"F3.opExtrude","SWEPT_FACE",FACE,{"disambiguationData":[OSD([subQ17])]}),makeQuery(id+"F5.opExtrude","SWEPT_FACE",FACE,{"disambiguationData":[OSD([subQ4]),TDD([makeQuery(id+"F4.imprint","IMPRINT",EDGE,{"disambiguationData":[TD([[makeQuery(id+"F4.imprint","INTERSECT",VERTEX,{"derivedFrom":[subQ4,subQ15]}),-1.0]])],"derivedFrom":subQ4})])]}),makeQuery(id+"F5.opExtrude","CAP_FACE",FACE,{"disambiguationData":[OSD([subQ11,subQ5,subQ7,subQ10,subQ4,sQuery(id+"F4.wireOp",EDGE,"E11.top"),subQ15,sQuery(id+"F4.wireOp",EDGE,"E11.right")])],"isStart":false})])],"derivedFrom":makeQuery(id+"F3.boolean.opBoolean","MERGE",FACE,{"derivedFrom":[subQ18,subQ19]})});}
            var Q31;
            {var subQ0=sQuery(id+"F0.wireOp",EDGE,"E0.left");var subQ1=sQuery(id+"F0.wireOp",EDGE,"E0.top");var subQ2=makeQuery(id+"F0.imprint","INTERSECT",VERTEX,{"derivedFrom":[subQ1,subQ0]});var subQ3=sQuery(id+"F0.wireOp",EDGE,"E5.right");var subQ5=makeQuery(id+"F1.opExtrude","SWEPT_FACE",FACE,{"disambiguationData":[OSD([subQ0]),TDD([makeQuery(id+"F0.imprint","IMPRINT",EDGE,{"disambiguationData":[TD([[subQ2,1.0]])],"derivedFrom":subQ0})])]});var subQ7=makeQuery(id+"F1.opExtrude","SWEPT_FACE",FACE,{"disambiguationData":[OSD([subQ1]),TDD([makeQuery(id+"F0.imprint","IMPRINT",EDGE,{"disambiguationData":[TD([[subQ2,-1.0]])],"derivedFrom":subQ1})])]});var subQ8=sQuery(id+"F0.wireOp",EDGE,"E5.bottom");var subQ9=makeQuery(id+"F0.imprint","INTERSECT",VERTEX,{"derivedFrom":[subQ8,subQ3]});var subQ10=makeQuery(id+"F1.opExtrude","SWEPT_FACE",FACE,{"disambiguationData":[OSD([subQ3]),TDD([makeQuery(id+"F0.imprint","IMPRINT",EDGE,{"disambiguationData":[TD([[subQ9,-1.0]])],"derivedFrom":subQ3})])]});var subQ11=sQuery(id+"F0.wireOp",EDGE,"E5.left");var subQ12=sQuery(id+"F0.wireOp",EDGE,"E5.top");var subQ13=sQuery(id+"F0.wireOp",EDGE,"E0.right");var subQ14=sQuery(id+"F0.wireOp",EDGE,"E0.bottom");var subQ15=makeQuery(id+"F1.opExtrude","CAP_FACE",FACE,{"disambiguationData":[OSD([subQ14,subQ1,subQ0,subQ13,subQ8,subQ12,subQ11,subQ3])],"isStart":true});var subQ16=sQuery(id+"F4.wireOp",EDGE,"E11.right");var subQ17=makeQuery(id+"F1.opExtrude","SWEPT_FACE",FACE,{"disambiguationData":[OSD([subQ3]),TDD([makeQuery(id+"F0.imprint","IMPRINT",EDGE,{"disambiguationData":[TD([[makeQuery(id+"F0.imprint","INTERSECT",VERTEX,{"derivedFrom":[subQ12,subQ3]}),1.0]])],"derivedFrom":subQ3})])]});var subQ18=sQuery(id+"F2.wireOp",EDGE,"E6.right");var subQ19=sQuery(id+"F2.wireOp",EDGE,"E6.left");var subQ20=sQuery(id+"F2.wireOp",EDGE,"E6.top");var subQ21=sQuery(id+"F2.wireOp",EDGE,"E6.bottom");var subQ22=makeQuery(id+"F3.opExtrude","CAP_FACE",FACE,{"disambiguationData":[OSD([subQ1,subQ12,subQ21,subQ20,subQ19,subQ18])],"isStart":true});var subQ23=makeQuery(id+"F3.opExtrude","SWEPT_FACE",FACE,{"disambiguationData":[OSD([subQ18])]});var subQ26=makeQuery(id+"F0.imprint","INTERSECT",VERTEX,{"derivedFrom":[subQ14,subQ0]});Q31=makeQuery(id+"F5.boolean.opBoolean","SPLIT",FACE,{"disambiguationData":[TD([subQ15,subQ7,subQ5,subQ10,subQ17,subQ22,subQ23,makeQuery(id+"F5.opExtrude","CAP_FACE",FACE,{"disambiguationData":[OSD([subQ1,subQ13,subQ11,subQ20,sQuery(id+"F4.wireOp",EDGE,"E11.bottom"),sQuery(id+"F4.wireOp",EDGE,"E11.top"),sQuery(id+"F4.wireOp",EDGE,"E11.left"),subQ16])],"isStart":false}),makeQuery(id+"F5.opExtrude","SWEPT_FACE",FACE,{"disambiguationData":[OSD([subQ16])]})])],"derivedFrom":makeQuery(id+"F3.boolean.opBoolean","SPLIT",FACE,{"disambiguationData":[TD([makeQuery(id+"F1.opExtrude","SWEPT_FACE",FACE,{"disambiguationData":[OSD([subQ14]),TDD([makeQuery(id+"F0.imprint","IMPRINT",EDGE,{"disambiguationData":[TD([[subQ26,-1.0]])],"derivedFrom":subQ14})])]}),subQ15,subQ7,makeQuery(id+"F1.opExtrude","SWEPT_FACE",FACE,{"disambiguationData":[OSD([subQ0]),TDD([makeQuery(id+"F0.imprint","IMPRINT",EDGE,{"disambiguationData":[TD([[subQ26,-1.0]])],"derivedFrom":subQ0})])]}),subQ5,makeQuery(id+"F1.opExtrude","SWEPT_FACE",FACE,{"disambiguationData":[OSD([subQ8]),TDD([makeQuery(id+"F0.imprint","IMPRINT",EDGE,{"disambiguationData":[TD([[makeQuery(id+"F0.imprint","INTERSECT",VERTEX,{"derivedFrom":[subQ8,subQ11]}),-1.0]])],"derivedFrom":subQ8})])]}),makeQuery(id+"F1.opExtrude","SWEPT_FACE",FACE,{"disambiguationData":[OSD([subQ8]),TDD([makeQuery(id+"F0.imprint","IMPRINT",EDGE,{"disambiguationData":[TD([[subQ9,1.0]])],"derivedFrom":subQ8})])]}),subQ10,subQ17,subQ22,makeQuery(id+"F3.opExtrude","CAP_FACE",FACE,{"disambiguationData":[OSD([subQ1,subQ12,subQ21,subQ20,subQ19,subQ18])],"isStart":false}),subQ23])],"derivedFrom":subQ15})});}
            var Q32;
            {var subQ1=sQuery(id+"F0.wireOp",EDGE,"E0.top");var subQ8=sQuery(id+"F0.wireOp",EDGE,"E5.left");var subQ10=sQuery(id+"F0.wireOp",EDGE,"E0.right");var subQ12=sQuery(id+"F4.wireOp",EDGE,"E11.right");var subQ13=sQuery(id+"F4.wireOp",EDGE,"E11.bottom");var subQ14=sQuery(id+"F2.wireOp",EDGE,"E6.top");Q32=makeQuery(id+"F5.boolean.opBoolean","SPLIT",FACE,{"disambiguationData":[TD([makeQuery(id+"F5.opExtrude","SWEPT_FACE",FACE,{"disambiguationData":[OSD([subQ13]),TDD([makeQuery(id+"F4.imprint","IMPRINT",EDGE,{"disambiguationData":[TD([[makeQuery(id+"F4.imprint","INTERSECT",VERTEX,{"derivedFrom":[subQ13,subQ12]}),1.0]])],"derivedFrom":subQ13})])]})])],"derivedFrom":makeQuery(id+"F5.opExtrude","CAP_FACE",FACE,{"disambiguationData":[OSD([subQ1,subQ10,subQ8,subQ14,subQ13,sQuery(id+"F4.wireOp",EDGE,"E11.top"),sQuery(id+"F4.wireOp",EDGE,"E11.left"),subQ12])],"isStart":false})});}
            var Q33;
            {var subQ0=sQuery(id+"F0.wireOp",EDGE,"E5.left");var subQ1=sQuery(id+"F0.wireOp",EDGE,"E5.top");var subQ2=makeQuery(id+"F0.imprint","INTERSECT",VERTEX,{"derivedFrom":[subQ1,subQ0]});var subQ8=sQuery(id+"F4.wireOp",EDGE,"E11.right");var subQ9=makeQuery(id+"F5.opExtrude","SWEPT_FACE",FACE,{"disambiguationData":[OSD([subQ8])]});Q33=makeQuery(id+"F5.boolean.opBoolean","SPLIT",FACE,{"disambiguationData":[TD([makeQuery(id+"F1.opExtrude","SWEPT_FACE",FACE,{"disambiguationData":[OSD([subQ1]),TDD([makeQuery(id+"F0.imprint","IMPRINT",EDGE,{"disambiguationData":[TD([[subQ2,-1.0]])],"derivedFrom":subQ1})])]})])],"derivedFrom":subQ9});}
            var Q34;
            {var subQ0=sQuery(id+"F0.wireOp",EDGE,"E0.right");var subQ1=sQuery(id+"F0.wireOp",EDGE,"E0.top");var subQ2=makeQuery(id+"F0.imprint","INTERSECT",VERTEX,{"derivedFrom":[subQ1,subQ0]});var subQ3=sQuery(id+"F0.wireOp",EDGE,"E5.top");var subQ5=makeQuery(id+"F1.opExtrude","SWEPT_FACE",FACE,{"disambiguationData":[OSD([subQ0]),TDD([makeQuery(id+"F0.imprint","IMPRINT",EDGE,{"disambiguationData":[TD([[subQ2,1.0]])],"derivedFrom":subQ0})])]});var subQ6=sQuery(id+"F0.wireOp",EDGE,"E0.bottom");var subQ7=makeQuery(id+"F0.imprint","INTERSECT",VERTEX,{"derivedFrom":[subQ6,subQ0]});var subQ8=sQuery(id+"F0.wireOp",EDGE,"E5.left");var subQ10=makeQuery(id+"F1.opExtrude","SWEPT_FACE",FACE,{"disambiguationData":[OSD([subQ0]),TDD([makeQuery(id+"F0.imprint","IMPRINT",EDGE,{"disambiguationData":[TD([[subQ7,-1.0]])],"derivedFrom":subQ0})])]});var subQ11=makeQuery(id+"F0.imprint","INTERSECT",VERTEX,{"derivedFrom":[subQ3,subQ8]});var subQ12=makeQuery(id+"F1.opExtrude","SWEPT_FACE",FACE,{"disambiguationData":[OSD([subQ3]),TDD([makeQuery(id+"F0.imprint","IMPRINT",EDGE,{"disambiguationData":[TD([[subQ11,-1.0]])],"derivedFrom":subQ3})])]});var subQ13=sQuery(id+"F0.wireOp",EDGE,"E5.right");var subQ14=sQuery(id+"F0.wireOp",EDGE,"E5.bottom");var subQ15=makeQuery(id+"F1.opExtrude","CAP_FACE",FACE,{"disambiguationData":[OSD([subQ6,subQ1,sQuery(id+"F0.wireOp",EDGE,"E0.left"),subQ0,subQ14,subQ3,subQ8,subQ13])],"isStart":false});var subQ16=makeQuery(id+"F1.opExtrude","SWEPT_FACE",FACE,{"disambiguationData":[OSD([subQ8]),TDD([makeQuery(id+"F0.imprint","IMPRINT",EDGE,{"disambiguationData":[TD([[subQ11,1.0]])],"derivedFrom":subQ8})])]});var subQ17=sQuery(id+"F4.wireOp",EDGE,"E11.left");var subQ18=sQuery(id+"F4.wireOp",EDGE,"E11.top");var subQ19=sQuery(id+"F2.wireOp",EDGE,"E6.top");var subQ20=sQuery(id+"F2.wireOp",EDGE,"E6.left");var subQ21=sQuery(id+"F2.wireOp",EDGE,"E6.right");var subQ22=sQuery(id+"F2.wireOp",EDGE,"E6.bottom");var subQ24=makeQuery(id+"F0.imprint","IMPRINT",EDGE,{"disambiguationData":[TD([[subQ2,1.0]])],"derivedFrom":subQ1});Q34=makeQuery(id+"F5.boolean.opBoolean","SPLIT",FACE,{"disambiguationData":[TD([subQ15,subQ10,subQ5,subQ12,subQ16,makeQuery(id+"F5.opExtrude","CAP_FACE",FACE,{"disambiguationData":[OSD([subQ1,subQ0,subQ8,subQ19,sQuery(id+"F4.wireOp",EDGE,"E11.bottom"),subQ18,subQ17,sQuery(id+"F4.wireOp",EDGE,"E11.right")])],"isStart":true}),makeQuery(id+"F5.opExtrude","SWEPT_FACE",FACE,{"disambiguationData":[OSD([subQ18])]}),makeQuery(id+"F5.opExtrude","SWEPT_FACE",FACE,{"disambiguationData":[OSD([subQ17])]})])],"derivedFrom":makeQuery(id+"F3.boolean.opBoolean","SPLIT",FACE,{"disambiguationData":[TD([subQ15,makeQuery(id+"F1.opExtrude","SWEPT_FACE",FACE,{"disambiguationData":[OSD([subQ6]),TDD([makeQuery(id+"F0.imprint","IMPRINT",EDGE,{"disambiguationData":[TD([[subQ7,1.0]])],"derivedFrom":subQ6})])]}),makeQuery(id+"F1.opExtrude","SWEPT_FACE",FACE,{"disambiguationData":[OSD([subQ1]),TDD([subQ24])]}),subQ10,subQ5,subQ12,makeQuery(id+"F1.opExtrude","SWEPT_FACE",FACE,{"disambiguationData":[OSD([subQ3]),TDD([makeQuery(id+"F0.imprint","IMPRINT",EDGE,{"disambiguationData":[TD([[makeQuery(id+"F0.imprint","INTERSECT",VERTEX,{"derivedFrom":[subQ3,subQ13]}),1.0]])],"derivedFrom":subQ3})])]}),makeQuery(id+"F1.opExtrude","SWEPT_FACE",FACE,{"disambiguationData":[OSD([subQ8]),TDD([makeQuery(id+"F0.imprint","IMPRINT",EDGE,{"disambiguationData":[TD([[makeQuery(id+"F0.imprint","INTERSECT",VERTEX,{"derivedFrom":[subQ14,subQ8]}),-1.0]])],"derivedFrom":subQ8})])]}),subQ16,makeQuery(id+"F3.opExtrude","CAP_FACE",FACE,{"disambiguationData":[OSD([subQ1,subQ3,subQ22,subQ19,subQ20,subQ21])],"isStart":true}),makeQuery(id+"F3.opExtrude","CAP_FACE",FACE,{"disambiguationData":[OSD([subQ1,subQ3,subQ22,subQ19,subQ20,subQ21])],"isStart":false}),makeQuery(id+"F3.opExtrude","CAP_FACE",FACE,{"disambiguationData":[OSD([subQ1,subQ0,subQ19,subQ20])],"isStart":true}),makeQuery(id+"F3.opExtrude","CAP_FACE",FACE,{"disambiguationData":[OSD([subQ1,subQ0,subQ19,subQ20])],"isStart":false}),makeQuery(id+"F3.opExtrude","SWEPT_FACE",FACE,{"disambiguationData":[OSD([subQ20]),TDD([makeQuery(id+"F2.imprint","IMPRINT",EDGE,{"disambiguationData":[TD([[makeQuery(id+"F2.imprint","INTERSECT",VERTEX,{"derivedFrom":[subQ22,subQ20]}),-1.0]])],"derivedFrom":subQ20})])]})])],"derivedFrom":subQ15})});}
            var Q35;
            {var subQ1=sQuery(id+"F0.wireOp",EDGE,"E0.right");var subQ5=sQuery(id+"F4.wireOp",EDGE,"E11.right");var subQ6=sQuery(id+"F4.wireOp",EDGE,"E11.bottom");var subQ10=sQuery(id+"F0.wireOp",EDGE,"E0.bottom");var subQ11=makeQuery(id+"F0.imprint","IMPRINT",EDGE,{"disambiguationData":[TD([[makeQuery(id+"F0.imprint","INTERSECT",VERTEX,{"derivedFrom":[subQ10,subQ1]}),-1.0]])],"derivedFrom":subQ1});var subQ12=makeQuery(id+"F1.opExtrude","SWEPT_FACE",FACE,{"disambiguationData":[OSD([subQ1]),TDD([subQ11])]});var subQ14=makeQuery(id+"F5.opExtrude","SWEPT_FACE",FACE,{"disambiguationData":[OSD([subQ6]),TDD([makeQuery(id+"F4.imprint","IMPRINT",EDGE,{"disambiguationData":[TD([[makeQuery(id+"F4.imprint","INTERSECT",VERTEX,{"derivedFrom":[subQ6,subQ5]}),1.0]])],"derivedFrom":subQ6})])]});Q35=makeQuery(id+"F5.boolean.opBoolean","SPLIT",FACE,{"disambiguationData":[TD([subQ12])],"derivedFrom":subQ14});}
            var Q36;
            {var subQ3=sQuery(id+"F0.wireOp",EDGE,"E0.top");var subQ5=sQuery(id+"F0.wireOp",EDGE,"E0.right");var subQ6=makeQuery(id+"F0.imprint","INTERSECT",VERTEX,{"derivedFrom":[subQ3,subQ5]});var subQ9=sQuery(id+"F4.wireOp",EDGE,"E11.right");var subQ11=makeQuery(id+"F5.opExtrude","SWEPT_FACE",FACE,{"disambiguationData":[OSD([subQ9])]});Q36=makeQuery(id+"F5.boolean.opBoolean","SPLIT",FACE,{"disambiguationData":[TD([makeQuery(id+"F1.opExtrude","SWEPT_FACE",FACE,{"disambiguationData":[OSD([subQ3]),TDD([makeQuery(id+"F0.imprint","IMPRINT",EDGE,{"disambiguationData":[TD([[subQ6,1.0]])],"derivedFrom":subQ3})])]})])],"derivedFrom":subQ11});}
            var Q37;
            {var subQ0=sQuery(id+"F0.wireOp",EDGE,"E5.left");var subQ1=sQuery(id+"F0.wireOp",EDGE,"E5.bottom");var subQ2=sQuery(id+"F0.wireOp",EDGE,"E0.bottom");var subQ4=makeQuery(id+"F1.opExtrude","SWEPT_FACE",FACE,{"disambiguationData":[OSD([subQ0]),TDD([makeQuery(id+"F0.imprint","IMPRINT",EDGE,{"disambiguationData":[TD([[makeQuery(id+"F0.imprint","INTERSECT",VERTEX,{"derivedFrom":[subQ1,subQ0]}),-1.0]])],"derivedFrom":subQ0})])]});var subQ5=sQuery(id+"F0.wireOp",EDGE,"E0.right");var subQ6=makeQuery(id+"F0.imprint","INTERSECT",VERTEX,{"derivedFrom":[subQ2,subQ5]});var subQ7=makeQuery(id+"F1.opExtrude","SWEPT_FACE",FACE,{"disambiguationData":[OSD([subQ2]),TDD([makeQuery(id+"F0.imprint","IMPRINT",EDGE,{"disambiguationData":[TD([[subQ6,1.0]])],"derivedFrom":subQ2})])]});var subQ8=sQuery(id+"F2.wireOp",EDGE,"E6.right");var subQ9=sQuery(id+"F2.wireOp",EDGE,"E6.left");var subQ10=sQuery(id+"F2.wireOp",EDGE,"E6.top");var subQ11=sQuery(id+"F2.wireOp",EDGE,"E6.bottom");var subQ12=sQuery(id+"F0.wireOp",EDGE,"E5.top");var subQ13=sQuery(id+"F0.wireOp",EDGE,"E0.top");var subQ14=makeQuery(id+"F3.opExtrude","CAP_FACE",FACE,{"disambiguationData":[OSD([subQ13,subQ12,subQ11,subQ10,subQ9,subQ8])],"isStart":false});var subQ16=makeQuery(id+"F1.opExtrude","SWEPT_FACE",FACE,{"disambiguationData":[OSD([subQ5]),TDD([makeQuery(id+"F0.imprint","IMPRINT",EDGE,{"disambiguationData":[TD([[subQ6,-1.0]])],"derivedFrom":subQ5})])]});var subQ17=makeQuery(id+"F0.imprint","INTERSECT",VERTEX,{"derivedFrom":[subQ13,subQ5]});var subQ19=makeQuery(id+"F0.imprint","IMPRINT",EDGE,{"disambiguationData":[TD([[subQ17,1.0]])],"derivedFrom":subQ13});var subQ20=makeQuery(id+"F3.opExtrude","SWEPT_FACE",FACE,{"disambiguationData":[OSD([subQ9]),TDD([makeQuery(id+"F2.imprint","IMPRINT",EDGE,{"disambiguationData":[TD([[makeQuery(id+"F2.imprint","INTERSECT",VERTEX,{"derivedFrom":[subQ11,subQ9]}),-1.0]])],"derivedFrom":subQ9})])]});var subQ21=sQuery(id+"F0.wireOp",EDGE,"E5.right");var subQ22=makeQuery(id+"F1.opExtrude","CAP_FACE",FACE,{"disambiguationData":[OSD([subQ2,subQ13,sQuery(id+"F0.wireOp",EDGE,"E0.left"),subQ5,subQ1,subQ12,subQ0,subQ21])],"isStart":false});var subQ23=makeQuery(id+"F0.imprint","INTERSECT",VERTEX,{"derivedFrom":[subQ12,subQ0]});var subQ24=makeQuery(id+"F1.opExtrude","SWEPT_FACE",FACE,{"disambiguationData":[OSD([subQ0]),TDD([makeQuery(id+"F0.imprint","IMPRINT",EDGE,{"disambiguationData":[TD([[subQ23,1.0]])],"derivedFrom":subQ0})])]});var subQ25=makeQuery(id+"F3.opExtrude","CAP_FACE",FACE,{"disambiguationData":[OSD([subQ13,subQ5,subQ10,subQ9])],"isStart":false});var subQ26=sQuery(id+"F4.wireOp",EDGE,"E11.left");Q37=makeQuery(id+"F5.boolean.opBoolean","SPLIT",FACE,{"disambiguationData":[TD([subQ22,subQ7,subQ16,subQ4,subQ24,subQ14,subQ25,subQ20,makeQuery(id+"F5.opExtrude","CAP_FACE",FACE,{"disambiguationData":[OSD([subQ13,subQ5,subQ0,subQ10,sQuery(id+"F4.wireOp",EDGE,"E11.bottom"),sQuery(id+"F4.wireOp",EDGE,"E11.top"),subQ26,sQuery(id+"F4.wireOp",EDGE,"E11.right")])],"isStart":true}),makeQuery(id+"F5.opExtrude","SWEPT_FACE",FACE,{"disambiguationData":[OSD([subQ26])]})])],"derivedFrom":makeQuery(id+"F3.boolean.opBoolean","SPLIT",FACE,{"disambiguationData":[TD([subQ22,subQ7,makeQuery(id+"F1.opExtrude","SWEPT_FACE",FACE,{"disambiguationData":[OSD([subQ13]),TDD([subQ19])]}),subQ16,makeQuery(id+"F1.opExtrude","SWEPT_FACE",FACE,{"disambiguationData":[OSD([subQ5]),TDD([makeQuery(id+"F0.imprint","IMPRINT",EDGE,{"disambiguationData":[TD([[subQ17,1.0]])],"derivedFrom":subQ5})])]}),makeQuery(id+"F1.opExtrude","SWEPT_FACE",FACE,{"disambiguationData":[OSD([subQ12]),TDD([makeQuery(id+"F0.imprint","IMPRINT",EDGE,{"disambiguationData":[TD([[subQ23,-1.0]])],"derivedFrom":subQ12})])]}),makeQuery(id+"F1.opExtrude","SWEPT_FACE",FACE,{"disambiguationData":[OSD([subQ12]),TDD([makeQuery(id+"F0.imprint","IMPRINT",EDGE,{"disambiguationData":[TD([[makeQuery(id+"F0.imprint","INTERSECT",VERTEX,{"derivedFrom":[subQ12,subQ21]}),1.0]])],"derivedFrom":subQ12})])]}),subQ4,subQ24,makeQuery(id+"F3.opExtrude","CAP_FACE",FACE,{"disambiguationData":[OSD([subQ13,subQ12,subQ11,subQ10,subQ9,subQ8])],"isStart":true}),subQ14,makeQuery(id+"F3.opExtrude","CAP_FACE",FACE,{"disambiguationData":[OSD([subQ13,subQ5,subQ10,subQ9])],"isStart":true}),subQ25,subQ20])],"derivedFrom":subQ22})});}
            var Q38;
            {var subQ7=sQuery(id+"F0.wireOp",EDGE,"E0.left");var subQ9=sQuery(id+"F0.wireOp",EDGE,"E0.bottom");var subQ12=sQuery(id+"F4.wireOp",EDGE,"E11.right");var subQ13=sQuery(id+"F4.wireOp",EDGE,"E11.bottom");var subQ16=makeQuery(id+"F5.opExtrude","SWEPT_FACE",FACE,{"disambiguationData":[OSD([subQ13]),TDD([makeQuery(id+"F4.imprint","IMPRINT",EDGE,{"disambiguationData":[TD([[makeQuery(id+"F4.imprint","INTERSECT",VERTEX,{"derivedFrom":[subQ13,subQ12]}),1.0]])],"derivedFrom":subQ13})])]});Q38=makeQuery(id+"F5.boolean.opBoolean","SPLIT",FACE,{"disambiguationData":[TD([makeQuery(id+"F1.opExtrude","SWEPT_FACE",FACE,{"disambiguationData":[OSD([subQ7]),TDD([makeQuery(id+"F0.imprint","IMPRINT",EDGE,{"disambiguationData":[TD([[makeQuery(id+"F0.imprint","INTERSECT",VERTEX,{"derivedFrom":[subQ9,subQ7]}),-1.0]])],"derivedFrom":subQ7})])]})])],"derivedFrom":subQ16});}
            var Q39;
            {var subQ3=sQuery(id+"F0.wireOp",EDGE,"E0.top");var subQ7=sQuery(id+"F0.wireOp",EDGE,"E0.left");var subQ8=makeQuery(id+"F0.imprint","INTERSECT",VERTEX,{"derivedFrom":[subQ3,subQ7]});var subQ10=sQuery(id+"F4.wireOp",EDGE,"E11.right");var subQ11=makeQuery(id+"F5.opExtrude","SWEPT_FACE",FACE,{"disambiguationData":[OSD([subQ10])]});Q39=makeQuery(id+"F5.boolean.opBoolean","SPLIT",FACE,{"disambiguationData":[TD([makeQuery(id+"F1.opExtrude","SWEPT_FACE",FACE,{"disambiguationData":[OSD([subQ3]),TDD([makeQuery(id+"F0.imprint","IMPRINT",EDGE,{"disambiguationData":[TD([[subQ8,-1.0]])],"derivedFrom":subQ3})])]})])],"derivedFrom":subQ11});}
            var Q40;
            {var subQ0=sQuery(id+"F0.wireOp",EDGE,"E0.right");var subQ1=sQuery(id+"F0.wireOp",EDGE,"E0.top");var subQ2=makeQuery(id+"F0.imprint","INTERSECT",VERTEX,{"derivedFrom":[subQ1,subQ0]});var subQ3=sQuery(id+"F0.wireOp",EDGE,"E5.top");var subQ5=makeQuery(id+"F1.opExtrude","SWEPT_FACE",FACE,{"disambiguationData":[OSD([subQ0]),TDD([makeQuery(id+"F0.imprint","IMPRINT",EDGE,{"disambiguationData":[TD([[subQ2,1.0]])],"derivedFrom":subQ0})])]});var subQ7=makeQuery(id+"F0.imprint","IMPRINT",EDGE,{"disambiguationData":[TD([[subQ2,1.0]])],"derivedFrom":subQ1});var subQ8=makeQuery(id+"F1.opExtrude","SWEPT_FACE",FACE,{"disambiguationData":[OSD([subQ1]),TDD([subQ7])]});var subQ9=sQuery(id+"F2.wireOp",EDGE,"E6.left");var subQ10=sQuery(id+"F2.wireOp",EDGE,"E6.top");var subQ11=makeQuery(id+"F3.opExtrude","CAP_FACE",FACE,{"disambiguationData":[OSD([subQ1,subQ0,subQ10,subQ9])],"isStart":true});var subQ12=sQuery(id+"F0.wireOp",EDGE,"E5.left");var subQ13=makeQuery(id+"F0.imprint","INTERSECT",VERTEX,{"derivedFrom":[subQ3,subQ12]});var subQ14=makeQuery(id+"F1.opExtrude","SWEPT_FACE",FACE,{"disambiguationData":[OSD([subQ3]),TDD([makeQuery(id+"F0.imprint","IMPRINT",EDGE,{"disambiguationData":[TD([[subQ13,-1.0]])],"derivedFrom":subQ3})])]});var subQ15=sQuery(id+"F0.wireOp",EDGE,"E5.right");var subQ16=sQuery(id+"F0.wireOp",EDGE,"E5.bottom");var subQ17=sQuery(id+"F0.wireOp",EDGE,"E0.bottom");var subQ18=makeQuery(id+"F1.opExtrude","CAP_FACE",FACE,{"disambiguationData":[OSD([subQ17,subQ1,sQuery(id+"F0.wireOp",EDGE,"E0.left"),subQ0,subQ16,subQ3,subQ12,subQ15])],"isStart":false});var subQ19=makeQuery(id+"F1.opExtrude","SWEPT_FACE",FACE,{"disambiguationData":[OSD([subQ3]),TDD([makeQuery(id+"F0.imprint","IMPRINT",EDGE,{"disambiguationData":[TD([[makeQuery(id+"F0.imprint","INTERSECT",VERTEX,{"derivedFrom":[subQ3,subQ15]}),1.0]])],"derivedFrom":subQ3})])]});var subQ20=sQuery(id+"F2.wireOp",EDGE,"E6.right");var subQ21=sQuery(id+"F2.wireOp",EDGE,"E6.bottom");var subQ22=makeQuery(id+"F3.opExtrude","CAP_FACE",FACE,{"disambiguationData":[OSD([subQ1,subQ3,subQ21,subQ10,subQ9,subQ20])],"isStart":true});var subQ23=makeQuery(id+"F3.opExtrude","SWEPT_FACE",FACE,{"disambiguationData":[OSD([subQ9]),TDD([makeQuery(id+"F2.imprint","IMPRINT",EDGE,{"disambiguationData":[TD([[makeQuery(id+"F2.imprint","INTERSECT",VERTEX,{"derivedFrom":[subQ21,subQ9]}),-1.0]])],"derivedFrom":subQ9})])]});var subQ24=sQuery(id+"F4.wireOp",EDGE,"E11.top");var subQ27=makeQuery(id+"F0.imprint","INTERSECT",VERTEX,{"derivedFrom":[subQ17,subQ0]});Q40=makeQuery(id+"F5.boolean.opBoolean","SPLIT",FACE,{"disambiguationData":[TD([subQ18,subQ8,subQ5,subQ14,subQ19,subQ22,subQ11,subQ23,makeQuery(id+"F5.opExtrude","CAP_FACE",FACE,{"disambiguationData":[OSD([subQ1,subQ0,subQ12,subQ10,sQuery(id+"F4.wireOp",EDGE,"E11.bottom"),subQ24,sQuery(id+"F4.wireOp",EDGE,"E11.left"),sQuery(id+"F4.wireOp",EDGE,"E11.right")])],"isStart":true}),makeQuery(id+"F5.opExtrude","SWEPT_FACE",FACE,{"disambiguationData":[OSD([subQ24])]})])],"derivedFrom":makeQuery(id+"F3.boolean.opBoolean","SPLIT",FACE,{"disambiguationData":[TD([subQ18,makeQuery(id+"F1.opExtrude","SWEPT_FACE",FACE,{"disambiguationData":[OSD([subQ17]),TDD([makeQuery(id+"F0.imprint","IMPRINT",EDGE,{"disambiguationData":[TD([[subQ27,1.0]])],"derivedFrom":subQ17})])]}),subQ8,makeQuery(id+"F1.opExtrude","SWEPT_FACE",FACE,{"disambiguationData":[OSD([subQ0]),TDD([makeQuery(id+"F0.imprint","IMPRINT",EDGE,{"disambiguationData":[TD([[subQ27,-1.0]])],"derivedFrom":subQ0})])]}),subQ5,subQ14,subQ19,makeQuery(id+"F1.opExtrude","SWEPT_FACE",FACE,{"disambiguationData":[OSD([subQ12]),TDD([makeQuery(id+"F0.imprint","IMPRINT",EDGE,{"disambiguationData":[TD([[makeQuery(id+"F0.imprint","INTERSECT",VERTEX,{"derivedFrom":[subQ16,subQ12]}),-1.0]])],"derivedFrom":subQ12})])]}),makeQuery(id+"F1.opExtrude","SWEPT_FACE",FACE,{"disambiguationData":[OSD([subQ12]),TDD([makeQuery(id+"F0.imprint","IMPRINT",EDGE,{"disambiguationData":[TD([[subQ13,1.0]])],"derivedFrom":subQ12})])]}),subQ22,makeQuery(id+"F3.opExtrude","CAP_FACE",FACE,{"disambiguationData":[OSD([subQ1,subQ3,subQ21,subQ10,subQ9,subQ20])],"isStart":false}),subQ11,makeQuery(id+"F3.opExtrude","CAP_FACE",FACE,{"disambiguationData":[OSD([subQ1,subQ0,subQ10,subQ9])],"isStart":false}),subQ23])],"derivedFrom":subQ18})});}
            var Q41;
            {var subQ0=sQuery(id+"F0.wireOp",EDGE,"E0.right");var subQ1=sQuery(id+"F0.wireOp",EDGE,"E0.top");var subQ2=sQuery(id+"F0.wireOp",EDGE,"E5.top");var subQ4=sQuery(id+"F0.wireOp",EDGE,"E0.bottom");var subQ5=sQuery(id+"F0.wireOp",EDGE,"E5.left");var subQ8=sQuery(id+"F4.wireOp",EDGE,"E11.top");var subQ9=sQuery(id+"F4.wireOp",EDGE,"E11.left");Q41=makeQuery(id+"F5.boolean.opBoolean","SPLIT",FACE,{"disambiguationData":[TD([makeQuery(id+"F1.opExtrude","CAP_FACE",FACE,{"disambiguationData":[OSD([subQ4,subQ1,sQuery(id+"F0.wireOp",EDGE,"E0.left"),subQ0,sQuery(id+"F0.wireOp",EDGE,"E5.bottom"),subQ2,subQ5,sQuery(id+"F0.wireOp",EDGE,"E5.right")])],"isStart":false})])],"derivedFrom":makeQuery(id+"F5.opExtrude","CAP_FACE",FACE,{"disambiguationData":[OSD([subQ1,subQ0,subQ5,sQuery(id+"F2.wireOp",EDGE,"E6.top"),sQuery(id+"F4.wireOp",EDGE,"E11.bottom"),subQ8,subQ9,sQuery(id+"F4.wireOp",EDGE,"E11.right")])],"isStart":true})});}
            var Q42;
            {var subQ1=sQuery(id+"F2.wireOp",EDGE,"E6.top");var subQ2=sQuery(id+"F0.wireOp",EDGE,"E0.right");var subQ3=sQuery(id+"F0.wireOp",EDGE,"E0.top");var subQ4=makeQuery(id+"F0.imprint","INTERSECT",VERTEX,{"derivedFrom":[subQ3,subQ2]});var subQ8=sQuery(id+"F4.wireOp",EDGE,"E11.top");var subQ9=sQuery(id+"F4.wireOp",EDGE,"E11.right");Q42=makeQuery(id+"F5.boolean.opBoolean","SPLIT",FACE,{"disambiguationData":[TD([makeQuery(id+"F1.opExtrude","SWEPT_FACE",FACE,{"disambiguationData":[OSD([subQ3]),TDD([makeQuery(id+"F0.imprint","IMPRINT",EDGE,{"disambiguationData":[TD([[subQ4,1.0]])],"derivedFrom":subQ3})])]})])],"derivedFrom":makeQuery(id+"F5.opExtrude","CAP_FACE",FACE,{"disambiguationData":[OSD([subQ3,subQ2,sQuery(id+"F0.wireOp",EDGE,"E5.left"),subQ1,sQuery(id+"F4.wireOp",EDGE,"E11.bottom"),subQ8,sQuery(id+"F4.wireOp",EDGE,"E11.left"),subQ9])],"isStart":true})});}
            var Q43;
            {var subQ0=sQuery(id+"F0.wireOp",EDGE,"E5.right");var subQ1=sQuery(id+"F0.wireOp",EDGE,"E5.top");var subQ2=sQuery(id+"F0.wireOp",EDGE,"E0.top");var subQ4=sQuery(id+"F0.wireOp",EDGE,"E0.left");var subQ5=makeQuery(id+"F0.imprint","INTERSECT",VERTEX,{"derivedFrom":[subQ2,subQ4]});var subQ6=makeQuery(id+"F1.opExtrude","SWEPT_FACE",FACE,{"disambiguationData":[OSD([subQ2]),TDD([makeQuery(id+"F0.imprint","IMPRINT",EDGE,{"disambiguationData":[TD([[subQ5,-1.0]])],"derivedFrom":subQ2})])]});var subQ7=sQuery(id+"F0.wireOp",EDGE,"E5.left");var subQ8=sQuery(id+"F0.wireOp",EDGE,"E0.right");var subQ9=sQuery(id+"F4.wireOp",EDGE,"E11.right");var subQ10=sQuery(id+"F2.wireOp",EDGE,"E6.right");var subQ11=sQuery(id+"F2.wireOp",EDGE,"E6.top");var subQ12=makeQuery(id+"F3.opExtrude","CAP_FACE",FACE,{"disambiguationData":[OSD([subQ2,subQ1,sQuery(id+"F2.wireOp",EDGE,"E6.bottom"),subQ11,sQuery(id+"F2.wireOp",EDGE,"E6.left"),subQ10])],"isStart":true});Q43=makeQuery(id+"F5.boolean.opBoolean","SPLIT",FACE,{"disambiguationData":[TD([makeQuery(id+"F1.opExtrude","CAP_FACE",FACE,{"disambiguationData":[OSD([sQuery(id+"F0.wireOp",EDGE,"E0.bottom"),subQ2,subQ4,subQ8,sQuery(id+"F0.wireOp",EDGE,"E5.bottom"),subQ1,subQ7,subQ0])],"isStart":true}),subQ6,makeQuery(id+"F1.opExtrude","SWEPT_FACE",FACE,{"disambiguationData":[OSD([subQ4]),TDD([makeQuery(id+"F0.imprint","IMPRINT",EDGE,{"disambiguationData":[TD([[subQ5,1.0]])],"derivedFrom":subQ4})])]}),makeQuery(id+"F1.opExtrude","SWEPT_FACE",FACE,{"disambiguationData":[OSD([subQ0]),TDD([makeQuery(id+"F0.imprint","IMPRINT",EDGE,{"disambiguationData":[TD([[makeQuery(id+"F0.imprint","INTERSECT",VERTEX,{"derivedFrom":[subQ1,subQ0]}),1.0]])],"derivedFrom":subQ0})])]}),subQ12,makeQuery(id+"F3.opExtrude","SWEPT_FACE",FACE,{"disambiguationData":[OSD([subQ10])]}),makeQuery(id+"F5.opExtrude","CAP_FACE",FACE,{"disambiguationData":[OSD([subQ2,subQ8,subQ7,subQ11,sQuery(id+"F4.wireOp",EDGE,"E11.bottom"),sQuery(id+"F4.wireOp",EDGE,"E11.top"),sQuery(id+"F4.wireOp",EDGE,"E11.left"),subQ9])],"isStart":false}),makeQuery(id+"F5.opExtrude","SWEPT_FACE",FACE,{"disambiguationData":[OSD([subQ9])]})])],"derivedFrom":makeQuery(id+"F3.boolean.opBoolean","MERGE",FACE,{"derivedFrom":[subQ6,subQ12]})});}
            var Q44;
            {var subQ1=sQuery(id+"F4.wireOp",EDGE,"E11.right");var subQ2=sQuery(id+"F0.wireOp",EDGE,"E0.left");var subQ3=sQuery(id+"F0.wireOp",EDGE,"E0.top");var subQ4=makeQuery(id+"F0.imprint","INTERSECT",VERTEX,{"derivedFrom":[subQ3,subQ2]});var subQ7=sQuery(id+"F2.wireOp",EDGE,"E6.top");var subQ8=sQuery(id+"F4.wireOp",EDGE,"E11.top");Q44=makeQuery(id+"F5.boolean.opBoolean","SPLIT",FACE,{"disambiguationData":[TD([makeQuery(id+"F1.opExtrude","SWEPT_FACE",FACE,{"disambiguationData":[OSD([subQ3]),TDD([makeQuery(id+"F0.imprint","IMPRINT",EDGE,{"disambiguationData":[TD([[subQ4,-1.0]])],"derivedFrom":subQ3})])]})])],"derivedFrom":makeQuery(id+"F5.opExtrude","CAP_FACE",FACE,{"disambiguationData":[OSD([subQ3,sQuery(id+"F0.wireOp",EDGE,"E0.right"),sQuery(id+"F0.wireOp",EDGE,"E5.left"),subQ7,sQuery(id+"F4.wireOp",EDGE,"E11.bottom"),subQ8,sQuery(id+"F4.wireOp",EDGE,"E11.left"),subQ1])],"isStart":false})});}
            var Q45;
            {var subQ0=sQuery(id+"F2.wireOp",EDGE,"E6.left");var subQ1=sQuery(id+"F2.wireOp",EDGE,"E6.top");var subQ2=sQuery(id+"F0.wireOp",EDGE,"E0.right");var subQ3=sQuery(id+"F0.wireOp",EDGE,"E0.top");var subQ4=makeQuery(id+"F3.opExtrude","CAP_FACE",FACE,{"disambiguationData":[OSD([subQ3,subQ2,subQ1,subQ0])],"isStart":true});var subQ5=makeQuery(id+"F0.imprint","INTERSECT",VERTEX,{"derivedFrom":[subQ3,subQ2]});var subQ7=makeQuery(id+"F1.opExtrude","SWEPT_FACE",FACE,{"disambiguationData":[OSD([subQ3]),TDD([makeQuery(id+"F0.imprint","IMPRINT",EDGE,{"disambiguationData":[TD([[subQ5,1.0]])],"derivedFrom":subQ3})])]});var subQ8=makeQuery(id+"F2.imprint","INTERSECT",VERTEX,{"derivedFrom":[subQ1,subQ0]});var subQ10=sQuery(id+"F4.wireOp",EDGE,"E11.right");var subQ11=sQuery(id+"F4.wireOp",EDGE,"E11.top");Q45=makeQuery(id+"F5.boolean.opBoolean","SPLIT",FACE,{"disambiguationData":[TD([subQ7,makeQuery(id+"F1.opExtrude","SWEPT_FACE",FACE,{"disambiguationData":[OSD([subQ2]),TDD([makeQuery(id+"F0.imprint","IMPRINT",EDGE,{"disambiguationData":[TD([[subQ5,1.0]])],"derivedFrom":subQ2})])]}),makeQuery(id+"F3.opExtrude","SWEPT_FACE",FACE,{"disambiguationData":[OSD([subQ1]),TDD([makeQuery(id+"F2.imprint","IMPRINT",EDGE,{"disambiguationData":[TD([[subQ8,-1.0]])],"derivedFrom":subQ1})])]}),subQ4,makeQuery(id+"F3.opExtrude","SWEPT_FACE",FACE,{"disambiguationData":[OSD([subQ0]),TDD([makeQuery(id+"F2.imprint","IMPRINT",EDGE,{"disambiguationData":[TD([[subQ8,1.0]])],"derivedFrom":subQ0})])]}),makeQuery(id+"F5.opExtrude","CAP_FACE",FACE,{"disambiguationData":[OSD([subQ3,subQ2,sQuery(id+"F0.wireOp",EDGE,"E5.left"),subQ1,sQuery(id+"F4.wireOp",EDGE,"E11.bottom"),subQ11,sQuery(id+"F4.wireOp",EDGE,"E11.left"),subQ10])],"isStart":true}),makeQuery(id+"F5.opExtrude","SWEPT_FACE",FACE,{"disambiguationData":[OSD([subQ11])]}),makeQuery(id+"F5.opExtrude","SWEPT_FACE",FACE,{"disambiguationData":[OSD([subQ10])]})])],"derivedFrom":makeQuery(id+"F3.boolean.opBoolean","MERGE",FACE,{"derivedFrom":[subQ7,subQ4]})});}
            var Q46;
            {var subQ0=sQuery(id+"F0.wireOp",EDGE,"E5.right");var subQ1=sQuery(id+"F0.wireOp",EDGE,"E5.top");var subQ2=sQuery(id+"F0.wireOp",EDGE,"E0.top");var subQ4=sQuery(id+"F2.wireOp",EDGE,"E6.right");var subQ5=sQuery(id+"F2.wireOp",EDGE,"E6.left");var subQ6=sQuery(id+"F2.wireOp",EDGE,"E6.top");var subQ7=sQuery(id+"F0.wireOp",EDGE,"E0.right");var subQ8=makeQuery(id+"F0.imprint","INTERSECT",VERTEX,{"derivedFrom":[subQ2,subQ7]});var subQ9=makeQuery(id+"F0.imprint","IMPRINT",EDGE,{"disambiguationData":[TD([[subQ8,1.0]])],"derivedFrom":subQ2});var subQ10=makeQuery(id+"F1.opExtrude","SWEPT_FACE",FACE,{"disambiguationData":[OSD([subQ2]),TDD([subQ9])]});var subQ11=makeQuery(id+"F3.opExtrude","CAP_FACE",FACE,{"disambiguationData":[OSD([subQ2,subQ7,subQ6,subQ5])],"isStart":true});var subQ12=sQuery(id+"F0.wireOp",EDGE,"E5.left");var subQ13=sQuery(id+"F4.wireOp",EDGE,"E11.right");Q46=makeQuery(id+"F5.boolean.opBoolean","SPLIT",FACE,{"disambiguationData":[TD([makeQuery(id+"F1.opExtrude","CAP_FACE",FACE,{"disambiguationData":[OSD([sQuery(id+"F0.wireOp",EDGE,"E0.bottom"),subQ2,sQuery(id+"F0.wireOp",EDGE,"E0.left"),subQ7,sQuery(id+"F0.wireOp",EDGE,"E5.bottom"),subQ1,subQ12,subQ0])],"isStart":true}),subQ10,makeQuery(id+"F1.opExtrude","SWEPT_FACE",FACE,{"disambiguationData":[OSD([subQ7]),TDD([makeQuery(id+"F0.imprint","IMPRINT",EDGE,{"disambiguationData":[TD([[subQ8,1.0]])],"derivedFrom":subQ7})])]}),makeQuery(id+"F1.opExtrude","SWEPT_FACE",FACE,{"disambiguationData":[OSD([subQ1]),TDD([makeQuery(id+"F0.imprint","IMPRINT",EDGE,{"disambiguationData":[TD([[makeQuery(id+"F0.imprint","INTERSECT",VERTEX,{"derivedFrom":[subQ1,subQ0]}),1.0]])],"derivedFrom":subQ1})])]}),makeQuery(id+"F3.opExtrude","CAP_FACE",FACE,{"disambiguationData":[OSD([subQ2,subQ1,sQuery(id+"F2.wireOp",EDGE,"E6.bottom"),subQ6,subQ5,subQ4])],"isStart":true}),makeQuery(id+"F3.opExtrude","SWEPT_FACE",FACE,{"disambiguationData":[OSD([subQ6]),TDD([makeQuery(id+"F2.imprint","IMPRINT",EDGE,{"disambiguationData":[TD([[makeQuery(id+"F2.imprint","INTERSECT",VERTEX,{"derivedFrom":[subQ6,subQ5]}),-1.0]])],"derivedFrom":subQ6})])]}),subQ11,makeQuery(id+"F3.opExtrude","SWEPT_FACE",FACE,{"disambiguationData":[OSD([subQ6]),TDD([makeQuery(id+"F2.imprint","IMPRINT",EDGE,{"disambiguationData":[TD([[makeQuery(id+"F2.imprint","INTERSECT",VERTEX,{"derivedFrom":[subQ6,subQ4]}),1.0]])],"derivedFrom":subQ6})])]}),makeQuery(id+"F5.opExtrude","CAP_FACE",FACE,{"disambiguationData":[OSD([subQ2,subQ7,subQ12,subQ6,sQuery(id+"F4.wireOp",EDGE,"E11.bottom"),sQuery(id+"F4.wireOp",EDGE,"E11.top"),sQuery(id+"F4.wireOp",EDGE,"E11.left"),subQ13])],"isStart":true}),makeQuery(id+"F5.opExtrude","SWEPT_FACE",FACE,{"disambiguationData":[OSD([subQ13])]})])],"derivedFrom":makeQuery(id+"F3.boolean.opBoolean","MERGE",FACE,{"derivedFrom":[subQ10,subQ11]})});}
            var Q47;
            {var subQ2=sQuery(id+"F0.wireOp",EDGE,"E0.top");var subQ5=sQuery(id+"F2.wireOp",EDGE,"E6.right");var subQ10=sQuery(id+"F0.wireOp",EDGE,"E0.left");var subQ11=makeQuery(id+"F1.opExtrude","SWEPT_FACE",FACE,{"disambiguationData":[OSD([subQ2]),TDD([makeQuery(id+"F0.imprint","IMPRINT",EDGE,{"disambiguationData":[TD([[makeQuery(id+"F0.imprint","INTERSECT",VERTEX,{"derivedFrom":[subQ2,subQ10]}),-1.0]])],"derivedFrom":subQ2})])]});var subQ12=sQuery(id+"F0.wireOp",EDGE,"E5.left");var subQ13=sQuery(id+"F0.wireOp",EDGE,"E5.bottom");var subQ19=makeQuery(id+"F3.opExtrude","SWEPT_FACE",FACE,{"disambiguationData":[OSD([subQ5])]});Q47=makeQuery(id+"F5.boolean.opBoolean","SPLIT",FACE,{"disambiguationData":[TD([subQ11])],"derivedFrom":makeQuery(id+"F3.boolean.opBoolean","SPLIT",FACE,{"disambiguationData":[TD([makeQuery(id+"F1.opExtrude","SWEPT_FACE",FACE,{"disambiguationData":[OSD([subQ13]),TDD([makeQuery(id+"F0.imprint","IMPRINT",EDGE,{"disambiguationData":[TD([[makeQuery(id+"F0.imprint","INTERSECT",VERTEX,{"derivedFrom":[subQ13,subQ12]}),-1.0]])],"derivedFrom":subQ13})])]})])],"derivedFrom":subQ19})});}
            var Q48;
            {var subQ3=sQuery(id+"F0.wireOp",EDGE,"E0.top");var subQ5=sQuery(id+"F0.wireOp",EDGE,"E0.right");var subQ6=makeQuery(id+"F0.imprint","INTERSECT",VERTEX,{"derivedFrom":[subQ3,subQ5]});var subQ10=sQuery(id+"F4.wireOp",EDGE,"E11.top");var subQ11=makeQuery(id+"F5.opExtrude","SWEPT_FACE",FACE,{"disambiguationData":[OSD([subQ10])]});Q48=makeQuery(id+"F5.boolean.opBoolean","SPLIT",FACE,{"disambiguationData":[TD([makeQuery(id+"F1.opExtrude","SWEPT_FACE",FACE,{"disambiguationData":[OSD([subQ3]),TDD([makeQuery(id+"F0.imprint","IMPRINT",EDGE,{"disambiguationData":[TD([[subQ6,1.0]])],"derivedFrom":subQ3})])]})])],"derivedFrom":subQ11});}
            var Q49;
            {var subQ0=sQuery(id+"F0.wireOp",EDGE,"E5.left");var subQ1=sQuery(id+"F0.wireOp",EDGE,"E5.bottom");var subQ2=sQuery(id+"F0.wireOp",EDGE,"E0.bottom");var subQ4=makeQuery(id+"F1.opExtrude","SWEPT_FACE",FACE,{"disambiguationData":[OSD([subQ0]),TDD([makeQuery(id+"F0.imprint","IMPRINT",EDGE,{"disambiguationData":[TD([[makeQuery(id+"F0.imprint","INTERSECT",VERTEX,{"derivedFrom":[subQ1,subQ0]}),-1.0]])],"derivedFrom":subQ0})])]});var subQ5=sQuery(id+"F0.wireOp",EDGE,"E0.right");var subQ6=makeQuery(id+"F0.imprint","INTERSECT",VERTEX,{"derivedFrom":[subQ2,subQ5]});var subQ7=makeQuery(id+"F1.opExtrude","SWEPT_FACE",FACE,{"disambiguationData":[OSD([subQ2]),TDD([makeQuery(id+"F0.imprint","IMPRINT",EDGE,{"disambiguationData":[TD([[subQ6,1.0]])],"derivedFrom":subQ2})])]});var subQ8=sQuery(id+"F2.wireOp",EDGE,"E6.right");var subQ9=sQuery(id+"F2.wireOp",EDGE,"E6.left");var subQ10=sQuery(id+"F2.wireOp",EDGE,"E6.top");var subQ11=sQuery(id+"F2.wireOp",EDGE,"E6.bottom");var subQ12=sQuery(id+"F0.wireOp",EDGE,"E5.top");var subQ13=sQuery(id+"F0.wireOp",EDGE,"E0.top");var subQ14=makeQuery(id+"F3.opExtrude","CAP_FACE",FACE,{"disambiguationData":[OSD([subQ13,subQ12,subQ11,subQ10,subQ9,subQ8])],"isStart":false});var subQ16=makeQuery(id+"F0.imprint","IMPRINT",EDGE,{"disambiguationData":[TD([[subQ6,-1.0]])],"derivedFrom":subQ5});var subQ17=makeQuery(id+"F1.opExtrude","SWEPT_FACE",FACE,{"disambiguationData":[OSD([subQ5]),TDD([subQ16])]});var subQ18=sQuery(id+"F0.wireOp",EDGE,"E5.right");var subQ19=makeQuery(id+"F1.opExtrude","CAP_FACE",FACE,{"disambiguationData":[OSD([subQ2,subQ13,sQuery(id+"F0.wireOp",EDGE,"E0.left"),subQ5,subQ1,subQ12,subQ0,subQ18])],"isStart":true});var subQ20=makeQuery(id+"F0.imprint","INTERSECT",VERTEX,{"derivedFrom":[subQ12,subQ0]});var subQ21=makeQuery(id+"F1.opExtrude","SWEPT_FACE",FACE,{"disambiguationData":[OSD([subQ0]),TDD([makeQuery(id+"F0.imprint","IMPRINT",EDGE,{"disambiguationData":[TD([[subQ20,1.0]])],"derivedFrom":subQ0})])]});var subQ22=makeQuery(id+"F3.opExtrude","CAP_FACE",FACE,{"disambiguationData":[OSD([subQ13,subQ5,subQ10,subQ9])],"isStart":false});var subQ23=makeQuery(id+"F0.imprint","INTERSECT",VERTEX,{"derivedFrom":[subQ13,subQ5]});var subQ25=makeQuery(id+"F0.imprint","IMPRINT",EDGE,{"disambiguationData":[TD([[subQ23,1.0]])],"derivedFrom":subQ13});var subQ26=makeQuery(id+"F3.opExtrude","SWEPT_FACE",FACE,{"disambiguationData":[OSD([subQ10]),TDD([makeQuery(id+"F2.imprint","IMPRINT",EDGE,{"disambiguationData":[TD([[makeQuery(id+"F2.imprint","INTERSECT",VERTEX,{"derivedFrom":[subQ10,subQ8]}),1.0]])],"derivedFrom":subQ10})])]});var subQ27=sQuery(id+"F4.wireOp",EDGE,"E11.right");var subQ28=sQuery(id+"F4.wireOp",EDGE,"E11.bottom");Q49=makeQuery(id+"F5.boolean.opBoolean","SPLIT",FACE,{"disambiguationData":[TD([subQ19,subQ7,subQ17,subQ4,subQ21,subQ14,subQ22,subQ26,makeQuery(id+"F5.opExtrude","CAP_FACE",FACE,{"disambiguationData":[OSD([subQ13,subQ5,subQ0,subQ10,subQ28,sQuery(id+"F4.wireOp",EDGE,"E11.top"),sQuery(id+"F4.wireOp",EDGE,"E11.left"),subQ27])],"isStart":true}),makeQuery(id+"F5.opExtrude","SWEPT_FACE",FACE,{"disambiguationData":[OSD([subQ28]),TDD([makeQuery(id+"F4.imprint","IMPRINT",EDGE,{"disambiguationData":[TD([[makeQuery(id+"F4.imprint","INTERSECT",VERTEX,{"derivedFrom":[subQ28,subQ27]}),1.0]])],"derivedFrom":subQ28})])]})])],"derivedFrom":makeQuery(id+"F3.boolean.opBoolean","SPLIT",FACE,{"disambiguationData":[TD([subQ19,subQ7,makeQuery(id+"F1.opExtrude","SWEPT_FACE",FACE,{"disambiguationData":[OSD([subQ13]),TDD([subQ25])]}),subQ17,makeQuery(id+"F1.opExtrude","SWEPT_FACE",FACE,{"disambiguationData":[OSD([subQ5]),TDD([makeQuery(id+"F0.imprint","IMPRINT",EDGE,{"disambiguationData":[TD([[subQ23,1.0]])],"derivedFrom":subQ5})])]}),makeQuery(id+"F1.opExtrude","SWEPT_FACE",FACE,{"disambiguationData":[OSD([subQ12]),TDD([makeQuery(id+"F0.imprint","IMPRINT",EDGE,{"disambiguationData":[TD([[subQ20,-1.0]])],"derivedFrom":subQ12})])]}),makeQuery(id+"F1.opExtrude","SWEPT_FACE",FACE,{"disambiguationData":[OSD([subQ12]),TDD([makeQuery(id+"F0.imprint","IMPRINT",EDGE,{"disambiguationData":[TD([[makeQuery(id+"F0.imprint","INTERSECT",VERTEX,{"derivedFrom":[subQ12,subQ18]}),1.0]])],"derivedFrom":subQ12})])]}),subQ4,subQ21,makeQuery(id+"F3.opExtrude","CAP_FACE",FACE,{"disambiguationData":[OSD([subQ13,subQ12,subQ11,subQ10,subQ9,subQ8])],"isStart":true}),subQ14,makeQuery(id+"F3.opExtrude","CAP_FACE",FACE,{"disambiguationData":[OSD([subQ13,subQ5,subQ10,subQ9])],"isStart":true}),subQ22,subQ26])],"derivedFrom":subQ19})});}
            var Q50;
            {var subQ0=sQuery(id+"F0.wireOp",EDGE,"E5.right");var subQ1=sQuery(id+"F0.wireOp",EDGE,"E5.top");var subQ2=makeQuery(id+"F0.imprint","INTERSECT",VERTEX,{"derivedFrom":[subQ1,subQ0]});var subQ3=sQuery(id+"F0.wireOp",EDGE,"E0.top");var subQ5=sQuery(id+"F0.wireOp",EDGE,"E0.right");var subQ6=sQuery(id+"F0.wireOp",EDGE,"E0.left");var subQ7=makeQuery(id+"F1.opExtrude","CAP_FACE",FACE,{"disambiguationData":[OSD([sQuery(id+"F0.wireOp",EDGE,"E0.bottom"),subQ3,subQ6,subQ5,sQuery(id+"F0.wireOp",EDGE,"E5.bottom"),subQ1,sQuery(id+"F0.wireOp",EDGE,"E5.left"),subQ0])],"isStart":false});var subQ8=sQuery(id+"F2.wireOp",EDGE,"E6.left");var subQ9=sQuery(id+"F2.wireOp",EDGE,"E6.top");var subQ10=sQuery(id+"F2.wireOp",EDGE,"E6.bottom");var subQ11=makeQuery(id+"F0.imprint","IMPRINT",EDGE,{"disambiguationData":[TD([[makeQuery(id+"F0.imprint","INTERSECT",VERTEX,{"derivedFrom":[subQ3,subQ5]}),1.0]])],"derivedFrom":subQ3});Q50=makeQuery(id+"F3.boolean.opBoolean","SPLIT",FACE,{"disambiguationData":[TD([subQ7,makeQuery(id+"F1.opExtrude","SWEPT_FACE",FACE,{"disambiguationData":[OSD([subQ3]),TDD([makeQuery(id+"F0.imprint","IMPRINT",EDGE,{"disambiguationData":[TD([[makeQuery(id+"F0.imprint","INTERSECT",VERTEX,{"derivedFrom":[subQ3,subQ6]}),-1.0]])],"derivedFrom":subQ3})])]}),makeQuery(id+"F1.opExtrude","SWEPT_FACE",FACE,{"disambiguationData":[OSD([subQ3]),TDD([subQ11])]}),makeQuery(id+"F1.opExtrude","SWEPT_FACE",FACE,{"disambiguationData":[OSD([subQ1]),TDD([makeQuery(id+"F0.imprint","IMPRINT",EDGE,{"disambiguationData":[TD([[subQ2,1.0]])],"derivedFrom":subQ1})])]}),makeQuery(id+"F1.opExtrude","SWEPT_FACE",FACE,{"disambiguationData":[OSD([subQ0]),TDD([makeQuery(id+"F0.imprint","IMPRINT",EDGE,{"disambiguationData":[TD([[subQ2,1.0]])],"derivedFrom":subQ0})])]}),makeQuery(id+"F3.opExtrude","SWEPT_FACE",FACE,{"disambiguationData":[OSD([subQ10])]}),makeQuery(id+"F3.opExtrude","CAP_FACE",FACE,{"disambiguationData":[OSD([subQ3,subQ1,subQ10,subQ9,subQ8,sQuery(id+"F2.wireOp",EDGE,"E6.right")])],"isStart":true}),makeQuery(id+"F3.opExtrude","CAP_FACE",FACE,{"disambiguationData":[OSD([subQ3,subQ5,subQ9,subQ8])],"isStart":true}),makeQuery(id+"F3.opExtrude","SWEPT_FACE",FACE,{"disambiguationData":[OSD([subQ8]),TDD([makeQuery(id+"F2.imprint","IMPRINT",EDGE,{"disambiguationData":[TD([[makeQuery(id+"F2.imprint","INTERSECT",VERTEX,{"derivedFrom":[subQ10,subQ8]}),-1.0]])],"derivedFrom":subQ8})])]})])],"derivedFrom":subQ7});}
            var Q51;
            {var subQ2=sQuery(id+"F0.wireOp",EDGE,"E0.right");var subQ4=sQuery(id+"F0.wireOp",EDGE,"E0.top");var subQ5=makeQuery(id+"F0.imprint","INTERSECT",VERTEX,{"derivedFrom":[subQ4,subQ2]});var subQ6=sQuery(id+"F2.wireOp",EDGE,"E6.left");var subQ7=sQuery(id+"F2.wireOp",EDGE,"E6.top");Q51=makeQuery(id+"F3.boolean.opBoolean","SPLIT",FACE,{"disambiguationData":[TD([makeQuery(id+"F3.opExtrude","SWEPT_FACE",FACE,{"disambiguationData":[OSD([subQ7]),TDD([makeQuery(id+"F2.imprint","IMPRINT",EDGE,{"disambiguationData":[TD([[makeQuery(id+"F2.imprint","INTERSECT",VERTEX,{"derivedFrom":[subQ7,subQ6]}),-1.0]])],"derivedFrom":subQ7})])]})])],"derivedFrom":makeQuery(id+"F1.opExtrude","SWEPT_FACE",FACE,{"disambiguationData":[OSD([subQ2]),TDD([makeQuery(id+"F0.imprint","IMPRINT",EDGE,{"disambiguationData":[TD([[subQ5,1.0]])],"derivedFrom":subQ2})])]})});}
            var Q52;
            {var subQ0=sQuery(id+"F0.wireOp",EDGE,"E5.right");var subQ1=sQuery(id+"F0.wireOp",EDGE,"E5.bottom");var subQ2=makeQuery(id+"F0.imprint","INTERSECT",VERTEX,{"derivedFrom":[subQ1,subQ0]});var subQ3=sQuery(id+"F0.wireOp",EDGE,"E0.left");var subQ5=makeQuery(id+"F1.opExtrude","SWEPT_FACE",FACE,{"disambiguationData":[OSD([subQ1]),TDD([makeQuery(id+"F0.imprint","IMPRINT",EDGE,{"disambiguationData":[TD([[subQ2,1.0]])],"derivedFrom":subQ1})])]});var subQ6=sQuery(id+"F0.wireOp",EDGE,"E0.bottom");Q52=makeQuery(id+"F3.boolean.opBoolean","SPLIT",FACE,{"disambiguationData":[TD([makeQuery(id+"F1.opExtrude","CAP_FACE",FACE,{"disambiguationData":[OSD([subQ6,sQuery(id+"F0.wireOp",EDGE,"E0.top"),subQ3,sQuery(id+"F0.wireOp",EDGE,"E0.right"),subQ1,sQuery(id+"F0.wireOp",EDGE,"E5.top"),sQuery(id+"F0.wireOp",EDGE,"E5.left"),subQ0])],"isStart":false})])],"derivedFrom":subQ5});}
            var Q53;
            {var subQ2=sQuery(id+"F0.wireOp",EDGE,"E0.left");var subQ4=sQuery(id+"F0.wireOp",EDGE,"E0.bottom");var subQ5=makeQuery(id+"F0.imprint","INTERSECT",VERTEX,{"derivedFrom":[subQ4,subQ2]});var subQ8=sQuery(id+"F2.wireOp",EDGE,"E6.right");Q53=makeQuery(id+"F3.boolean.opBoolean","SPLIT",FACE,{"disambiguationData":[TD([makeQuery(id+"F3.opExtrude","SWEPT_FACE",FACE,{"disambiguationData":[OSD([subQ8])]})])],"derivedFrom":makeQuery(id+"F1.opExtrude","SWEPT_FACE",FACE,{"disambiguationData":[OSD([subQ2]),TDD([makeQuery(id+"F0.imprint","IMPRINT",EDGE,{"disambiguationData":[TD([[subQ5,-1.0]])],"derivedFrom":subQ2})])]})});}
            var Q54;
            {var subQ0=sQuery(id+"F0.wireOp",EDGE,"E5.left");var subQ1=sQuery(id+"F0.wireOp",EDGE,"E5.bottom");var subQ2=makeQuery(id+"F0.imprint","INTERSECT",VERTEX,{"derivedFrom":[subQ1,subQ0]});var subQ5=sQuery(id+"F2.wireOp",EDGE,"E6.right");var subQ14=makeQuery(id+"F1.opExtrude","SWEPT_FACE",FACE,{"disambiguationData":[OSD([subQ1]),TDD([makeQuery(id+"F0.imprint","IMPRINT",EDGE,{"disambiguationData":[TD([[subQ2,-1.0]])],"derivedFrom":subQ1})])]});Q54=makeQuery(id+"F5.boolean.opBoolean","SPLIT",FACE,{"disambiguationData":[TD([makeQuery(id+"F3.opExtrude","SWEPT_FACE",FACE,{"disambiguationData":[OSD([subQ5])]})])],"derivedFrom":subQ14});}
            var Q55;
            {var subQ0=sQuery(id+"F0.wireOp",EDGE,"E5.right");var subQ1=sQuery(id+"F0.wireOp",EDGE,"E5.bottom");var subQ2=makeQuery(id+"F0.imprint","INTERSECT",VERTEX,{"derivedFrom":[subQ1,subQ0]});var subQ3=sQuery(id+"F0.wireOp",EDGE,"E0.left");var subQ5=makeQuery(id+"F1.opExtrude","SWEPT_FACE",FACE,{"disambiguationData":[OSD([subQ1]),TDD([makeQuery(id+"F0.imprint","IMPRINT",EDGE,{"disambiguationData":[TD([[subQ2,1.0]])],"derivedFrom":subQ1})])]});var subQ6=sQuery(id+"F0.wireOp",EDGE,"E0.bottom");Q55=makeQuery(id+"F3.boolean.opBoolean","SPLIT",FACE,{"disambiguationData":[TD([makeQuery(id+"F1.opExtrude","CAP_FACE",FACE,{"disambiguationData":[OSD([subQ6,sQuery(id+"F0.wireOp",EDGE,"E0.top"),subQ3,sQuery(id+"F0.wireOp",EDGE,"E0.right"),subQ1,sQuery(id+"F0.wireOp",EDGE,"E5.top"),sQuery(id+"F0.wireOp",EDGE,"E5.left"),subQ0])],"isStart":true})])],"derivedFrom":subQ5});}
            var Q56;
            {var subQ3=sQuery(id+"F0.wireOp",EDGE,"E0.left");var subQ5=sQuery(id+"F0.wireOp",EDGE,"E0.bottom");var subQ6=makeQuery(id+"F0.imprint","INTERSECT",VERTEX,{"derivedFrom":[subQ5,subQ3]});var subQ7=sQuery(id+"F2.wireOp",EDGE,"E6.bottom");var subQ8=makeQuery(id+"F3.opExtrude","SWEPT_FACE",FACE,{"disambiguationData":[OSD([subQ7])]});Q56=makeQuery(id+"F3.boolean.opBoolean","SPLIT",FACE,{"disambiguationData":[TD([makeQuery(id+"F1.opExtrude","SWEPT_FACE",FACE,{"disambiguationData":[OSD([subQ3]),TDD([makeQuery(id+"F0.imprint","IMPRINT",EDGE,{"disambiguationData":[TD([[subQ6,-1.0]])],"derivedFrom":subQ3})])]})])],"derivedFrom":subQ8});}
            var Q57;
            {var subQ1=sQuery(id+"F0.wireOp",EDGE,"E5.top");var subQ3=sQuery(id+"F0.wireOp",EDGE,"E0.top");var subQ7=sQuery(id+"F2.wireOp",EDGE,"E6.left");var subQ8=sQuery(id+"F2.wireOp",EDGE,"E6.top");var subQ9=sQuery(id+"F2.wireOp",EDGE,"E6.bottom");var subQ10=makeQuery(id+"F3.opExtrude","CAP_FACE",FACE,{"disambiguationData":[OSD([subQ3,subQ1,subQ9,subQ8,subQ7,sQuery(id+"F2.wireOp",EDGE,"E6.right")])],"isStart":true});Q57=makeQuery(id+"F3.boolean.opBoolean","SPLIT",FACE,{"disambiguationData":[TD([makeQuery(id+"F3.opExtrude","SWEPT_FACE",FACE,{"disambiguationData":[OSD([subQ9])]})])],"derivedFrom":subQ10});}
            var Q58;
            {var subQ0=sQuery(id+"F0.wireOp",EDGE,"E0.right");var subQ1=sQuery(id+"F0.wireOp",EDGE,"E0.bottom");var subQ2=sQuery(id+"F0.wireOp",EDGE,"E5.left");var subQ4=sQuery(id+"F0.wireOp",EDGE,"E5.bottom");var subQ5=makeQuery(id+"F0.imprint","INTERSECT",VERTEX,{"derivedFrom":[subQ4,subQ2]});var subQ6=sQuery(id+"F2.wireOp",EDGE,"E6.left");var subQ7=sQuery(id+"F2.wireOp",EDGE,"E6.top");var subQ8=sQuery(id+"F2.wireOp",EDGE,"E6.bottom");var subQ9=sQuery(id+"F0.wireOp",EDGE,"E5.top");var subQ10=sQuery(id+"F0.wireOp",EDGE,"E0.top");var subQ11=sQuery(id+"F0.wireOp",EDGE,"E0.left");var subQ12=makeQuery(id+"F1.opExtrude","CAP_FACE",FACE,{"disambiguationData":[OSD([subQ1,subQ10,subQ11,subQ0,subQ4,subQ9,subQ2,sQuery(id+"F0.wireOp",EDGE,"E5.right")])],"isStart":false});Q58=makeQuery(id+"F3.boolean.opBoolean","SPLIT",FACE,{"disambiguationData":[TD([makeQuery(id+"F1.opExtrude","SWEPT_FACE",FACE,{"disambiguationData":[OSD([subQ1]),TDD([makeQuery(id+"F0.imprint","IMPRINT",EDGE,{"disambiguationData":[TD([[makeQuery(id+"F0.imprint","INTERSECT",VERTEX,{"derivedFrom":[subQ1,subQ11]}),-1.0]])],"derivedFrom":subQ1})])]}),subQ12,makeQuery(id+"F1.opExtrude","SWEPT_FACE",FACE,{"disambiguationData":[OSD([subQ1]),TDD([makeQuery(id+"F0.imprint","IMPRINT",EDGE,{"disambiguationData":[TD([[makeQuery(id+"F0.imprint","INTERSECT",VERTEX,{"derivedFrom":[subQ1,subQ0]}),1.0]])],"derivedFrom":subQ1})])]}),makeQuery(id+"F1.opExtrude","SWEPT_FACE",FACE,{"disambiguationData":[OSD([subQ4]),TDD([makeQuery(id+"F0.imprint","IMPRINT",EDGE,{"disambiguationData":[TD([[subQ5,-1.0]])],"derivedFrom":subQ4})])]}),makeQuery(id+"F1.opExtrude","SWEPT_FACE",FACE,{"disambiguationData":[OSD([subQ2]),TDD([makeQuery(id+"F0.imprint","IMPRINT",EDGE,{"disambiguationData":[TD([[subQ5,-1.0]])],"derivedFrom":subQ2})])]}),makeQuery(id+"F3.opExtrude","SWEPT_FACE",FACE,{"disambiguationData":[OSD([subQ8])]}),makeQuery(id+"F3.opExtrude","CAP_FACE",FACE,{"disambiguationData":[OSD([subQ10,subQ9,subQ8,subQ7,subQ6,sQuery(id+"F2.wireOp",EDGE,"E6.right")])],"isStart":false}),makeQuery(id+"F3.opExtrude","CAP_FACE",FACE,{"disambiguationData":[OSD([subQ10,subQ0,subQ7,subQ6])],"isStart":false}),makeQuery(id+"F3.opExtrude","SWEPT_FACE",FACE,{"disambiguationData":[OSD([subQ6]),TDD([makeQuery(id+"F2.imprint","IMPRINT",EDGE,{"disambiguationData":[TD([[makeQuery(id+"F2.imprint","INTERSECT",VERTEX,{"derivedFrom":[subQ8,subQ6]}),-1.0]])],"derivedFrom":subQ6})])]})])],"derivedFrom":subQ12});}
            var Q59;
            {var subQ3=sQuery(id+"F0.wireOp",EDGE,"E0.right");var subQ5=sQuery(id+"F2.wireOp",EDGE,"E6.left");var subQ6=sQuery(id+"F2.wireOp",EDGE,"E6.top");var subQ7=makeQuery(id+"F2.imprint","INTERSECT",VERTEX,{"derivedFrom":[subQ6,subQ5]});var subQ10=sQuery(id+"F0.wireOp",EDGE,"E0.bottom");var subQ11=makeQuery(id+"F0.imprint","INTERSECT",VERTEX,{"derivedFrom":[subQ10,subQ3]});var subQ12=makeQuery(id+"F3.opExtrude","SWEPT_FACE",FACE,{"disambiguationData":[OSD([subQ5]),TDD([makeQuery(id+"F2.imprint","IMPRINT",EDGE,{"disambiguationData":[TD([[subQ7,1.0]])],"derivedFrom":subQ5})])]});Q59=makeQuery(id+"F3.boolean.opBoolean","SPLIT",FACE,{"disambiguationData":[TD([makeQuery(id+"F1.opExtrude","SWEPT_FACE",FACE,{"disambiguationData":[OSD([subQ10]),TDD([makeQuery(id+"F0.imprint","IMPRINT",EDGE,{"disambiguationData":[TD([[subQ11,1.0]])],"derivedFrom":subQ10})])]})])],"derivedFrom":subQ12});}
            var Q60;
            {var subQ6=sQuery(id+"F2.wireOp",EDGE,"E6.right");var subQ7=sQuery(id+"F2.wireOp",EDGE,"E6.left");var subQ8=sQuery(id+"F2.wireOp",EDGE,"E6.top");var subQ9=sQuery(id+"F0.wireOp",EDGE,"E5.top");var subQ10=sQuery(id+"F0.wireOp",EDGE,"E0.top");var subQ11=makeQuery(id+"F3.opExtrude","CAP_FACE",FACE,{"disambiguationData":[OSD([subQ10,subQ9,sQuery(id+"F2.wireOp",EDGE,"E6.bottom"),subQ8,subQ7,subQ6])],"isStart":false});Q60=makeQuery(id+"F3.boolean.opBoolean","SPLIT",FACE,{"disambiguationData":[TD([makeQuery(id+"F3.opExtrude","SWEPT_FACE",FACE,{"disambiguationData":[OSD([subQ6])]})])],"derivedFrom":subQ11});}
            var Q61;
            {var subQ6=sQuery(id+"F2.wireOp",EDGE,"E6.left");var subQ7=sQuery(id+"F2.wireOp",EDGE,"E6.top");var subQ8=sQuery(id+"F2.wireOp",EDGE,"E6.bottom");var subQ9=sQuery(id+"F0.wireOp",EDGE,"E5.top");var subQ10=sQuery(id+"F0.wireOp",EDGE,"E0.top");var subQ11=makeQuery(id+"F3.opExtrude","CAP_FACE",FACE,{"disambiguationData":[OSD([subQ10,subQ9,subQ8,subQ7,subQ6,sQuery(id+"F2.wireOp",EDGE,"E6.right")])],"isStart":false});Q61=makeQuery(id+"F3.boolean.opBoolean","SPLIT",FACE,{"disambiguationData":[TD([makeQuery(id+"F3.opExtrude","SWEPT_FACE",FACE,{"disambiguationData":[OSD([subQ8])]})])],"derivedFrom":subQ11});}
            var Q62;
            {var subQ3=sQuery(id+"F0.wireOp",EDGE,"E0.left");var subQ5=sQuery(id+"F0.wireOp",EDGE,"E0.top");var subQ6=makeQuery(id+"F0.imprint","INTERSECT",VERTEX,{"derivedFrom":[subQ5,subQ3]});var subQ7=sQuery(id+"F2.wireOp",EDGE,"E6.bottom");var subQ8=makeQuery(id+"F3.opExtrude","SWEPT_FACE",FACE,{"disambiguationData":[OSD([subQ7])]});Q62=makeQuery(id+"F3.boolean.opBoolean","SPLIT",FACE,{"disambiguationData":[TD([makeQuery(id+"F1.opExtrude","SWEPT_FACE",FACE,{"disambiguationData":[OSD([subQ3]),TDD([makeQuery(id+"F0.imprint","IMPRINT",EDGE,{"disambiguationData":[TD([[subQ6,1.0]])],"derivedFrom":subQ3})])]})])],"derivedFrom":subQ8});}
            var Q63;
            {var subQ0=sQuery(id+"F0.wireOp",EDGE,"E5.left");var subQ1=sQuery(id+"F0.wireOp",EDGE,"E5.bottom");var subQ2=makeQuery(id+"F0.imprint","INTERSECT",VERTEX,{"derivedFrom":[subQ1,subQ0]});var subQ7=sQuery(id+"F2.wireOp",EDGE,"E6.bottom");var subQ14=makeQuery(id+"F1.opExtrude","SWEPT_FACE",FACE,{"disambiguationData":[OSD([subQ1]),TDD([makeQuery(id+"F0.imprint","IMPRINT",EDGE,{"disambiguationData":[TD([[subQ2,-1.0]])],"derivedFrom":subQ1})])]});Q63=makeQuery(id+"F5.boolean.opBoolean","SPLIT",FACE,{"disambiguationData":[TD([makeQuery(id+"F3.opExtrude","SWEPT_FACE",FACE,{"disambiguationData":[OSD([subQ7])]})])],"derivedFrom":subQ14});}
            var Q64;
            {var subQ0=sQuery(id+"F2.wireOp",EDGE,"E6.bottom");var subQ3=sQuery(id+"F0.wireOp",EDGE,"E0.left");var subQ5=sQuery(id+"F0.wireOp",EDGE,"E0.top");var subQ6=makeQuery(id+"F0.imprint","INTERSECT",VERTEX,{"derivedFrom":[subQ5,subQ3]});Q64=makeQuery(id+"F3.boolean.opBoolean","SPLIT",FACE,{"disambiguationData":[TD([makeQuery(id+"F3.opExtrude","SWEPT_FACE",FACE,{"disambiguationData":[OSD([subQ0])]})])],"derivedFrom":makeQuery(id+"F1.opExtrude","SWEPT_FACE",FACE,{"disambiguationData":[OSD([subQ3]),TDD([makeQuery(id+"F0.imprint","IMPRINT",EDGE,{"disambiguationData":[TD([[subQ6,1.0]])],"derivedFrom":subQ3})])]})});}
            var Q65;
            {var subQ0=sQuery(id+"F2.wireOp",EDGE,"E6.bottom");var subQ3=sQuery(id+"F0.wireOp",EDGE,"E0.left");var subQ5=sQuery(id+"F0.wireOp",EDGE,"E0.bottom");var subQ6=makeQuery(id+"F0.imprint","INTERSECT",VERTEX,{"derivedFrom":[subQ5,subQ3]});Q65=makeQuery(id+"F3.boolean.opBoolean","SPLIT",FACE,{"disambiguationData":[TD([makeQuery(id+"F3.opExtrude","SWEPT_FACE",FACE,{"disambiguationData":[OSD([subQ0])]})])],"derivedFrom":makeQuery(id+"F1.opExtrude","SWEPT_FACE",FACE,{"disambiguationData":[OSD([subQ3]),TDD([makeQuery(id+"F0.imprint","IMPRINT",EDGE,{"disambiguationData":[TD([[subQ6,-1.0]])],"derivedFrom":subQ3})])]})});}
            var Q66;
            {var subQ3=sQuery(id+"F0.wireOp",EDGE,"E0.left");var subQ5=sQuery(id+"F0.wireOp",EDGE,"E0.bottom");var subQ6=makeQuery(id+"F0.imprint","INTERSECT",VERTEX,{"derivedFrom":[subQ5,subQ3]});var subQ8=sQuery(id+"F2.wireOp",EDGE,"E6.right");var subQ9=makeQuery(id+"F3.opExtrude","SWEPT_FACE",FACE,{"disambiguationData":[OSD([subQ8])]});Q66=makeQuery(id+"F3.boolean.opBoolean","SPLIT",FACE,{"disambiguationData":[TD([makeQuery(id+"F1.opExtrude","SWEPT_FACE",FACE,{"disambiguationData":[OSD([subQ3]),TDD([makeQuery(id+"F0.imprint","IMPRINT",EDGE,{"disambiguationData":[TD([[subQ6,-1.0]])],"derivedFrom":subQ3})])]})])],"derivedFrom":subQ9});}
            var Q67;
            {var subQ3=sQuery(id+"F0.wireOp",EDGE,"E0.left");var subQ5=sQuery(id+"F0.wireOp",EDGE,"E0.top");var subQ6=makeQuery(id+"F0.imprint","INTERSECT",VERTEX,{"derivedFrom":[subQ5,subQ3]});var subQ8=sQuery(id+"F2.wireOp",EDGE,"E6.right");var subQ9=makeQuery(id+"F3.opExtrude","SWEPT_FACE",FACE,{"disambiguationData":[OSD([subQ8])]});Q67=makeQuery(id+"F3.boolean.opBoolean","SPLIT",FACE,{"disambiguationData":[TD([makeQuery(id+"F1.opExtrude","SWEPT_FACE",FACE,{"disambiguationData":[OSD([subQ3]),TDD([makeQuery(id+"F0.imprint","IMPRINT",EDGE,{"disambiguationData":[TD([[subQ6,1.0]])],"derivedFrom":subQ3})])]})])],"derivedFrom":subQ9});}
            var Q68;
            {var subQ0=sQuery(id+"F0.wireOp",EDGE,"E0.left");var subQ1=sQuery(id+"F0.wireOp",EDGE,"E0.top");var subQ2=sQuery(id+"F0.wireOp",EDGE,"E5.right");var subQ4=sQuery(id+"F0.wireOp",EDGE,"E5.bottom");var subQ5=makeQuery(id+"F0.imprint","INTERSECT",VERTEX,{"derivedFrom":[subQ4,subQ2]});var subQ6=makeQuery(id+"F1.opExtrude","SWEPT_FACE",FACE,{"disambiguationData":[OSD([subQ2]),TDD([makeQuery(id+"F0.imprint","IMPRINT",EDGE,{"disambiguationData":[TD([[subQ5,-1.0]])],"derivedFrom":subQ2})])]});Q68=makeQuery(id+"F3.boolean.opBoolean","SPLIT",FACE,{"disambiguationData":[TD([makeQuery(id+"F1.opExtrude","CAP_FACE",FACE,{"disambiguationData":[OSD([sQuery(id+"F0.wireOp",EDGE,"E0.bottom"),subQ1,subQ0,sQuery(id+"F0.wireOp",EDGE,"E0.right"),subQ4,sQuery(id+"F0.wireOp",EDGE,"E5.top"),sQuery(id+"F0.wireOp",EDGE,"E5.left"),subQ2])],"isStart":true})])],"derivedFrom":subQ6});}
            var Q69;
            {var subQ0=sQuery(id+"F0.wireOp",EDGE,"E5.right");var subQ1=sQuery(id+"F0.wireOp",EDGE,"E5.bottom");var subQ2=makeQuery(id+"F0.imprint","INTERSECT",VERTEX,{"derivedFrom":[subQ1,subQ0]});var subQ3=sQuery(id+"F0.wireOp",EDGE,"E0.left");var subQ5=makeQuery(id+"F1.opExtrude","SWEPT_FACE",FACE,{"disambiguationData":[OSD([subQ0]),TDD([makeQuery(id+"F0.imprint","IMPRINT",EDGE,{"disambiguationData":[TD([[subQ2,-1.0]])],"derivedFrom":subQ0})])]});var subQ6=sQuery(id+"F0.wireOp",EDGE,"E0.top");Q69=makeQuery(id+"F3.boolean.opBoolean","SPLIT",FACE,{"disambiguationData":[TD([makeQuery(id+"F1.opExtrude","CAP_FACE",FACE,{"disambiguationData":[OSD([sQuery(id+"F0.wireOp",EDGE,"E0.bottom"),subQ6,subQ3,sQuery(id+"F0.wireOp",EDGE,"E0.right"),subQ1,sQuery(id+"F0.wireOp",EDGE,"E5.top"),sQuery(id+"F0.wireOp",EDGE,"E5.left"),subQ0])],"isStart":false})])],"derivedFrom":subQ5});}
            var Q70;
            {var subQ0=sQuery(id+"F0.wireOp",EDGE,"E5.left");var subQ1=sQuery(id+"F0.wireOp",EDGE,"E5.bottom");var subQ2=makeQuery(id+"F0.imprint","INTERSECT",VERTEX,{"derivedFrom":[subQ1,subQ0]});var subQ5=makeQuery(id+"F1.opExtrude","SWEPT_FACE",FACE,{"disambiguationData":[OSD([subQ0]),TDD([makeQuery(id+"F0.imprint","IMPRINT",EDGE,{"disambiguationData":[TD([[subQ2,-1.0]])],"derivedFrom":subQ0})])]});var subQ9=sQuery(id+"F2.wireOp",EDGE,"E6.right");var subQ11=sQuery(id+"F2.wireOp",EDGE,"E6.top");Q70=makeQuery(id+"F5.boolean.opBoolean","SPLIT",FACE,{"disambiguationData":[TD([makeQuery(id+"F3.opExtrude","SWEPT_FACE",FACE,{"disambiguationData":[OSD([subQ11]),TDD([makeQuery(id+"F2.imprint","IMPRINT",EDGE,{"disambiguationData":[TD([[makeQuery(id+"F2.imprint","INTERSECT",VERTEX,{"derivedFrom":[subQ11,subQ9]}),1.0]])],"derivedFrom":subQ11})])]})])],"derivedFrom":subQ5});}
            var Q71;
            {var subQ0=sQuery(id+"F0.wireOp",EDGE,"E5.left");var subQ1=sQuery(id+"F0.wireOp",EDGE,"E5.bottom");var subQ2=makeQuery(id+"F0.imprint","INTERSECT",VERTEX,{"derivedFrom":[subQ1,subQ0]});var subQ5=makeQuery(id+"F1.opExtrude","SWEPT_FACE",FACE,{"disambiguationData":[OSD([subQ0]),TDD([makeQuery(id+"F0.imprint","IMPRINT",EDGE,{"disambiguationData":[TD([[subQ2,-1.0]])],"derivedFrom":subQ0})])]});var subQ9=sQuery(id+"F2.wireOp",EDGE,"E6.left");var subQ11=sQuery(id+"F2.wireOp",EDGE,"E6.bottom");Q71=makeQuery(id+"F5.boolean.opBoolean","SPLIT",FACE,{"disambiguationData":[TD([makeQuery(id+"F3.opExtrude","SWEPT_FACE",FACE,{"disambiguationData":[OSD([subQ9]),TDD([makeQuery(id+"F2.imprint","IMPRINT",EDGE,{"disambiguationData":[TD([[makeQuery(id+"F2.imprint","INTERSECT",VERTEX,{"derivedFrom":[subQ11,subQ9]}),-1.0]])],"derivedFrom":subQ9})])]})])],"derivedFrom":subQ5});}
            var Q72;
            {var subQ0=sQuery(id+"F0.wireOp",EDGE,"E5.right");var subQ1=sQuery(id+"F0.wireOp",EDGE,"E5.top");var subQ2=makeQuery(id+"F0.imprint","INTERSECT",VERTEX,{"derivedFrom":[subQ1,subQ0]});var subQ5=makeQuery(id+"F1.opExtrude","SWEPT_FACE",FACE,{"disambiguationData":[OSD([subQ0]),TDD([makeQuery(id+"F0.imprint","IMPRINT",EDGE,{"disambiguationData":[TD([[subQ2,1.0]])],"derivedFrom":subQ0})])]});var subQ6=sQuery(id+"F2.wireOp",EDGE,"E6.right");Q72=makeQuery(id+"F5.boolean.opBoolean","SPLIT",FACE,{"disambiguationData":[TD([makeQuery(id+"F3.opExtrude","SWEPT_FACE",FACE,{"disambiguationData":[OSD([subQ6])]})])],"derivedFrom":subQ5});}
            var Q73;
            {var subQ5=sQuery(id+"F2.wireOp",EDGE,"E6.right");var subQ12=sQuery(id+"F4.wireOp",EDGE,"E11.bottom");var subQ17=sQuery(id+"F4.wireOp",EDGE,"E11.left");var subQ18=makeQuery(id+"F5.opExtrude","SWEPT_FACE",FACE,{"disambiguationData":[OSD([subQ12]),TDD([makeQuery(id+"F4.imprint","IMPRINT",EDGE,{"disambiguationData":[TD([[makeQuery(id+"F4.imprint","INTERSECT",VERTEX,{"derivedFrom":[subQ12,subQ17]}),-1.0]])],"derivedFrom":subQ12})])]});Q73=makeQuery(id+"F5.boolean.opBoolean","SPLIT",FACE,{"disambiguationData":[TD([makeQuery(id+"F3.opExtrude","SWEPT_FACE",FACE,{"disambiguationData":[OSD([subQ5])]})])],"derivedFrom":subQ18});}
            var Q74;
            {var subQ3=sQuery(id+"F0.wireOp",EDGE,"E0.bottom");var subQ10=sQuery(id+"F0.wireOp",EDGE,"E0.left");var subQ11=makeQuery(id+"F0.imprint","INTERSECT",VERTEX,{"derivedFrom":[subQ3,subQ10]});var subQ17=sQuery(id+"F4.wireOp",EDGE,"E11.left");var subQ19=makeQuery(id+"F5.opExtrude","SWEPT_FACE",FACE,{"disambiguationData":[OSD([subQ17])]});Q74=makeQuery(id+"F5.boolean.opBoolean","SPLIT",FACE,{"disambiguationData":[TD([makeQuery(id+"F1.opExtrude","SWEPT_FACE",FACE,{"disambiguationData":[OSD([subQ3]),TDD([makeQuery(id+"F0.imprint","IMPRINT",EDGE,{"disambiguationData":[TD([[subQ11,-1.0]])],"derivedFrom":subQ3})])]})])],"derivedFrom":subQ19});}
            var Q75;
            {var subQ3=sQuery(id+"F0.wireOp",EDGE,"E0.bottom");var subQ5=sQuery(id+"F0.wireOp",EDGE,"E0.right");var subQ6=makeQuery(id+"F0.imprint","INTERSECT",VERTEX,{"derivedFrom":[subQ3,subQ5]});var subQ7=makeQuery(id+"F1.opExtrude","SWEPT_FACE",FACE,{"disambiguationData":[OSD([subQ3]),TDD([makeQuery(id+"F0.imprint","IMPRINT",EDGE,{"disambiguationData":[TD([[subQ6,1.0]])],"derivedFrom":subQ3})])]});var subQ17=sQuery(id+"F4.wireOp",EDGE,"E11.left");var subQ18=makeQuery(id+"F5.opExtrude","SWEPT_FACE",FACE,{"disambiguationData":[OSD([subQ17])]});Q75=makeQuery(id+"F5.boolean.opBoolean","SPLIT",FACE,{"disambiguationData":[TD([subQ7])],"derivedFrom":subQ18});}
            var Q76;
            {var subQ0=sQuery(id+"F2.wireOp",EDGE,"E6.bottom");var subQ3=sQuery(id+"F0.wireOp",EDGE,"E0.top");var subQ5=sQuery(id+"F0.wireOp",EDGE,"E0.right");var subQ6=sQuery(id+"F2.wireOp",EDGE,"E6.left");var subQ8=makeQuery(id+"F0.imprint","IMPRINT",EDGE,{"disambiguationData":[TD([[makeQuery(id+"F0.imprint","INTERSECT",VERTEX,{"derivedFrom":[subQ3,subQ5]}),1.0]])],"derivedFrom":subQ3});var subQ9=makeQuery(id+"F3.opExtrude","SWEPT_FACE",FACE,{"disambiguationData":[OSD([subQ6]),TDD([makeQuery(id+"F2.imprint","IMPRINT",EDGE,{"disambiguationData":[TD([[makeQuery(id+"F2.imprint","INTERSECT",VERTEX,{"derivedFrom":[subQ0,subQ6]}),-1.0]])],"derivedFrom":subQ6})])]});Q76=makeQuery(id+"F5.boolean.opBoolean","SPLIT",FACE,{"disambiguationData":[TD([makeQuery(id+"F1.opExtrude","SWEPT_FACE",FACE,{"disambiguationData":[OSD([subQ3]),TDD([subQ8])]})])],"derivedFrom":subQ9});}
            var Q77;
            {var subQ1=sQuery(id+"F0.wireOp",EDGE,"E5.right");var subQ2=sQuery(id+"F0.wireOp",EDGE,"E5.bottom");var subQ5=sQuery(id+"F4.wireOp",EDGE,"E11.left");var subQ6=makeQuery(id+"F5.opExtrude","SWEPT_FACE",FACE,{"disambiguationData":[OSD([subQ5])]});Q77=makeQuery(id+"F5.boolean.opBoolean","SPLIT",FACE,{"disambiguationData":[TD([makeQuery(id+"F1.opExtrude","SWEPT_FACE",FACE,{"disambiguationData":[OSD([subQ2]),TDD([makeQuery(id+"F0.imprint","IMPRINT",EDGE,{"disambiguationData":[TD([[makeQuery(id+"F0.imprint","INTERSECT",VERTEX,{"derivedFrom":[subQ2,subQ1]}),1.0]])],"derivedFrom":subQ2})])]})])],"derivedFrom":subQ6});}
            var Q78;
            {var subQ2=sQuery(id+"F0.wireOp",EDGE,"E0.bottom");var subQ4=sQuery(id+"F0.wireOp",EDGE,"E0.right");var subQ5=sQuery(id+"F2.wireOp",EDGE,"E6.left");var subQ7=sQuery(id+"F2.wireOp",EDGE,"E6.bottom");var subQ10=makeQuery(id+"F3.opExtrude","SWEPT_FACE",FACE,{"disambiguationData":[OSD([subQ5]),TDD([makeQuery(id+"F2.imprint","IMPRINT",EDGE,{"disambiguationData":[TD([[makeQuery(id+"F2.imprint","INTERSECT",VERTEX,{"derivedFrom":[subQ7,subQ5]}),-1.0]])],"derivedFrom":subQ5})])]});Q78=makeQuery(id+"F5.boolean.opBoolean","SPLIT",FACE,{"disambiguationData":[TD([makeQuery(id+"F1.opExtrude","SWEPT_FACE",FACE,{"disambiguationData":[OSD([subQ2]),TDD([makeQuery(id+"F0.imprint","IMPRINT",EDGE,{"disambiguationData":[TD([[makeQuery(id+"F0.imprint","INTERSECT",VERTEX,{"derivedFrom":[subQ2,subQ4]}),1.0]])],"derivedFrom":subQ2})])]})])],"derivedFrom":subQ10});}
            var Q79;
            {var subQ0=sQuery(id+"F0.wireOp",EDGE,"E5.left");var subQ1=sQuery(id+"F0.wireOp",EDGE,"E5.top");var subQ8=sQuery(id+"F4.wireOp",EDGE,"E11.left");var subQ10=makeQuery(id+"F5.opExtrude","SWEPT_FACE",FACE,{"disambiguationData":[OSD([subQ8])]});Q79=makeQuery(id+"F5.boolean.opBoolean","SPLIT",FACE,{"disambiguationData":[TD([makeQuery(id+"F1.opExtrude","SWEPT_FACE",FACE,{"disambiguationData":[OSD([subQ0]),TDD([makeQuery(id+"F0.imprint","IMPRINT",EDGE,{"disambiguationData":[TD([[makeQuery(id+"F0.imprint","INTERSECT",VERTEX,{"derivedFrom":[subQ1,subQ0]}),1.0]])],"derivedFrom":subQ0})])]})])],"derivedFrom":subQ10});}
            var Q80;
            {var subQ0=sQuery(id+"F2.wireOp",EDGE,"E6.bottom");var subQ1=sQuery(id+"F0.wireOp",EDGE,"E0.left");var subQ2=sQuery(id+"F0.wireOp",EDGE,"E0.bottom");var subQ3=makeQuery(id+"F0.imprint","INTERSECT",VERTEX,{"derivedFrom":[subQ2,subQ1]});var subQ5=sQuery(id+"F4.wireOp",EDGE,"E11.bottom");var subQ6=sQuery(id+"F0.wireOp",EDGE,"E0.right");var subQ8=sQuery(id+"F0.wireOp",EDGE,"E5.left");var subQ10=sQuery(id+"F2.wireOp",EDGE,"E6.left");var subQ11=sQuery(id+"F2.wireOp",EDGE,"E6.top");var subQ12=sQuery(id+"F0.wireOp",EDGE,"E0.top");var subQ14=sQuery(id+"F0.wireOp",EDGE,"E5.top");var subQ15=sQuery(id+"F4.wireOp",EDGE,"E11.left");var subQ16=sQuery(id+"F2.wireOp",EDGE,"E6.right");var subQ17=makeQuery(id+"F3.opExtrude","CAP_FACE",FACE,{"disambiguationData":[OSD([subQ12,subQ14,subQ0,subQ11,subQ10,subQ16])],"isStart":false});var subQ18=makeQuery(id+"F1.opExtrude","SWEPT_FACE",FACE,{"disambiguationData":[OSD([subQ2]),TDD([makeQuery(id+"F0.imprint","IMPRINT",EDGE,{"disambiguationData":[TD([[subQ3,-1.0]])],"derivedFrom":subQ2})])]});Q80=makeQuery(id+"F5.boolean.opBoolean","SPLIT",FACE,{"disambiguationData":[TD([subQ18,makeQuery(id+"F1.opExtrude","SWEPT_FACE",FACE,{"disambiguationData":[OSD([subQ1]),TDD([makeQuery(id+"F0.imprint","IMPRINT",EDGE,{"disambiguationData":[TD([[subQ3,-1.0]])],"derivedFrom":subQ1})])]}),makeQuery(id+"F3.opExtrude","SWEPT_FACE",FACE,{"disambiguationData":[OSD([subQ0])]}),subQ17,makeQuery(id+"F3.opExtrude","SWEPT_FACE",FACE,{"disambiguationData":[OSD([subQ16])]}),makeQuery(id+"F5.opExtrude","SWEPT_FACE",FACE,{"disambiguationData":[OSD([subQ5]),TDD([makeQuery(id+"F4.imprint","IMPRINT",EDGE,{"disambiguationData":[TD([[makeQuery(id+"F4.imprint","INTERSECT",VERTEX,{"derivedFrom":[subQ5,subQ15]}),-1.0]])],"derivedFrom":subQ5})])]}),makeQuery(id+"F5.opExtrude","CAP_FACE",FACE,{"disambiguationData":[OSD([subQ12,subQ6,subQ8,subQ11,subQ5,sQuery(id+"F4.wireOp",EDGE,"E11.top"),subQ15,sQuery(id+"F4.wireOp",EDGE,"E11.right")])],"isStart":false}),makeQuery(id+"F5.opExtrude","SWEPT_FACE",FACE,{"disambiguationData":[OSD([subQ15])]})])],"derivedFrom":makeQuery(id+"F3.boolean.opBoolean","MERGE",FACE,{"derivedFrom":[subQ18,subQ17]})});}
            var Q81;
            {var subQ1=sQuery(id+"F0.wireOp",EDGE,"E0.left");var subQ2=sQuery(id+"F0.wireOp",EDGE,"E0.bottom");var subQ3=makeQuery(id+"F0.imprint","INTERSECT",VERTEX,{"derivedFrom":[subQ2,subQ1]});var subQ5=sQuery(id+"F4.wireOp",EDGE,"E11.bottom");var subQ6=sQuery(id+"F0.wireOp",EDGE,"E0.right");var subQ8=sQuery(id+"F0.wireOp",EDGE,"E5.left");var subQ11=sQuery(id+"F2.wireOp",EDGE,"E6.top");var subQ12=sQuery(id+"F0.wireOp",EDGE,"E0.top");var subQ15=sQuery(id+"F4.wireOp",EDGE,"E11.left");Q81=makeQuery(id+"F5.boolean.opBoolean","SPLIT",FACE,{"disambiguationData":[TD([makeQuery(id+"F1.opExtrude","SWEPT_FACE",FACE,{"disambiguationData":[OSD([subQ2]),TDD([makeQuery(id+"F0.imprint","IMPRINT",EDGE,{"disambiguationData":[TD([[subQ3,-1.0]])],"derivedFrom":subQ2})])]})])],"derivedFrom":makeQuery(id+"F5.opExtrude","CAP_FACE",FACE,{"disambiguationData":[OSD([subQ12,subQ6,subQ8,subQ11,subQ5,sQuery(id+"F4.wireOp",EDGE,"E11.top"),subQ15,sQuery(id+"F4.wireOp",EDGE,"E11.right")])],"isStart":false})});}
            var Q82;
            {var subQ0=sQuery(id+"F0.wireOp",EDGE,"E0.left");var subQ1=sQuery(id+"F0.wireOp",EDGE,"E0.bottom");var subQ2=makeQuery(id+"F0.imprint","INTERSECT",VERTEX,{"derivedFrom":[subQ1,subQ0]});var subQ3=sQuery(id+"F0.wireOp",EDGE,"E5.bottom");var subQ4=sQuery(id+"F0.wireOp",EDGE,"E5.left");var subQ5=sQuery(id+"F0.wireOp",EDGE,"E5.top");var subQ6=sQuery(id+"F0.wireOp",EDGE,"E0.right");var subQ7=sQuery(id+"F0.wireOp",EDGE,"E0.top");var subQ9=makeQuery(id+"F1.opExtrude","SWEPT_FACE",FACE,{"disambiguationData":[OSD([subQ1]),TDD([makeQuery(id+"F0.imprint","IMPRINT",EDGE,{"disambiguationData":[TD([[subQ2,-1.0]])],"derivedFrom":subQ1})])]});var subQ10=sQuery(id+"F4.wireOp",EDGE,"E11.left");var subQ11=sQuery(id+"F2.wireOp",EDGE,"E6.bottom");var subQ12=sQuery(id+"F2.wireOp",EDGE,"E6.top");var subQ13=makeQuery(id+"F3.opExtrude","CAP_FACE",FACE,{"disambiguationData":[OSD([subQ7,subQ5,subQ11,subQ12,sQuery(id+"F2.wireOp",EDGE,"E6.left"),sQuery(id+"F2.wireOp",EDGE,"E6.right")])],"isStart":false});Q82=makeQuery(id+"F5.boolean.opBoolean","SPLIT",FACE,{"disambiguationData":[TD([subQ9,makeQuery(id+"F1.opExtrude","CAP_FACE",FACE,{"disambiguationData":[OSD([subQ1,subQ7,subQ0,subQ6,subQ3,subQ5,subQ4,sQuery(id+"F0.wireOp",EDGE,"E5.right")])],"isStart":false}),makeQuery(id+"F1.opExtrude","SWEPT_FACE",FACE,{"disambiguationData":[OSD([subQ0]),TDD([makeQuery(id+"F0.imprint","IMPRINT",EDGE,{"disambiguationData":[TD([[subQ2,-1.0]])],"derivedFrom":subQ0})])]}),makeQuery(id+"F1.opExtrude","SWEPT_FACE",FACE,{"disambiguationData":[OSD([subQ3]),TDD([makeQuery(id+"F0.imprint","IMPRINT",EDGE,{"disambiguationData":[TD([[makeQuery(id+"F0.imprint","INTERSECT",VERTEX,{"derivedFrom":[subQ3,subQ4]}),-1.0]])],"derivedFrom":subQ3})])]}),makeQuery(id+"F3.opExtrude","SWEPT_FACE",FACE,{"disambiguationData":[OSD([subQ11])]}),subQ13,makeQuery(id+"F5.opExtrude","CAP_FACE",FACE,{"disambiguationData":[OSD([subQ7,subQ6,subQ4,subQ12,sQuery(id+"F4.wireOp",EDGE,"E11.bottom"),sQuery(id+"F4.wireOp",EDGE,"E11.top"),subQ10,sQuery(id+"F4.wireOp",EDGE,"E11.right")])],"isStart":false}),makeQuery(id+"F5.opExtrude","SWEPT_FACE",FACE,{"disambiguationData":[OSD([subQ10])]})])],"derivedFrom":makeQuery(id+"F3.boolean.opBoolean","MERGE",FACE,{"derivedFrom":[subQ9,subQ13]})});}
            var Q83;
            {var subQ0=sQuery(id+"F2.wireOp",EDGE,"E6.left");var subQ1=sQuery(id+"F2.wireOp",EDGE,"E6.top");var subQ2=makeQuery(id+"F2.imprint","INTERSECT",VERTEX,{"derivedFrom":[subQ1,subQ0]});var subQ3=sQuery(id+"F0.wireOp",EDGE,"E0.right");var subQ4=sQuery(id+"F0.wireOp",EDGE,"E0.top");var subQ6=makeQuery(id+"F3.opExtrude","SWEPT_FACE",FACE,{"disambiguationData":[OSD([subQ1]),TDD([makeQuery(id+"F2.imprint","IMPRINT",EDGE,{"disambiguationData":[TD([[subQ2,-1.0]])],"derivedFrom":subQ1})])]});var subQ7=makeQuery(id+"F3.opExtrude","CAP_FACE",FACE,{"disambiguationData":[OSD([subQ4,subQ3,subQ1,subQ0])],"isStart":false});var subQ8=sQuery(id+"F4.wireOp",EDGE,"E11.bottom");var subQ9=sQuery(id+"F0.wireOp",EDGE,"E0.bottom");var subQ10=makeQuery(id+"F0.imprint","INTERSECT",VERTEX,{"derivedFrom":[subQ9,subQ3]});var subQ11=sQuery(id+"F0.wireOp",EDGE,"E5.left");var subQ12=makeQuery(id+"F1.opExtrude","SWEPT_FACE",FACE,{"disambiguationData":[OSD([subQ3]),TDD([makeQuery(id+"F0.imprint","IMPRINT",EDGE,{"disambiguationData":[TD([[subQ10,-1.0]])],"derivedFrom":subQ3})])]});var subQ13=makeQuery(id+"F1.opExtrude","SWEPT_FACE",FACE,{"disambiguationData":[OSD([subQ9]),TDD([makeQuery(id+"F0.imprint","IMPRINT",EDGE,{"disambiguationData":[TD([[subQ10,1.0]])],"derivedFrom":subQ9})])]});var subQ14=sQuery(id+"F4.wireOp",EDGE,"E11.left");Q83=makeQuery(id+"F5.boolean.opBoolean","SPLIT",FACE,{"disambiguationData":[TD([subQ13,subQ12,subQ6,subQ7,makeQuery(id+"F3.opExtrude","SWEPT_FACE",FACE,{"disambiguationData":[OSD([subQ0]),TDD([makeQuery(id+"F2.imprint","IMPRINT",EDGE,{"disambiguationData":[TD([[subQ2,1.0]])],"derivedFrom":subQ0})])]}),makeQuery(id+"F5.opExtrude","SWEPT_FACE",FACE,{"disambiguationData":[OSD([subQ8]),TDD([makeQuery(id+"F4.imprint","IMPRINT",EDGE,{"disambiguationData":[TD([[makeQuery(id+"F4.imprint","INTERSECT",VERTEX,{"derivedFrom":[subQ8,subQ14]}),-1.0]])],"derivedFrom":subQ8})])]}),makeQuery(id+"F5.opExtrude","CAP_FACE",FACE,{"disambiguationData":[OSD([subQ4,subQ3,subQ11,subQ1,subQ8,sQuery(id+"F4.wireOp",EDGE,"E11.top"),subQ14,sQuery(id+"F4.wireOp",EDGE,"E11.right")])],"isStart":true}),makeQuery(id+"F5.opExtrude","SWEPT_FACE",FACE,{"disambiguationData":[OSD([subQ14])]})])],"derivedFrom":makeQuery(id+"F3.boolean.opBoolean","MERGE",FACE,{"derivedFrom":[subQ13,subQ7]})});}
            var Q84;
            {var subQ0=sQuery(id+"F0.wireOp",EDGE,"E5.left");var subQ1=sQuery(id+"F0.wireOp",EDGE,"E5.bottom");var subQ2=sQuery(id+"F0.wireOp",EDGE,"E0.bottom");var subQ4=sQuery(id+"F0.wireOp",EDGE,"E0.right");var subQ5=makeQuery(id+"F0.imprint","INTERSECT",VERTEX,{"derivedFrom":[subQ2,subQ4]});var subQ6=makeQuery(id+"F1.opExtrude","SWEPT_FACE",FACE,{"disambiguationData":[OSD([subQ2]),TDD([makeQuery(id+"F0.imprint","IMPRINT",EDGE,{"disambiguationData":[TD([[subQ5,1.0]])],"derivedFrom":subQ2})])]});var subQ7=sQuery(id+"F2.wireOp",EDGE,"E6.right");var subQ8=sQuery(id+"F2.wireOp",EDGE,"E6.left");var subQ9=sQuery(id+"F2.wireOp",EDGE,"E6.top");var subQ10=sQuery(id+"F0.wireOp",EDGE,"E5.top");var subQ11=sQuery(id+"F0.wireOp",EDGE,"E0.top");var subQ12=makeQuery(id+"F1.opExtrude","SWEPT_FACE",FACE,{"disambiguationData":[OSD([subQ4]),TDD([makeQuery(id+"F0.imprint","IMPRINT",EDGE,{"disambiguationData":[TD([[subQ5,-1.0]])],"derivedFrom":subQ4})])]});var subQ13=makeQuery(id+"F1.opExtrude","CAP_FACE",FACE,{"disambiguationData":[OSD([subQ2,subQ11,sQuery(id+"F0.wireOp",EDGE,"E0.left"),subQ4,subQ1,subQ10,subQ0,sQuery(id+"F0.wireOp",EDGE,"E5.right")])],"isStart":true});var subQ14=makeQuery(id+"F3.opExtrude","SWEPT_FACE",FACE,{"disambiguationData":[OSD([subQ9]),TDD([makeQuery(id+"F2.imprint","IMPRINT",EDGE,{"disambiguationData":[TD([[makeQuery(id+"F2.imprint","INTERSECT",VERTEX,{"derivedFrom":[subQ9,subQ8]}),-1.0]])],"derivedFrom":subQ9})])]});var subQ15=makeQuery(id+"F3.opExtrude","CAP_FACE",FACE,{"disambiguationData":[OSD([subQ11,subQ4,subQ9,subQ8])],"isStart":false});var subQ16=sQuery(id+"F4.wireOp",EDGE,"E11.bottom");var subQ17=sQuery(id+"F4.wireOp",EDGE,"E11.left");Q84=makeQuery(id+"F5.boolean.opBoolean","SPLIT",FACE,{"disambiguationData":[TD([subQ13,subQ6,subQ12,makeQuery(id+"F1.opExtrude","SWEPT_FACE",FACE,{"disambiguationData":[OSD([subQ0]),TDD([makeQuery(id+"F0.imprint","IMPRINT",EDGE,{"disambiguationData":[TD([[makeQuery(id+"F0.imprint","INTERSECT",VERTEX,{"derivedFrom":[subQ1,subQ0]}),-1.0]])],"derivedFrom":subQ0})])]}),makeQuery(id+"F3.opExtrude","CAP_FACE",FACE,{"disambiguationData":[OSD([subQ11,subQ10,sQuery(id+"F2.wireOp",EDGE,"E6.bottom"),subQ9,subQ8,subQ7])],"isStart":false}),subQ14,subQ15,makeQuery(id+"F3.opExtrude","SWEPT_FACE",FACE,{"disambiguationData":[OSD([subQ9]),TDD([makeQuery(id+"F2.imprint","IMPRINT",EDGE,{"disambiguationData":[TD([[makeQuery(id+"F2.imprint","INTERSECT",VERTEX,{"derivedFrom":[subQ9,subQ7]}),1.0]])],"derivedFrom":subQ9})])]}),makeQuery(id+"F5.opExtrude","SWEPT_FACE",FACE,{"disambiguationData":[OSD([subQ16]),TDD([makeQuery(id+"F4.imprint","IMPRINT",EDGE,{"disambiguationData":[TD([[makeQuery(id+"F4.imprint","INTERSECT",VERTEX,{"derivedFrom":[subQ16,subQ17]}),-1.0]])],"derivedFrom":subQ16})])]}),makeQuery(id+"F5.opExtrude","CAP_FACE",FACE,{"disambiguationData":[OSD([subQ11,subQ4,subQ0,subQ9,subQ16,sQuery(id+"F4.wireOp",EDGE,"E11.top"),subQ17,sQuery(id+"F4.wireOp",EDGE,"E11.right")])],"isStart":true})])],"derivedFrom":makeQuery(id+"F3.boolean.opBoolean","MERGE",FACE,{"derivedFrom":[subQ6,subQ15]})});}
            var Q85;
            {var subQ0=sQuery(id+"F0.wireOp",EDGE,"E5.left");var subQ1=sQuery(id+"F0.wireOp",EDGE,"E5.bottom");var subQ2=sQuery(id+"F0.wireOp",EDGE,"E0.bottom");var subQ4=sQuery(id+"F0.wireOp",EDGE,"E0.right");var subQ5=makeQuery(id+"F0.imprint","INTERSECT",VERTEX,{"derivedFrom":[subQ2,subQ4]});var subQ6=makeQuery(id+"F1.opExtrude","SWEPT_FACE",FACE,{"disambiguationData":[OSD([subQ2]),TDD([makeQuery(id+"F0.imprint","IMPRINT",EDGE,{"disambiguationData":[TD([[subQ5,1.0]])],"derivedFrom":subQ2})])]});var subQ7=sQuery(id+"F2.wireOp",EDGE,"E6.left");var subQ8=sQuery(id+"F2.wireOp",EDGE,"E6.top");var subQ9=sQuery(id+"F2.wireOp",EDGE,"E6.bottom");var subQ10=sQuery(id+"F0.wireOp",EDGE,"E5.top");var subQ11=sQuery(id+"F0.wireOp",EDGE,"E0.top");var subQ12=makeQuery(id+"F3.opExtrude","CAP_FACE",FACE,{"disambiguationData":[OSD([subQ11,subQ4,subQ8,subQ7])],"isStart":false});var subQ13=sQuery(id+"F4.wireOp",EDGE,"E11.left");Q85=makeQuery(id+"F5.boolean.opBoolean","SPLIT",FACE,{"disambiguationData":[TD([makeQuery(id+"F1.opExtrude","CAP_FACE",FACE,{"disambiguationData":[OSD([subQ2,subQ11,sQuery(id+"F0.wireOp",EDGE,"E0.left"),subQ4,subQ1,subQ10,subQ0,sQuery(id+"F0.wireOp",EDGE,"E5.right")])],"isStart":false}),subQ6,makeQuery(id+"F1.opExtrude","SWEPT_FACE",FACE,{"disambiguationData":[OSD([subQ4]),TDD([makeQuery(id+"F0.imprint","IMPRINT",EDGE,{"disambiguationData":[TD([[subQ5,-1.0]])],"derivedFrom":subQ4})])]}),makeQuery(id+"F1.opExtrude","SWEPT_FACE",FACE,{"disambiguationData":[OSD([subQ0]),TDD([makeQuery(id+"F0.imprint","IMPRINT",EDGE,{"disambiguationData":[TD([[makeQuery(id+"F0.imprint","INTERSECT",VERTEX,{"derivedFrom":[subQ1,subQ0]}),-1.0]])],"derivedFrom":subQ0})])]}),makeQuery(id+"F3.opExtrude","CAP_FACE",FACE,{"disambiguationData":[OSD([subQ11,subQ10,subQ9,subQ8,subQ7,sQuery(id+"F2.wireOp",EDGE,"E6.right")])],"isStart":false}),subQ12,makeQuery(id+"F3.opExtrude","SWEPT_FACE",FACE,{"disambiguationData":[OSD([subQ7]),TDD([makeQuery(id+"F2.imprint","IMPRINT",EDGE,{"disambiguationData":[TD([[makeQuery(id+"F2.imprint","INTERSECT",VERTEX,{"derivedFrom":[subQ9,subQ7]}),-1.0]])],"derivedFrom":subQ7})])]}),makeQuery(id+"F3.opExtrude","SWEPT_FACE",FACE,{"disambiguationData":[OSD([subQ7]),TDD([makeQuery(id+"F2.imprint","IMPRINT",EDGE,{"disambiguationData":[TD([[makeQuery(id+"F2.imprint","INTERSECT",VERTEX,{"derivedFrom":[subQ8,subQ7]}),1.0]])],"derivedFrom":subQ7})])]}),makeQuery(id+"F5.opExtrude","CAP_FACE",FACE,{"disambiguationData":[OSD([subQ11,subQ4,subQ0,subQ8,sQuery(id+"F4.wireOp",EDGE,"E11.bottom"),sQuery(id+"F4.wireOp",EDGE,"E11.top"),subQ13,sQuery(id+"F4.wireOp",EDGE,"E11.right")])],"isStart":true}),makeQuery(id+"F5.opExtrude","SWEPT_FACE",FACE,{"disambiguationData":[OSD([subQ13])]})])],"derivedFrom":makeQuery(id+"F3.boolean.opBoolean","MERGE",FACE,{"derivedFrom":[subQ6,subQ12]})});}
            var Q86;
            {var subQ0=sQuery(id+"F0.wireOp",EDGE,"E5.right");var subQ1=sQuery(id+"F0.wireOp",EDGE,"E5.bottom");var subQ2=makeQuery(id+"F0.imprint","INTERSECT",VERTEX,{"derivedFrom":[subQ1,subQ0]});var subQ3=sQuery(id+"F0.wireOp",EDGE,"E0.left");var subQ5=makeQuery(id+"F1.opExtrude","SWEPT_FACE",FACE,{"disambiguationData":[OSD([subQ1]),TDD([makeQuery(id+"F0.imprint","IMPRINT",EDGE,{"disambiguationData":[TD([[subQ2,1.0]])],"derivedFrom":subQ1})])]});var subQ6=sQuery(id+"F4.wireOp",EDGE,"E11.left");var subQ7=sQuery(id+"F0.wireOp",EDGE,"E0.bottom");var subQ8=makeQuery(id+"F0.imprint","INTERSECT",VERTEX,{"derivedFrom":[subQ7,subQ3]});var subQ9=makeQuery(id+"F1.opExtrude","SWEPT_FACE",FACE,{"disambiguationData":[OSD([subQ3]),TDD([makeQuery(id+"F0.imprint","IMPRINT",EDGE,{"disambiguationData":[TD([[subQ8,-1.0]])],"derivedFrom":subQ3})])]});var subQ10=sQuery(id+"F0.wireOp",EDGE,"E0.top");var subQ11=makeQuery(id+"F0.imprint","INTERSECT",VERTEX,{"derivedFrom":[subQ10,subQ3]});var subQ13=makeQuery(id+"F1.opExtrude","SWEPT_FACE",FACE,{"disambiguationData":[OSD([subQ3]),TDD([makeQuery(id+"F0.imprint","IMPRINT",EDGE,{"disambiguationData":[TD([[subQ11,1.0]])],"derivedFrom":subQ3})])]});var subQ14=sQuery(id+"F0.wireOp",EDGE,"E5.left");var subQ15=sQuery(id+"F0.wireOp",EDGE,"E5.top");var subQ16=sQuery(id+"F0.wireOp",EDGE,"E0.right");var subQ17=makeQuery(id+"F1.opExtrude","CAP_FACE",FACE,{"disambiguationData":[OSD([subQ7,subQ10,subQ3,subQ16,subQ1,subQ15,subQ14,subQ0])],"isStart":false});var subQ18=makeQuery(id+"F1.opExtrude","SWEPT_FACE",FACE,{"disambiguationData":[OSD([subQ0]),TDD([makeQuery(id+"F0.imprint","IMPRINT",EDGE,{"disambiguationData":[TD([[subQ2,-1.0]])],"derivedFrom":subQ0})])]});var subQ19=sQuery(id+"F4.wireOp",EDGE,"E11.top");var subQ20=sQuery(id+"F2.wireOp",EDGE,"E6.top");var subQ21=sQuery(id+"F2.wireOp",EDGE,"E6.bottom");var subQ24=sQuery(id+"F2.wireOp",EDGE,"E6.right");var subQ25=sQuery(id+"F2.wireOp",EDGE,"E6.left");Q86=makeQuery(id+"F5.boolean.opBoolean","SPLIT",FACE,{"disambiguationData":[TD([subQ17,subQ9,subQ13,subQ5,subQ18,makeQuery(id+"F5.opExtrude","CAP_FACE",FACE,{"disambiguationData":[OSD([subQ10,subQ16,subQ14,subQ20,sQuery(id+"F4.wireOp",EDGE,"E11.bottom"),subQ19,subQ6,sQuery(id+"F4.wireOp",EDGE,"E11.right")])],"isStart":false}),makeQuery(id+"F5.opExtrude","SWEPT_FACE",FACE,{"disambiguationData":[OSD([subQ19])]}),makeQuery(id+"F5.opExtrude","SWEPT_FACE",FACE,{"disambiguationData":[OSD([subQ6])]})])],"derivedFrom":makeQuery(id+"F3.boolean.opBoolean","SPLIT",FACE,{"disambiguationData":[TD([makeQuery(id+"F1.opExtrude","SWEPT_FACE",FACE,{"disambiguationData":[OSD([subQ7]),TDD([makeQuery(id+"F0.imprint","IMPRINT",EDGE,{"disambiguationData":[TD([[subQ8,-1.0]])],"derivedFrom":subQ7})])]}),subQ17,makeQuery(id+"F1.opExtrude","SWEPT_FACE",FACE,{"disambiguationData":[OSD([subQ10]),TDD([makeQuery(id+"F0.imprint","IMPRINT",EDGE,{"disambiguationData":[TD([[subQ11,-1.0]])],"derivedFrom":subQ10})])]}),subQ9,subQ13,makeQuery(id+"F1.opExtrude","SWEPT_FACE",FACE,{"disambiguationData":[OSD([subQ1]),TDD([makeQuery(id+"F0.imprint","IMPRINT",EDGE,{"disambiguationData":[TD([[makeQuery(id+"F0.imprint","INTERSECT",VERTEX,{"derivedFrom":[subQ1,subQ14]}),-1.0]])],"derivedFrom":subQ1})])]}),subQ5,subQ18,makeQuery(id+"F1.opExtrude","SWEPT_FACE",FACE,{"disambiguationData":[OSD([subQ0]),TDD([makeQuery(id+"F0.imprint","IMPRINT",EDGE,{"disambiguationData":[TD([[makeQuery(id+"F0.imprint","INTERSECT",VERTEX,{"derivedFrom":[subQ15,subQ0]}),1.0]])],"derivedFrom":subQ0})])]}),makeQuery(id+"F3.opExtrude","SWEPT_FACE",FACE,{"disambiguationData":[OSD([subQ21])]}),makeQuery(id+"F3.opExtrude","CAP_FACE",FACE,{"disambiguationData":[OSD([subQ10,subQ15,subQ21,subQ20,subQ25,subQ24])],"isStart":true}),makeQuery(id+"F3.opExtrude","CAP_FACE",FACE,{"disambiguationData":[OSD([subQ10,subQ15,subQ21,subQ20,subQ25,subQ24])],"isStart":false})])],"derivedFrom":subQ17})});}
            var Q87;
            {var subQ0=sQuery(id+"F2.wireOp",EDGE,"E6.bottom");var subQ1=sQuery(id+"F4.wireOp",EDGE,"E11.right");var subQ2=sQuery(id+"F0.wireOp",EDGE,"E0.left");var subQ3=sQuery(id+"F0.wireOp",EDGE,"E0.top");var subQ4=makeQuery(id+"F0.imprint","INTERSECT",VERTEX,{"derivedFrom":[subQ3,subQ2]});var subQ6=sQuery(id+"F2.wireOp",EDGE,"E6.right");var subQ7=sQuery(id+"F2.wireOp",EDGE,"E6.top");var subQ8=makeQuery(id+"F3.opExtrude","CAP_FACE",FACE,{"disambiguationData":[OSD([subQ3,sQuery(id+"F0.wireOp",EDGE,"E5.top"),subQ0,subQ7,sQuery(id+"F2.wireOp",EDGE,"E6.left"),subQ6])],"isStart":true});var subQ9=makeQuery(id+"F1.opExtrude","SWEPT_FACE",FACE,{"disambiguationData":[OSD([subQ3]),TDD([makeQuery(id+"F0.imprint","IMPRINT",EDGE,{"disambiguationData":[TD([[subQ4,-1.0]])],"derivedFrom":subQ3})])]});var subQ10=sQuery(id+"F4.wireOp",EDGE,"E11.top");Q87=makeQuery(id+"F5.boolean.opBoolean","SPLIT",FACE,{"disambiguationData":[TD([subQ9,makeQuery(id+"F1.opExtrude","SWEPT_FACE",FACE,{"disambiguationData":[OSD([subQ2]),TDD([makeQuery(id+"F0.imprint","IMPRINT",EDGE,{"disambiguationData":[TD([[subQ4,1.0]])],"derivedFrom":subQ2})])]}),makeQuery(id+"F3.opExtrude","SWEPT_FACE",FACE,{"disambiguationData":[OSD([subQ0])]}),subQ8,makeQuery(id+"F3.opExtrude","SWEPT_FACE",FACE,{"disambiguationData":[OSD([subQ6])]}),makeQuery(id+"F5.opExtrude","CAP_FACE",FACE,{"disambiguationData":[OSD([subQ3,sQuery(id+"F0.wireOp",EDGE,"E0.right"),sQuery(id+"F0.wireOp",EDGE,"E5.left"),subQ7,sQuery(id+"F4.wireOp",EDGE,"E11.bottom"),subQ10,sQuery(id+"F4.wireOp",EDGE,"E11.left"),subQ1])],"isStart":false}),makeQuery(id+"F5.opExtrude","SWEPT_FACE",FACE,{"disambiguationData":[OSD([subQ10])]}),makeQuery(id+"F5.opExtrude","SWEPT_FACE",FACE,{"disambiguationData":[OSD([subQ1])]})])],"derivedFrom":makeQuery(id+"F3.boolean.opBoolean","MERGE",FACE,{"derivedFrom":[subQ9,subQ8]})});}
            var Q88;
            {var subQ0=sQuery(id+"F0.wireOp",EDGE,"E0.left");var subQ1=sQuery(id+"F0.wireOp",EDGE,"E0.bottom");var subQ2=makeQuery(id+"F0.imprint","INTERSECT",VERTEX,{"derivedFrom":[subQ1,subQ0]});var subQ3=sQuery(id+"F0.wireOp",EDGE,"E5.bottom");var subQ5=makeQuery(id+"F1.opExtrude","SWEPT_FACE",FACE,{"disambiguationData":[OSD([subQ0]),TDD([makeQuery(id+"F0.imprint","IMPRINT",EDGE,{"disambiguationData":[TD([[subQ2,-1.0]])],"derivedFrom":subQ0})])]});var subQ6=sQuery(id+"F0.wireOp",EDGE,"E5.right");var subQ7=sQuery(id+"F0.wireOp",EDGE,"E5.left");var subQ8=sQuery(id+"F0.wireOp",EDGE,"E5.top");var subQ9=sQuery(id+"F0.wireOp",EDGE,"E0.right");var subQ10=sQuery(id+"F0.wireOp",EDGE,"E0.top");var subQ11=makeQuery(id+"F1.opExtrude","CAP_FACE",FACE,{"disambiguationData":[OSD([subQ1,subQ10,subQ0,subQ9,subQ3,subQ8,subQ7,subQ6])],"isStart":false});var subQ13=makeQuery(id+"F1.opExtrude","SWEPT_FACE",FACE,{"disambiguationData":[OSD([subQ3]),TDD([makeQuery(id+"F0.imprint","IMPRINT",EDGE,{"disambiguationData":[TD([[makeQuery(id+"F0.imprint","INTERSECT",VERTEX,{"derivedFrom":[subQ3,subQ7]}),-1.0]])],"derivedFrom":subQ3})])]});var subQ14=makeQuery(id+"F1.opExtrude","SWEPT_FACE",FACE,{"disambiguationData":[OSD([subQ1]),TDD([makeQuery(id+"F0.imprint","IMPRINT",EDGE,{"disambiguationData":[TD([[subQ2,-1.0]])],"derivedFrom":subQ1})])]});var subQ15=makeQuery(id+"F0.imprint","INTERSECT",VERTEX,{"derivedFrom":[subQ3,subQ6]});var subQ16=makeQuery(id+"F1.opExtrude","SWEPT_FACE",FACE,{"disambiguationData":[OSD([subQ3]),TDD([makeQuery(id+"F0.imprint","IMPRINT",EDGE,{"disambiguationData":[TD([[subQ15,1.0]])],"derivedFrom":subQ3})])]});var subQ17=sQuery(id+"F4.wireOp",EDGE,"E11.left");var subQ18=sQuery(id+"F2.wireOp",EDGE,"E6.bottom");var subQ19=makeQuery(id+"F3.opExtrude","SWEPT_FACE",FACE,{"disambiguationData":[OSD([subQ18])]});var subQ20=sQuery(id+"F2.wireOp",EDGE,"E6.right");var subQ21=sQuery(id+"F2.wireOp",EDGE,"E6.left");var subQ22=sQuery(id+"F2.wireOp",EDGE,"E6.top");var subQ23=makeQuery(id+"F3.opExtrude","CAP_FACE",FACE,{"disambiguationData":[OSD([subQ10,subQ8,subQ18,subQ22,subQ21,subQ20])],"isStart":false});var subQ24=makeQuery(id+"F0.imprint","INTERSECT",VERTEX,{"derivedFrom":[subQ10,subQ0]});Q88=makeQuery(id+"F5.boolean.opBoolean","SPLIT",FACE,{"disambiguationData":[TD([subQ14,subQ11,subQ5,subQ13,subQ16,subQ19,subQ23,makeQuery(id+"F5.opExtrude","CAP_FACE",FACE,{"disambiguationData":[OSD([subQ10,subQ9,subQ7,subQ22,sQuery(id+"F4.wireOp",EDGE,"E11.bottom"),sQuery(id+"F4.wireOp",EDGE,"E11.top"),subQ17,sQuery(id+"F4.wireOp",EDGE,"E11.right")])],"isStart":false}),makeQuery(id+"F5.opExtrude","SWEPT_FACE",FACE,{"disambiguationData":[OSD([subQ17])]})])],"derivedFrom":makeQuery(id+"F3.boolean.opBoolean","SPLIT",FACE,{"disambiguationData":[TD([subQ14,subQ11,makeQuery(id+"F1.opExtrude","SWEPT_FACE",FACE,{"disambiguationData":[OSD([subQ10]),TDD([makeQuery(id+"F0.imprint","IMPRINT",EDGE,{"disambiguationData":[TD([[subQ24,-1.0]])],"derivedFrom":subQ10})])]}),subQ5,makeQuery(id+"F1.opExtrude","SWEPT_FACE",FACE,{"disambiguationData":[OSD([subQ0]),TDD([makeQuery(id+"F0.imprint","IMPRINT",EDGE,{"disambiguationData":[TD([[subQ24,1.0]])],"derivedFrom":subQ0})])]}),subQ13,subQ16,makeQuery(id+"F1.opExtrude","SWEPT_FACE",FACE,{"disambiguationData":[OSD([subQ6]),TDD([makeQuery(id+"F0.imprint","IMPRINT",EDGE,{"disambiguationData":[TD([[subQ15,-1.0]])],"derivedFrom":subQ6})])]}),makeQuery(id+"F1.opExtrude","SWEPT_FACE",FACE,{"disambiguationData":[OSD([subQ6]),TDD([makeQuery(id+"F0.imprint","IMPRINT",EDGE,{"disambiguationData":[TD([[makeQuery(id+"F0.imprint","INTERSECT",VERTEX,{"derivedFrom":[subQ8,subQ6]}),1.0]])],"derivedFrom":subQ6})])]}),subQ19,makeQuery(id+"F3.opExtrude","CAP_FACE",FACE,{"disambiguationData":[OSD([subQ10,subQ8,subQ18,subQ22,subQ21,subQ20])],"isStart":true}),subQ23])],"derivedFrom":subQ11})});}
            var Q89;
            {var subQ0=sQuery(id+"F0.wireOp",EDGE,"E5.right");var subQ1=sQuery(id+"F0.wireOp",EDGE,"E5.bottom");var subQ3=sQuery(id+"F0.wireOp",EDGE,"E0.left");var subQ5=sQuery(id+"F4.wireOp",EDGE,"E11.left");var subQ6=sQuery(id+"F0.wireOp",EDGE,"E0.bottom");var subQ7=sQuery(id+"F0.wireOp",EDGE,"E0.top");var subQ9=sQuery(id+"F0.wireOp",EDGE,"E5.left");var subQ10=sQuery(id+"F0.wireOp",EDGE,"E0.right");var subQ11=sQuery(id+"F4.wireOp",EDGE,"E11.top");Q89=makeQuery(id+"F5.boolean.opBoolean","SPLIT",FACE,{"disambiguationData":[TD([makeQuery(id+"F1.opExtrude","CAP_FACE",FACE,{"disambiguationData":[OSD([subQ6,subQ7,subQ3,subQ10,subQ1,sQuery(id+"F0.wireOp",EDGE,"E5.top"),subQ9,subQ0])],"isStart":false})])],"derivedFrom":makeQuery(id+"F5.opExtrude","CAP_FACE",FACE,{"disambiguationData":[OSD([subQ7,subQ10,subQ9,sQuery(id+"F2.wireOp",EDGE,"E6.top"),sQuery(id+"F4.wireOp",EDGE,"E11.bottom"),subQ11,subQ5,sQuery(id+"F4.wireOp",EDGE,"E11.right")])],"isStart":false})});}
            var Q90;
            {var subQ0=sQuery(id+"F0.wireOp",EDGE,"E5.right");var subQ1=sQuery(id+"F0.wireOp",EDGE,"E5.bottom");var subQ2=makeQuery(id+"F0.imprint","INTERSECT",VERTEX,{"derivedFrom":[subQ1,subQ0]});var subQ3=sQuery(id+"F0.wireOp",EDGE,"E0.left");var subQ5=makeQuery(id+"F1.opExtrude","SWEPT_FACE",FACE,{"disambiguationData":[OSD([subQ0]),TDD([makeQuery(id+"F0.imprint","IMPRINT",EDGE,{"disambiguationData":[TD([[subQ2,-1.0]])],"derivedFrom":subQ0})])]});var subQ6=sQuery(id+"F0.wireOp",EDGE,"E0.top");var subQ7=makeQuery(id+"F0.imprint","INTERSECT",VERTEX,{"derivedFrom":[subQ6,subQ3]});var subQ9=makeQuery(id+"F1.opExtrude","SWEPT_FACE",FACE,{"disambiguationData":[OSD([subQ6]),TDD([makeQuery(id+"F0.imprint","IMPRINT",EDGE,{"disambiguationData":[TD([[subQ7,-1.0]])],"derivedFrom":subQ6})])]});var subQ10=makeQuery(id+"F1.opExtrude","SWEPT_FACE",FACE,{"disambiguationData":[OSD([subQ3]),TDD([makeQuery(id+"F0.imprint","IMPRINT",EDGE,{"disambiguationData":[TD([[subQ7,1.0]])],"derivedFrom":subQ3})])]});var subQ11=sQuery(id+"F0.wireOp",EDGE,"E5.left");var subQ12=sQuery(id+"F0.wireOp",EDGE,"E5.top");var subQ13=sQuery(id+"F0.wireOp",EDGE,"E0.right");var subQ14=sQuery(id+"F0.wireOp",EDGE,"E0.bottom");var subQ15=makeQuery(id+"F1.opExtrude","CAP_FACE",FACE,{"disambiguationData":[OSD([subQ14,subQ6,subQ3,subQ13,subQ1,subQ12,subQ11,subQ0])],"isStart":false});var subQ16=sQuery(id+"F2.wireOp",EDGE,"E6.right");var subQ17=sQuery(id+"F2.wireOp",EDGE,"E6.left");var subQ18=sQuery(id+"F2.wireOp",EDGE,"E6.top");var subQ19=sQuery(id+"F2.wireOp",EDGE,"E6.bottom");var subQ20=makeQuery(id+"F3.opExtrude","CAP_FACE",FACE,{"disambiguationData":[OSD([subQ6,subQ12,subQ19,subQ18,subQ17,subQ16])],"isStart":true});var subQ21=makeQuery(id+"F1.opExtrude","SWEPT_FACE",FACE,{"disambiguationData":[OSD([subQ0]),TDD([makeQuery(id+"F0.imprint","IMPRINT",EDGE,{"disambiguationData":[TD([[makeQuery(id+"F0.imprint","INTERSECT",VERTEX,{"derivedFrom":[subQ12,subQ0]}),1.0]])],"derivedFrom":subQ0})])]});var subQ22=makeQuery(id+"F3.opExtrude","SWEPT_FACE",FACE,{"disambiguationData":[OSD([subQ19])]});var subQ23=sQuery(id+"F4.wireOp",EDGE,"E11.top");var subQ26=makeQuery(id+"F0.imprint","INTERSECT",VERTEX,{"derivedFrom":[subQ14,subQ3]});Q90=makeQuery(id+"F5.boolean.opBoolean","SPLIT",FACE,{"disambiguationData":[TD([subQ15,subQ9,subQ10,subQ5,subQ21,subQ22,subQ20,makeQuery(id+"F5.opExtrude","CAP_FACE",FACE,{"disambiguationData":[OSD([subQ6,subQ13,subQ11,subQ18,sQuery(id+"F4.wireOp",EDGE,"E11.bottom"),subQ23,sQuery(id+"F4.wireOp",EDGE,"E11.left"),sQuery(id+"F4.wireOp",EDGE,"E11.right")])],"isStart":false}),makeQuery(id+"F5.opExtrude","SWEPT_FACE",FACE,{"disambiguationData":[OSD([subQ23])]})])],"derivedFrom":makeQuery(id+"F3.boolean.opBoolean","SPLIT",FACE,{"disambiguationData":[TD([makeQuery(id+"F1.opExtrude","SWEPT_FACE",FACE,{"disambiguationData":[OSD([subQ14]),TDD([makeQuery(id+"F0.imprint","IMPRINT",EDGE,{"disambiguationData":[TD([[subQ26,-1.0]])],"derivedFrom":subQ14})])]}),subQ15,subQ9,makeQuery(id+"F1.opExtrude","SWEPT_FACE",FACE,{"disambiguationData":[OSD([subQ3]),TDD([makeQuery(id+"F0.imprint","IMPRINT",EDGE,{"disambiguationData":[TD([[subQ26,-1.0]])],"derivedFrom":subQ3})])]}),subQ10,makeQuery(id+"F1.opExtrude","SWEPT_FACE",FACE,{"disambiguationData":[OSD([subQ1]),TDD([makeQuery(id+"F0.imprint","IMPRINT",EDGE,{"disambiguationData":[TD([[makeQuery(id+"F0.imprint","INTERSECT",VERTEX,{"derivedFrom":[subQ1,subQ11]}),-1.0]])],"derivedFrom":subQ1})])]}),makeQuery(id+"F1.opExtrude","SWEPT_FACE",FACE,{"disambiguationData":[OSD([subQ1]),TDD([makeQuery(id+"F0.imprint","IMPRINT",EDGE,{"disambiguationData":[TD([[subQ2,1.0]])],"derivedFrom":subQ1})])]}),subQ5,subQ21,subQ22,subQ20,makeQuery(id+"F3.opExtrude","CAP_FACE",FACE,{"disambiguationData":[OSD([subQ6,subQ12,subQ19,subQ18,subQ17,subQ16])],"isStart":false})])],"derivedFrom":subQ15})});}
            var Q91;
            {var subQ0=sQuery(id+"F0.wireOp",EDGE,"E0.left");var subQ1=sQuery(id+"F0.wireOp",EDGE,"E0.top");var subQ2=makeQuery(id+"F0.imprint","INTERSECT",VERTEX,{"derivedFrom":[subQ1,subQ0]});var subQ3=sQuery(id+"F0.wireOp",EDGE,"E5.right");var subQ5=makeQuery(id+"F1.opExtrude","SWEPT_FACE",FACE,{"disambiguationData":[OSD([subQ1]),TDD([makeQuery(id+"F0.imprint","IMPRINT",EDGE,{"disambiguationData":[TD([[subQ2,-1.0]])],"derivedFrom":subQ1})])]});var subQ6=sQuery(id+"F0.wireOp",EDGE,"E5.top");var subQ7=sQuery(id+"F0.wireOp",EDGE,"E5.left");var subQ8=sQuery(id+"F0.wireOp",EDGE,"E0.right");var subQ9=sQuery(id+"F2.wireOp",EDGE,"E6.top");var subQ10=sQuery(id+"F2.wireOp",EDGE,"E6.bottom");var subQ11=makeQuery(id+"F3.opExtrude","CAP_FACE",FACE,{"disambiguationData":[OSD([subQ1,subQ6,subQ10,subQ9,sQuery(id+"F2.wireOp",EDGE,"E6.left"),sQuery(id+"F2.wireOp",EDGE,"E6.right")])],"isStart":true});var subQ12=sQuery(id+"F4.wireOp",EDGE,"E11.top");Q91=makeQuery(id+"F5.boolean.opBoolean","SPLIT",FACE,{"disambiguationData":[TD([makeQuery(id+"F1.opExtrude","CAP_FACE",FACE,{"disambiguationData":[OSD([sQuery(id+"F0.wireOp",EDGE,"E0.bottom"),subQ1,subQ0,subQ8,sQuery(id+"F0.wireOp",EDGE,"E5.bottom"),subQ6,subQ7,subQ3])],"isStart":false}),subQ5,makeQuery(id+"F1.opExtrude","SWEPT_FACE",FACE,{"disambiguationData":[OSD([subQ0]),TDD([makeQuery(id+"F0.imprint","IMPRINT",EDGE,{"disambiguationData":[TD([[subQ2,1.0]])],"derivedFrom":subQ0})])]}),makeQuery(id+"F1.opExtrude","SWEPT_FACE",FACE,{"disambiguationData":[OSD([subQ3]),TDD([makeQuery(id+"F0.imprint","IMPRINT",EDGE,{"disambiguationData":[TD([[makeQuery(id+"F0.imprint","INTERSECT",VERTEX,{"derivedFrom":[subQ6,subQ3]}),1.0]])],"derivedFrom":subQ3})])]}),makeQuery(id+"F3.opExtrude","SWEPT_FACE",FACE,{"disambiguationData":[OSD([subQ10])]}),subQ11,makeQuery(id+"F5.opExtrude","CAP_FACE",FACE,{"disambiguationData":[OSD([subQ1,subQ8,subQ7,subQ9,sQuery(id+"F4.wireOp",EDGE,"E11.bottom"),subQ12,sQuery(id+"F4.wireOp",EDGE,"E11.left"),sQuery(id+"F4.wireOp",EDGE,"E11.right")])],"isStart":false}),makeQuery(id+"F5.opExtrude","SWEPT_FACE",FACE,{"disambiguationData":[OSD([subQ12])]})])],"derivedFrom":makeQuery(id+"F3.boolean.opBoolean","MERGE",FACE,{"derivedFrom":[subQ5,subQ11]})});}
            var Q92;
            {var subQ0=sQuery(id+"F2.wireOp",EDGE,"E6.bottom");var subQ1=makeQuery(id+"F3.opExtrude","SWEPT_FACE",FACE,{"disambiguationData":[OSD([subQ0])]});var subQ2=sQuery(id+"F0.wireOp",EDGE,"E0.left");var subQ3=sQuery(id+"F0.wireOp",EDGE,"E0.top");var subQ6=makeQuery(id+"F1.opExtrude","SWEPT_FACE",FACE,{"disambiguationData":[OSD([subQ3]),TDD([makeQuery(id+"F0.imprint","IMPRINT",EDGE,{"disambiguationData":[TD([[makeQuery(id+"F0.imprint","INTERSECT",VERTEX,{"derivedFrom":[subQ3,subQ2]}),-1.0]])],"derivedFrom":subQ3})])]});var subQ9=sQuery(id+"F0.wireOp",EDGE,"E5.left");var subQ10=sQuery(id+"F0.wireOp",EDGE,"E5.bottom");Q92=makeQuery(id+"F5.boolean.opBoolean","SPLIT",FACE,{"disambiguationData":[TD([subQ6])],"derivedFrom":makeQuery(id+"F3.boolean.opBoolean","SPLIT",FACE,{"disambiguationData":[TD([makeQuery(id+"F1.opExtrude","SWEPT_FACE",FACE,{"disambiguationData":[OSD([subQ10]),TDD([makeQuery(id+"F0.imprint","IMPRINT",EDGE,{"disambiguationData":[TD([[makeQuery(id+"F0.imprint","INTERSECT",VERTEX,{"derivedFrom":[subQ10,subQ9]}),-1.0]])],"derivedFrom":subQ10})])]})])],"derivedFrom":subQ1})});}
            var Q93;
            {var subQ1=sQuery(id+"F0.wireOp",EDGE,"E5.right");var subQ2=sQuery(id+"F0.wireOp",EDGE,"E5.bottom");var subQ11=sQuery(id+"F4.wireOp",EDGE,"E11.top");var subQ12=makeQuery(id+"F5.opExtrude","SWEPT_FACE",FACE,{"disambiguationData":[OSD([subQ11])]});Q93=makeQuery(id+"F5.boolean.opBoolean","SPLIT",FACE,{"disambiguationData":[TD([makeQuery(id+"F1.opExtrude","SWEPT_FACE",FACE,{"disambiguationData":[OSD([subQ1]),TDD([makeQuery(id+"F0.imprint","IMPRINT",EDGE,{"disambiguationData":[TD([[makeQuery(id+"F0.imprint","INTERSECT",VERTEX,{"derivedFrom":[subQ2,subQ1]}),-1.0]])],"derivedFrom":subQ1})])]})])],"derivedFrom":subQ12});}
            var Q94;
            {var subQ0=sQuery(id+"F2.wireOp",EDGE,"E6.bottom");var subQ1=makeQuery(id+"F3.opExtrude","SWEPT_FACE",FACE,{"disambiguationData":[OSD([subQ0])]});var subQ3=sQuery(id+"F0.wireOp",EDGE,"E5.left");var subQ5=sQuery(id+"F0.wireOp",EDGE,"E5.bottom");var subQ7=sQuery(id+"F0.wireOp",EDGE,"E0.left");var subQ9=sQuery(id+"F0.wireOp",EDGE,"E0.bottom");var subQ12=makeQuery(id+"F1.opExtrude","SWEPT_FACE",FACE,{"disambiguationData":[OSD([subQ5]),TDD([makeQuery(id+"F0.imprint","IMPRINT",EDGE,{"disambiguationData":[TD([[makeQuery(id+"F0.imprint","INTERSECT",VERTEX,{"derivedFrom":[subQ5,subQ3]}),-1.0]])],"derivedFrom":subQ5})])]});var subQ13=makeQuery(id+"F1.opExtrude","SWEPT_FACE",FACE,{"disambiguationData":[OSD([subQ9]),TDD([makeQuery(id+"F0.imprint","IMPRINT",EDGE,{"disambiguationData":[TD([[makeQuery(id+"F0.imprint","INTERSECT",VERTEX,{"derivedFrom":[subQ9,subQ7]}),-1.0]])],"derivedFrom":subQ9})])]});Q94=makeQuery(id+"F5.boolean.opBoolean","SPLIT",FACE,{"disambiguationData":[TD([subQ13])],"derivedFrom":makeQuery(id+"F3.boolean.opBoolean","SPLIT",FACE,{"disambiguationData":[TD([subQ12])],"derivedFrom":subQ1})});}
            var Q95;
            {var subQ1=sQuery(id+"F0.wireOp",EDGE,"E5.left");var subQ2=sQuery(id+"F0.wireOp",EDGE,"E5.top");var subQ9=sQuery(id+"F4.wireOp",EDGE,"E11.top");var subQ10=makeQuery(id+"F5.opExtrude","SWEPT_FACE",FACE,{"disambiguationData":[OSD([subQ9])]});Q95=makeQuery(id+"F5.boolean.opBoolean","SPLIT",FACE,{"disambiguationData":[TD([makeQuery(id+"F1.opExtrude","SWEPT_FACE",FACE,{"disambiguationData":[OSD([subQ2]),TDD([makeQuery(id+"F0.imprint","IMPRINT",EDGE,{"disambiguationData":[TD([[makeQuery(id+"F0.imprint","INTERSECT",VERTEX,{"derivedFrom":[subQ2,subQ1]}),-1.0]])],"derivedFrom":subQ2})])]})])],"derivedFrom":subQ10});}
            var Q96;
            Q96=makeQuery(id+"F1.opExtrude","SWEPT_BODY",BODY,{"disambiguationData":[OSD([sQuery(id+"F0.wireOp",EDGE,"E0.bottom"),sQuery(id+"F0.wireOp",EDGE,"E0.top"),sQuery(id+"F0.wireOp",EDGE,"E0.left"),sQuery(id+"F0.wireOp",EDGE,"E0.right"),sQuery(id+"F0.wireOp",EDGE,"E5.bottom"),sQuery(id+"F0.wireOp",EDGE,"E5.top"),sQuery(id+"F0.wireOp",EDGE,"E5.left"),sQuery(id+"F0.wireOp",EDGE,"E5.right")])]});
            shell(context, id + "F8", {"isHollow" : true, "entities" : qUnion([Q0, Q1, Q2, Q3, Q4, Q5, Q6, Q7, Q8, Q9, Q10, Q11, Q12, Q13, Q14, Q15, Q16, Q17, Q18, Q19, Q20, Q21, Q22, Q23, Q24, Q25, Q26, Q27, Q28, Q29, Q30, Q31, Q32, Q33, Q34, Q35, Q36, Q37, Q38, Q39, Q40, Q41, Q42, Q43, Q44, Q45, Q46, Q47, Q48, Q49, Q50, Q51, Q52, Q53, Q54, Q55, Q56, Q57, Q58, Q59, Q60, Q61, Q62, Q63, Q64, Q65, Q66, Q67, Q68, Q69, Q70, Q71, Q72, Q73, Q74, Q75, Q76, Q77, Q78, Q79, Q80, Q81, Q82, Q83, Q84, Q85, Q86, Q87, Q88, Q89, Q90, Q91, Q92, Q93, Q94, Q95]), "parts" : qUnion([Q96]), "thickness" : 9.52 * mm});
        }
        {
            var Q0;
            {var subQ0=sQuery(id+"F0.wireOp",EDGE,"E0.left");var subQ1=sQuery(id+"F0.wireOp",EDGE,"E0.bottom");var subQ2=makeQuery(id+"F0.imprint","INTERSECT",VERTEX,{"derivedFrom":[subQ1,subQ0]});var subQ3=sQuery(id+"F0.wireOp",EDGE,"E5.bottom");var subQ5=makeQuery(id+"F1.opExtrude","SWEPT_FACE",FACE,{"disambiguationData":[OSD([subQ0]),TDD([makeQuery(id+"F0.imprint","IMPRINT",EDGE,{"disambiguationData":[TD([[subQ2,-1.0]])],"derivedFrom":subQ0})])]});var subQ6=sQuery(id+"F0.wireOp",EDGE,"E5.right");var subQ7=sQuery(id+"F0.wireOp",EDGE,"E5.left");var subQ8=sQuery(id+"F0.wireOp",EDGE,"E5.top");var subQ9=sQuery(id+"F0.wireOp",EDGE,"E0.right");var subQ10=sQuery(id+"F0.wireOp",EDGE,"E0.top");var subQ11=makeQuery(id+"F1.opExtrude","CAP_FACE",FACE,{"disambiguationData":[OSD([subQ1,subQ10,subQ0,subQ9,subQ3,subQ8,subQ7,subQ6])],"isStart":true});var subQ13=makeQuery(id+"F1.opExtrude","SWEPT_FACE",FACE,{"disambiguationData":[OSD([subQ3]),TDD([makeQuery(id+"F0.imprint","IMPRINT",EDGE,{"disambiguationData":[TD([[makeQuery(id+"F0.imprint","INTERSECT",VERTEX,{"derivedFrom":[subQ3,subQ7]}),-1.0]])],"derivedFrom":subQ3})])]});var subQ14=sQuery(id+"F2.wireOp",EDGE,"E6.right");var subQ15=makeQuery(id+"F3.opExtrude","SWEPT_FACE",FACE,{"disambiguationData":[OSD([subQ14])]});var subQ16=makeQuery(id+"F1.opExtrude","SWEPT_FACE",FACE,{"disambiguationData":[OSD([subQ1]),TDD([makeQuery(id+"F0.imprint","IMPRINT",EDGE,{"disambiguationData":[TD([[subQ2,-1.0]])],"derivedFrom":subQ1})])]});var subQ17=makeQuery(id+"F0.imprint","INTERSECT",VERTEX,{"derivedFrom":[subQ3,subQ6]});var subQ18=makeQuery(id+"F1.opExtrude","SWEPT_FACE",FACE,{"disambiguationData":[OSD([subQ3]),TDD([makeQuery(id+"F0.imprint","IMPRINT",EDGE,{"disambiguationData":[TD([[subQ17,1.0]])],"derivedFrom":subQ3})])]});var subQ19=sQuery(id+"F2.wireOp",EDGE,"E6.left");var subQ20=sQuery(id+"F2.wireOp",EDGE,"E6.top");var subQ21=sQuery(id+"F2.wireOp",EDGE,"E6.bottom");var subQ22=makeQuery(id+"F3.opExtrude","CAP_FACE",FACE,{"disambiguationData":[OSD([subQ10,subQ8,subQ21,subQ20,subQ19,subQ14])],"isStart":false});var subQ23=sQuery(id+"F4.wireOp",EDGE,"E11.right");var subQ24=sQuery(id+"F4.wireOp",EDGE,"E11.bottom");var subQ28=makeQuery(id+"F0.imprint","INTERSECT",VERTEX,{"derivedFrom":[subQ10,subQ0]});Q0=makeQuery(id+"F5.boolean.opBoolean","SPLIT",FACE,{"disambiguationData":[TD([subQ16,subQ11,subQ5,subQ13,subQ18,subQ22,subQ15,makeQuery(id+"F5.opExtrude","CAP_FACE",FACE,{"disambiguationData":[OSD([subQ10,subQ9,subQ7,subQ20,subQ24,sQuery(id+"F4.wireOp",EDGE,"E11.top"),sQuery(id+"F4.wireOp",EDGE,"E11.left"),subQ23])],"isStart":false}),makeQuery(id+"F5.opExtrude","SWEPT_FACE",FACE,{"disambiguationData":[OSD([subQ24]),TDD([makeQuery(id+"F4.imprint","IMPRINT",EDGE,{"disambiguationData":[TD([[makeQuery(id+"F4.imprint","INTERSECT",VERTEX,{"derivedFrom":[subQ24,subQ23]}),1.0]])],"derivedFrom":subQ24})])]})])],"derivedFrom":makeQuery(id+"F3.boolean.opBoolean","SPLIT",FACE,{"disambiguationData":[TD([subQ16,subQ11,makeQuery(id+"F1.opExtrude","SWEPT_FACE",FACE,{"disambiguationData":[OSD([subQ10]),TDD([makeQuery(id+"F0.imprint","IMPRINT",EDGE,{"disambiguationData":[TD([[subQ28,-1.0]])],"derivedFrom":subQ10})])]}),subQ5,makeQuery(id+"F1.opExtrude","SWEPT_FACE",FACE,{"disambiguationData":[OSD([subQ0]),TDD([makeQuery(id+"F0.imprint","IMPRINT",EDGE,{"disambiguationData":[TD([[subQ28,1.0]])],"derivedFrom":subQ0})])]}),subQ13,subQ18,makeQuery(id+"F1.opExtrude","SWEPT_FACE",FACE,{"disambiguationData":[OSD([subQ6]),TDD([makeQuery(id+"F0.imprint","IMPRINT",EDGE,{"disambiguationData":[TD([[subQ17,-1.0]])],"derivedFrom":subQ6})])]}),makeQuery(id+"F1.opExtrude","SWEPT_FACE",FACE,{"disambiguationData":[OSD([subQ6]),TDD([makeQuery(id+"F0.imprint","IMPRINT",EDGE,{"disambiguationData":[TD([[makeQuery(id+"F0.imprint","INTERSECT",VERTEX,{"derivedFrom":[subQ8,subQ6]}),1.0]])],"derivedFrom":subQ6})])]}),makeQuery(id+"F3.opExtrude","CAP_FACE",FACE,{"disambiguationData":[OSD([subQ10,subQ8,subQ21,subQ20,subQ19,subQ14])],"isStart":true}),subQ22,subQ15])],"derivedFrom":subQ11})});}
            var sketch = newSketch(context, id + "F9", { "sketchPlane" : qUnion([Q0])});
            skLineSegment(sketch, "E18.bottom", {"start": v(21.04, -21.04) * mm, "end": v(50.8, -21.04) * mm});
            skLineSegment(sketch, "E18.top", {"start": v(21.04, -50.8) * mm, "end": v(50.8, -50.8) * mm});
            skLineSegment(sketch, "E18.left", {"start": v(21.04, -21.04) * mm, "end": v(21.04, -50.8) * mm});
            skLineSegment(sketch, "E18.right", {"start": v(50.8, -21.04) * mm, "end": v(50.8, -50.8) * mm});
            skLineSegment(sketch, "E19.0", {"start": v(47.24, -24.6) * mm, "end": v(47.24, -47.24) * mm});
            skLineSegment(sketch, "E19.1", {"start": v(24.6, -24.6) * mm, "end": v(47.24, -24.6) * mm});
            skLineSegment(sketch, "E19.2", {"start": v(24.6, -24.6) * mm, "end": v(24.6, -47.24) * mm});
            skLineSegment(sketch, "E19.3", {"start": v(24.6, -47.24) * mm, "end": v(47.24, -47.24) * mm});
            skSolve(sketch);
        }
        {
            var Q0;
            Q0=makeQuery(id+"F9.imprint","IMPRINT",FACE,{"disambiguationData":[TD([[makeQuery(id+"F9.imprint","IMPRINT",EDGE,{"derivedFrom":sQuery(id+"F9.wireOp",EDGE,"E19.0")}),-1.0]])]});
            extrude(context, id + "F10", {"entities" : qUnion([Q0]), "operationType" : NewBodyOperationType.REMOVE, "oppositeDirection" : true, "depth" : 254 * mm, "offsetDistance" : 25.4 * mm});
        }
        {
            var Q0;
            {var subQ0=sQuery(id+"F0.wireOp",EDGE,"E5.left");var subQ1=sQuery(id+"F0.wireOp",EDGE,"E5.bottom");var subQ2=sQuery(id+"F0.wireOp",EDGE,"E0.bottom");var subQ4=makeQuery(id+"F1.opExtrude","SWEPT_FACE",FACE,{"disambiguationData":[OSD([subQ0]),TDD([makeQuery(id+"F0.imprint","IMPRINT",EDGE,{"disambiguationData":[TD([[makeQuery(id+"F0.imprint","INTERSECT",VERTEX,{"derivedFrom":[subQ1,subQ0]}),-1.0]])],"derivedFrom":subQ0})])]});var subQ5=sQuery(id+"F0.wireOp",EDGE,"E0.right");var subQ6=makeQuery(id+"F0.imprint","INTERSECT",VERTEX,{"derivedFrom":[subQ2,subQ5]});var subQ7=makeQuery(id+"F1.opExtrude","SWEPT_FACE",FACE,{"disambiguationData":[OSD([subQ2]),TDD([makeQuery(id+"F0.imprint","IMPRINT",EDGE,{"disambiguationData":[TD([[subQ6,1.0]])],"derivedFrom":subQ2})])]});var subQ8=sQuery(id+"F2.wireOp",EDGE,"E6.right");var subQ9=sQuery(id+"F2.wireOp",EDGE,"E6.left");var subQ10=sQuery(id+"F2.wireOp",EDGE,"E6.top");var subQ11=sQuery(id+"F2.wireOp",EDGE,"E6.bottom");var subQ12=sQuery(id+"F0.wireOp",EDGE,"E5.top");var subQ13=sQuery(id+"F0.wireOp",EDGE,"E0.top");var subQ14=makeQuery(id+"F3.opExtrude","CAP_FACE",FACE,{"disambiguationData":[OSD([subQ13,subQ12,subQ11,subQ10,subQ9,subQ8])],"isStart":false});var subQ16=makeQuery(id+"F0.imprint","IMPRINT",EDGE,{"disambiguationData":[TD([[subQ6,-1.0]])],"derivedFrom":subQ5});var subQ17=makeQuery(id+"F1.opExtrude","SWEPT_FACE",FACE,{"disambiguationData":[OSD([subQ5]),TDD([subQ16])]});var subQ18=sQuery(id+"F0.wireOp",EDGE,"E5.right");var subQ19=makeQuery(id+"F1.opExtrude","CAP_FACE",FACE,{"disambiguationData":[OSD([subQ2,subQ13,sQuery(id+"F0.wireOp",EDGE,"E0.left"),subQ5,subQ1,subQ12,subQ0,subQ18])],"isStart":true});var subQ20=makeQuery(id+"F0.imprint","INTERSECT",VERTEX,{"derivedFrom":[subQ12,subQ0]});var subQ21=makeQuery(id+"F1.opExtrude","SWEPT_FACE",FACE,{"disambiguationData":[OSD([subQ0]),TDD([makeQuery(id+"F0.imprint","IMPRINT",EDGE,{"disambiguationData":[TD([[subQ20,1.0]])],"derivedFrom":subQ0})])]});var subQ22=makeQuery(id+"F3.opExtrude","CAP_FACE",FACE,{"disambiguationData":[OSD([subQ13,subQ5,subQ10,subQ9])],"isStart":false});var subQ23=makeQuery(id+"F0.imprint","INTERSECT",VERTEX,{"derivedFrom":[subQ13,subQ5]});var subQ25=makeQuery(id+"F0.imprint","IMPRINT",EDGE,{"disambiguationData":[TD([[subQ23,1.0]])],"derivedFrom":subQ13});var subQ26=makeQuery(id+"F3.opExtrude","SWEPT_FACE",FACE,{"disambiguationData":[OSD([subQ10]),TDD([makeQuery(id+"F2.imprint","IMPRINT",EDGE,{"disambiguationData":[TD([[makeQuery(id+"F2.imprint","INTERSECT",VERTEX,{"derivedFrom":[subQ10,subQ8]}),1.0]])],"derivedFrom":subQ10})])]});var subQ27=sQuery(id+"F4.wireOp",EDGE,"E11.right");var subQ28=sQuery(id+"F4.wireOp",EDGE,"E11.bottom");Q0=makeQuery(id+"F5.boolean.opBoolean","SPLIT",FACE,{"disambiguationData":[TD([subQ19,subQ7,subQ17,subQ4,subQ21,subQ14,subQ22,subQ26,makeQuery(id+"F5.opExtrude","CAP_FACE",FACE,{"disambiguationData":[OSD([subQ13,subQ5,subQ0,subQ10,subQ28,sQuery(id+"F4.wireOp",EDGE,"E11.top"),sQuery(id+"F4.wireOp",EDGE,"E11.left"),subQ27])],"isStart":true}),makeQuery(id+"F5.opExtrude","SWEPT_FACE",FACE,{"disambiguationData":[OSD([subQ28]),TDD([makeQuery(id+"F4.imprint","IMPRINT",EDGE,{"disambiguationData":[TD([[makeQuery(id+"F4.imprint","INTERSECT",VERTEX,{"derivedFrom":[subQ28,subQ27]}),1.0]])],"derivedFrom":subQ28})])]})])],"derivedFrom":makeQuery(id+"F3.boolean.opBoolean","SPLIT",FACE,{"disambiguationData":[TD([subQ19,subQ7,makeQuery(id+"F1.opExtrude","SWEPT_FACE",FACE,{"disambiguationData":[OSD([subQ13]),TDD([subQ25])]}),subQ17,makeQuery(id+"F1.opExtrude","SWEPT_FACE",FACE,{"disambiguationData":[OSD([subQ5]),TDD([makeQuery(id+"F0.imprint","IMPRINT",EDGE,{"disambiguationData":[TD([[subQ23,1.0]])],"derivedFrom":subQ5})])]}),makeQuery(id+"F1.opExtrude","SWEPT_FACE",FACE,{"disambiguationData":[OSD([subQ12]),TDD([makeQuery(id+"F0.imprint","IMPRINT",EDGE,{"disambiguationData":[TD([[subQ20,-1.0]])],"derivedFrom":subQ12})])]}),makeQuery(id+"F1.opExtrude","SWEPT_FACE",FACE,{"disambiguationData":[OSD([subQ12]),TDD([makeQuery(id+"F0.imprint","IMPRINT",EDGE,{"disambiguationData":[TD([[makeQuery(id+"F0.imprint","INTERSECT",VERTEX,{"derivedFrom":[subQ12,subQ18]}),1.0]])],"derivedFrom":subQ12})])]}),subQ4,subQ21,makeQuery(id+"F3.opExtrude","CAP_FACE",FACE,{"disambiguationData":[OSD([subQ13,subQ12,subQ11,subQ10,subQ9,subQ8])],"isStart":true}),subQ14,makeQuery(id+"F3.opExtrude","CAP_FACE",FACE,{"disambiguationData":[OSD([subQ13,subQ5,subQ10,subQ9])],"isStart":true}),subQ22,subQ26])],"derivedFrom":subQ19})});}
            var sketch = newSketch(context, id + "F11", { "sketchPlane" : qUnion([Q0])});
            skLineSegment(sketch, "E20.bottom", {"start": v(-50.8, -21.04) * mm, "end": v(-21.04, -21.04) * mm});
            skLineSegment(sketch, "E20.top", {"start": v(-50.8, -50.8) * mm, "end": v(-21.04, -50.8) * mm});
            skLineSegment(sketch, "E20.left", {"start": v(-50.8, -21.04) * mm, "end": v(-50.8, -50.8) * mm});
            skLineSegment(sketch, "E20.right", {"start": v(-21.04, -21.04) * mm, "end": v(-21.04, -50.8) * mm});
            skLineSegment(sketch, "E21.0", {"start": v(-47.24, -24.6) * mm, "end": v(-24.6, -24.6) * mm});
            skLineSegment(sketch, "E21.1", {"start": v(-47.24, -24.6) * mm, "end": v(-47.24, -47.24) * mm});
            skLineSegment(sketch, "E21.2", {"start": v(-47.24, -47.24) * mm, "end": v(-24.6, -47.24) * mm});
            skLineSegment(sketch, "E21.3", {"start": v(-24.6, -24.6) * mm, "end": v(-24.6, -47.24) * mm});
            skSolve(sketch);
        }
        {
            var Q0;
            Q0=makeQuery(id+"F11.imprint","IMPRINT",FACE,{"disambiguationData":[TD([[makeQuery(id+"F11.imprint","IMPRINT",EDGE,{"derivedFrom":sQuery(id+"F11.wireOp",EDGE,"E21.0")}),-1.0]])]});
            extrude(context, id + "F12", {"entities" : qUnion([Q0]), "operationType" : NewBodyOperationType.REMOVE, "oppositeDirection" : true, "depth" : 200.66 * mm, "offsetDistance" : 25.4 * mm});
        }
        {
            var Q0;
            {var subQ0=sQuery(id+"F0.wireOp",EDGE,"E0.left");var subQ1=sQuery(id+"F0.wireOp",EDGE,"E0.top");var subQ2=makeQuery(id+"F0.imprint","INTERSECT",VERTEX,{"derivedFrom":[subQ1,subQ0]});var subQ3=sQuery(id+"F0.wireOp",EDGE,"E5.right");var subQ5=makeQuery(id+"F1.opExtrude","SWEPT_FACE",FACE,{"disambiguationData":[OSD([subQ0]),TDD([makeQuery(id+"F0.imprint","IMPRINT",EDGE,{"disambiguationData":[TD([[subQ2,1.0]])],"derivedFrom":subQ0})])]});var subQ7=makeQuery(id+"F1.opExtrude","SWEPT_FACE",FACE,{"disambiguationData":[OSD([subQ1]),TDD([makeQuery(id+"F0.imprint","IMPRINT",EDGE,{"disambiguationData":[TD([[subQ2,-1.0]])],"derivedFrom":subQ1})])]});var subQ8=sQuery(id+"F0.wireOp",EDGE,"E5.bottom");var subQ9=makeQuery(id+"F0.imprint","INTERSECT",VERTEX,{"derivedFrom":[subQ8,subQ3]});var subQ10=makeQuery(id+"F1.opExtrude","SWEPT_FACE",FACE,{"disambiguationData":[OSD([subQ3]),TDD([makeQuery(id+"F0.imprint","IMPRINT",EDGE,{"disambiguationData":[TD([[subQ9,-1.0]])],"derivedFrom":subQ3})])]});var subQ11=sQuery(id+"F0.wireOp",EDGE,"E5.left");var subQ12=sQuery(id+"F0.wireOp",EDGE,"E5.top");var subQ13=sQuery(id+"F0.wireOp",EDGE,"E0.right");var subQ14=sQuery(id+"F0.wireOp",EDGE,"E0.bottom");var subQ15=makeQuery(id+"F1.opExtrude","CAP_FACE",FACE,{"disambiguationData":[OSD([subQ14,subQ1,subQ0,subQ13,subQ8,subQ12,subQ11,subQ3])],"isStart":true});var subQ16=sQuery(id+"F4.wireOp",EDGE,"E11.right");var subQ17=makeQuery(id+"F1.opExtrude","SWEPT_FACE",FACE,{"disambiguationData":[OSD([subQ3]),TDD([makeQuery(id+"F0.imprint","IMPRINT",EDGE,{"disambiguationData":[TD([[makeQuery(id+"F0.imprint","INTERSECT",VERTEX,{"derivedFrom":[subQ12,subQ3]}),1.0]])],"derivedFrom":subQ3})])]});var subQ18=sQuery(id+"F2.wireOp",EDGE,"E6.right");var subQ19=sQuery(id+"F2.wireOp",EDGE,"E6.left");var subQ20=sQuery(id+"F2.wireOp",EDGE,"E6.top");var subQ21=sQuery(id+"F2.wireOp",EDGE,"E6.bottom");var subQ22=makeQuery(id+"F3.opExtrude","CAP_FACE",FACE,{"disambiguationData":[OSD([subQ1,subQ12,subQ21,subQ20,subQ19,subQ18])],"isStart":true});var subQ23=makeQuery(id+"F3.opExtrude","SWEPT_FACE",FACE,{"disambiguationData":[OSD([subQ18])]});var subQ26=makeQuery(id+"F0.imprint","INTERSECT",VERTEX,{"derivedFrom":[subQ14,subQ0]});Q0=makeQuery(id+"F5.boolean.opBoolean","SPLIT",FACE,{"disambiguationData":[TD([subQ15,subQ7,subQ5,subQ10,subQ17,subQ22,subQ23,makeQuery(id+"F5.opExtrude","CAP_FACE",FACE,{"disambiguationData":[OSD([subQ1,subQ13,subQ11,subQ20,sQuery(id+"F4.wireOp",EDGE,"E11.bottom"),sQuery(id+"F4.wireOp",EDGE,"E11.top"),sQuery(id+"F4.wireOp",EDGE,"E11.left"),subQ16])],"isStart":false}),makeQuery(id+"F5.opExtrude","SWEPT_FACE",FACE,{"disambiguationData":[OSD([subQ16])]})])],"derivedFrom":makeQuery(id+"F3.boolean.opBoolean","SPLIT",FACE,{"disambiguationData":[TD([makeQuery(id+"F1.opExtrude","SWEPT_FACE",FACE,{"disambiguationData":[OSD([subQ14]),TDD([makeQuery(id+"F0.imprint","IMPRINT",EDGE,{"disambiguationData":[TD([[subQ26,-1.0]])],"derivedFrom":subQ14})])]}),subQ15,subQ7,makeQuery(id+"F1.opExtrude","SWEPT_FACE",FACE,{"disambiguationData":[OSD([subQ0]),TDD([makeQuery(id+"F0.imprint","IMPRINT",EDGE,{"disambiguationData":[TD([[subQ26,-1.0]])],"derivedFrom":subQ0})])]}),subQ5,makeQuery(id+"F1.opExtrude","SWEPT_FACE",FACE,{"disambiguationData":[OSD([subQ8]),TDD([makeQuery(id+"F0.imprint","IMPRINT",EDGE,{"disambiguationData":[TD([[makeQuery(id+"F0.imprint","INTERSECT",VERTEX,{"derivedFrom":[subQ8,subQ11]}),-1.0]])],"derivedFrom":subQ8})])]}),makeQuery(id+"F1.opExtrude","SWEPT_FACE",FACE,{"disambiguationData":[OSD([subQ8]),TDD([makeQuery(id+"F0.imprint","IMPRINT",EDGE,{"disambiguationData":[TD([[subQ9,1.0]])],"derivedFrom":subQ8})])]}),subQ10,subQ17,subQ22,makeQuery(id+"F3.opExtrude","CAP_FACE",FACE,{"disambiguationData":[OSD([subQ1,subQ12,subQ21,subQ20,subQ19,subQ18])],"isStart":false}),subQ23])],"derivedFrom":subQ15})});}
            var sketch = newSketch(context, id + "F13", { "sketchPlane" : qUnion([Q0])});
            skLineSegment(sketch, "E22.bottom", {"start": v(21.04, 50.8) * mm, "end": v(50.8, 50.8) * mm});
            skLineSegment(sketch, "E22.top", {"start": v(21.04, 21.04) * mm, "end": v(50.8, 21.04) * mm});
            skLineSegment(sketch, "E22.left", {"start": v(21.04, 50.8) * mm, "end": v(21.04, 21.04) * mm});
            skLineSegment(sketch, "E22.right", {"start": v(50.8, 50.8) * mm, "end": v(50.8, 21.04) * mm});
            skLineSegment(sketch, "E23.0", {"start": v(24.6, 47.24) * mm, "end": v(47.24, 47.24) * mm});
            skLineSegment(sketch, "E23.1", {"start": v(24.6, 47.24) * mm, "end": v(24.6, 24.6) * mm});
            skLineSegment(sketch, "E23.2", {"start": v(24.6, 24.6) * mm, "end": v(47.24, 24.6) * mm});
            skLineSegment(sketch, "E23.3", {"start": v(47.24, 47.24) * mm, "end": v(47.24, 24.6) * mm});
            skSolve(sketch);
        }
        {
            var Q0;
            Q0=makeQuery(id+"F13.imprint","IMPRINT",FACE,{"disambiguationData":[TD([[makeQuery(id+"F13.imprint","IMPRINT",EDGE,{"derivedFrom":sQuery(id+"F13.wireOp",EDGE,"E23.0")}),-1.0]])]});
            extrude(context, id + "F14", {"entities" : qUnion([Q0]), "operationType" : NewBodyOperationType.REMOVE, "oppositeDirection" : true, "depth" : 152.15 * mm, "offsetDistance" : 25.4 * mm});
        }
        {
            var Q0;
            {var subQ0=sQuery(id+"F0.wireOp",EDGE,"E5.left");var subQ1=sQuery(id+"F0.wireOp",EDGE,"E5.top");var subQ2=makeQuery(id+"F0.imprint","INTERSECT",VERTEX,{"derivedFrom":[subQ1,subQ0]});var subQ3=sQuery(id+"F0.wireOp",EDGE,"E0.right");var subQ5=makeQuery(id+"F1.opExtrude","SWEPT_FACE",FACE,{"disambiguationData":[OSD([subQ1]),TDD([makeQuery(id+"F0.imprint","IMPRINT",EDGE,{"disambiguationData":[TD([[subQ2,-1.0]])],"derivedFrom":subQ1})])]});var subQ6=sQuery(id+"F0.wireOp",EDGE,"E5.right");var subQ7=sQuery(id+"F0.wireOp",EDGE,"E5.bottom");var subQ8=sQuery(id+"F0.wireOp",EDGE,"E0.top");var subQ9=sQuery(id+"F0.wireOp",EDGE,"E0.bottom");var subQ10=makeQuery(id+"F1.opExtrude","CAP_FACE",FACE,{"disambiguationData":[OSD([subQ9,subQ8,sQuery(id+"F0.wireOp",EDGE,"E0.left"),subQ3,subQ7,subQ1,subQ0,subQ6])],"isStart":true});var subQ11=sQuery(id+"F4.wireOp",EDGE,"E11.right");var subQ12=makeQuery(id+"F0.imprint","INTERSECT",VERTEX,{"derivedFrom":[subQ8,subQ3]});var subQ13=makeQuery(id+"F1.opExtrude","SWEPT_FACE",FACE,{"disambiguationData":[OSD([subQ3]),TDD([makeQuery(id+"F0.imprint","IMPRINT",EDGE,{"disambiguationData":[TD([[subQ12,1.0]])],"derivedFrom":subQ3})])]});var subQ15=makeQuery(id+"F0.imprint","IMPRINT",EDGE,{"disambiguationData":[TD([[subQ12,1.0]])],"derivedFrom":subQ8});var subQ16=makeQuery(id+"F1.opExtrude","SWEPT_FACE",FACE,{"disambiguationData":[OSD([subQ8]),TDD([subQ15])]});var subQ17=sQuery(id+"F2.wireOp",EDGE,"E6.left");var subQ18=sQuery(id+"F2.wireOp",EDGE,"E6.top");var subQ19=makeQuery(id+"F3.opExtrude","CAP_FACE",FACE,{"disambiguationData":[OSD([subQ8,subQ3,subQ18,subQ17])],"isStart":true});var subQ20=makeQuery(id+"F1.opExtrude","SWEPT_FACE",FACE,{"disambiguationData":[OSD([subQ1]),TDD([makeQuery(id+"F0.imprint","IMPRINT",EDGE,{"disambiguationData":[TD([[makeQuery(id+"F0.imprint","INTERSECT",VERTEX,{"derivedFrom":[subQ1,subQ6]}),1.0]])],"derivedFrom":subQ1})])]});var subQ21=sQuery(id+"F2.wireOp",EDGE,"E6.right");var subQ22=sQuery(id+"F2.wireOp",EDGE,"E6.bottom");var subQ23=makeQuery(id+"F3.opExtrude","CAP_FACE",FACE,{"disambiguationData":[OSD([subQ8,subQ1,subQ22,subQ18,subQ17,subQ21])],"isStart":true});var subQ24=makeQuery(id+"F3.opExtrude","SWEPT_FACE",FACE,{"disambiguationData":[OSD([subQ18]),TDD([makeQuery(id+"F2.imprint","IMPRINT",EDGE,{"disambiguationData":[TD([[makeQuery(id+"F2.imprint","INTERSECT",VERTEX,{"derivedFrom":[subQ18,subQ21]}),1.0]])],"derivedFrom":subQ18})])]});var subQ27=makeQuery(id+"F0.imprint","INTERSECT",VERTEX,{"derivedFrom":[subQ9,subQ3]});Q0=makeQuery(id+"F5.boolean.opBoolean","SPLIT",FACE,{"disambiguationData":[TD([subQ10,subQ16,subQ13,subQ5,subQ20,subQ23,subQ19,subQ24,makeQuery(id+"F5.opExtrude","CAP_FACE",FACE,{"disambiguationData":[OSD([subQ8,subQ3,subQ0,subQ18,sQuery(id+"F4.wireOp",EDGE,"E11.bottom"),sQuery(id+"F4.wireOp",EDGE,"E11.top"),sQuery(id+"F4.wireOp",EDGE,"E11.left"),subQ11])],"isStart":true}),makeQuery(id+"F5.opExtrude","SWEPT_FACE",FACE,{"disambiguationData":[OSD([subQ11])]})])],"derivedFrom":makeQuery(id+"F3.boolean.opBoolean","SPLIT",FACE,{"disambiguationData":[TD([subQ10,makeQuery(id+"F1.opExtrude","SWEPT_FACE",FACE,{"disambiguationData":[OSD([subQ9]),TDD([makeQuery(id+"F0.imprint","IMPRINT",EDGE,{"disambiguationData":[TD([[subQ27,1.0]])],"derivedFrom":subQ9})])]}),subQ16,makeQuery(id+"F1.opExtrude","SWEPT_FACE",FACE,{"disambiguationData":[OSD([subQ3]),TDD([makeQuery(id+"F0.imprint","IMPRINT",EDGE,{"disambiguationData":[TD([[subQ27,-1.0]])],"derivedFrom":subQ3})])]}),subQ13,subQ5,subQ20,makeQuery(id+"F1.opExtrude","SWEPT_FACE",FACE,{"disambiguationData":[OSD([subQ0]),TDD([makeQuery(id+"F0.imprint","IMPRINT",EDGE,{"disambiguationData":[TD([[makeQuery(id+"F0.imprint","INTERSECT",VERTEX,{"derivedFrom":[subQ7,subQ0]}),-1.0]])],"derivedFrom":subQ0})])]}),makeQuery(id+"F1.opExtrude","SWEPT_FACE",FACE,{"disambiguationData":[OSD([subQ0]),TDD([makeQuery(id+"F0.imprint","IMPRINT",EDGE,{"disambiguationData":[TD([[subQ2,1.0]])],"derivedFrom":subQ0})])]}),subQ23,makeQuery(id+"F3.opExtrude","CAP_FACE",FACE,{"disambiguationData":[OSD([subQ8,subQ1,subQ22,subQ18,subQ17,subQ21])],"isStart":false}),subQ19,makeQuery(id+"F3.opExtrude","CAP_FACE",FACE,{"disambiguationData":[OSD([subQ8,subQ3,subQ18,subQ17])],"isStart":false}),subQ24])],"derivedFrom":subQ10})});}
            var sketch = newSketch(context, id + "F15", { "sketchPlane" : qUnion([Q0])});
            skLineSegment(sketch, "E24.bottom", {"start": v(-50.8, 50.8) * mm, "end": v(-21.04, 50.8) * mm});
            skLineSegment(sketch, "E24.top", {"start": v(-50.8, 21.04) * mm, "end": v(-21.04, 21.04) * mm});
            skLineSegment(sketch, "E24.left", {"start": v(-50.8, 50.8) * mm, "end": v(-50.8, 21.04) * mm});
            skLineSegment(sketch, "E24.right", {"start": v(-21.04, 50.8) * mm, "end": v(-21.04, 21.04) * mm});
            skLineSegment(sketch, "E25.0", {"start": v(-47.24, 47.24) * mm, "end": v(-24.6, 47.24) * mm});
            skLineSegment(sketch, "E25.1", {"start": v(-47.24, 47.24) * mm, "end": v(-47.24, 24.6) * mm});
            skLineSegment(sketch, "E25.2", {"start": v(-47.24, 24.6) * mm, "end": v(-24.6, 24.6) * mm});
            skLineSegment(sketch, "E25.3", {"start": v(-24.6, 47.24) * mm, "end": v(-24.6, 24.6) * mm});
            skSolve(sketch);
        }
        {
            var Q0;
            Q0=makeQuery(id+"F15.imprint","IMPRINT",FACE,{"disambiguationData":[TD([[makeQuery(id+"F15.imprint","IMPRINT",EDGE,{"derivedFrom":sQuery(id+"F15.wireOp",EDGE,"E25.0")}),-1.0]])]});
            extrude(context, id + "F16", {"entities" : qUnion([Q0]), "operationType" : NewBodyOperationType.REMOVE, "oppositeDirection" : true, "depth" : 135.13 * mm, "offsetDistance" : 25.4 * mm});
        }
        {
            var Q0;
            {var subQ0=sQuery(id+"F2.wireOp",EDGE,"E6.right");var subQ2=sQuery(id+"F0.wireOp",EDGE,"E0.top");var subQ3=sQuery(id+"F0.wireOp",EDGE,"E0.left");var subQ4=makeQuery(id+"F0.imprint","INTERSECT",VERTEX,{"derivedFrom":[subQ2,subQ3]});Q0=makeQuery(id+"F3.boolean.opBoolean","SPLIT",FACE,{"disambiguationData":[TD([makeQuery(id+"F3.opExtrude","SWEPT_FACE",FACE,{"disambiguationData":[OSD([subQ0])]})])],"derivedFrom":makeQuery(id+"F1.opExtrude","SWEPT_FACE",FACE,{"disambiguationData":[OSD([subQ3]),TDD([makeQuery(id+"F0.imprint","IMPRINT",EDGE,{"disambiguationData":[TD([[subQ4,1.0]])],"derivedFrom":subQ3})])]})});}
            var sketch = newSketch(context, id + "F17", { "sketchPlane" : qUnion([Q0])});
            skLineSegment(sketch, "E26.bottom", {"start": v(-50.8, 29.76) * mm, "end": v(-21.04, 29.76) * mm});
            skLineSegment(sketch, "E26.top", {"start": v(-50.8, 0) * mm, "end": v(-21.04, 0) * mm});
            skLineSegment(sketch, "E26.left", {"start": v(-50.8, 29.76) * mm, "end": v(-50.8, 0) * mm});
            skLineSegment(sketch, "E26.right", {"start": v(-21.04, 29.76) * mm, "end": v(-21.04, 0) * mm});
            skLineSegment(sketch, "E27.0", {"start": v(-47.24, 26.2) * mm, "end": v(-24.6, 26.2) * mm});
            skLineSegment(sketch, "E27.1", {"start": v(-47.24, 26.2) * mm, "end": v(-47.24, 3.56) * mm});
            skLineSegment(sketch, "E27.2", {"start": v(-47.24, 3.56) * mm, "end": v(-24.6, 3.56) * mm});
            skLineSegment(sketch, "E27.3", {"start": v(-24.6, 26.2) * mm, "end": v(-24.6, 3.56) * mm});
            skSolve(sketch);
        }
        {
            var Q0;
            Q0=makeQuery(id+"F17.imprint","IMPRINT",FACE,{"disambiguationData":[TD([[makeQuery(id+"F17.imprint","IMPRINT",EDGE,{"derivedFrom":sQuery(id+"F17.wireOp",EDGE,"E27.0")}),-1.0]])]});
            extrude(context, id + "F18", {"entities" : qUnion([Q0]), "operationType" : NewBodyOperationType.REMOVE, "oppositeDirection" : true, "depth" : 138.68 * mm, "offsetDistance" : 25.4 * mm});
        }
        {
            var Q0;
            {var subQ2=sQuery(id+"F0.wireOp",EDGE,"E0.right");var subQ4=sQuery(id+"F2.wireOp",EDGE,"E6.left");var subQ5=sQuery(id+"F2.wireOp",EDGE,"E6.top");var subQ7=sQuery(id+"F0.wireOp",EDGE,"E0.bottom");var subQ8=makeQuery(id+"F0.imprint","INTERSECT",VERTEX,{"derivedFrom":[subQ7,subQ2]});Q0=makeQuery(id+"F3.boolean.opBoolean","SPLIT",FACE,{"disambiguationData":[TD([makeQuery(id+"F3.opExtrude","SWEPT_FACE",FACE,{"disambiguationData":[OSD([subQ5]),TDD([makeQuery(id+"F2.imprint","IMPRINT",EDGE,{"disambiguationData":[TD([[makeQuery(id+"F2.imprint","INTERSECT",VERTEX,{"derivedFrom":[subQ5,subQ4]}),-1.0]])],"derivedFrom":subQ5})])]})])],"derivedFrom":makeQuery(id+"F1.opExtrude","SWEPT_FACE",FACE,{"disambiguationData":[OSD([subQ2]),TDD([makeQuery(id+"F0.imprint","IMPRINT",EDGE,{"disambiguationData":[TD([[subQ8,-1.0]])],"derivedFrom":subQ2})])]})});}
            var sketch = newSketch(context, id + "F19", { "sketchPlane" : qUnion([Q0])});
            skLineSegment(sketch, "E28.bottom", {"start": v(-50.8, 29.76) * mm, "end": v(-21.04, 29.76) * mm});
            skLineSegment(sketch, "E28.top", {"start": v(-50.8, 0) * mm, "end": v(-21.04, 0) * mm});
            skLineSegment(sketch, "E28.left", {"start": v(-50.8, 29.76) * mm, "end": v(-50.8, 0) * mm});
            skLineSegment(sketch, "E28.right", {"start": v(-21.04, 29.76) * mm, "end": v(-21.04, 0) * mm});
            skLineSegment(sketch, "E29.0", {"start": v(-47.24, 26.2) * mm, "end": v(-24.6, 26.2) * mm});
            skLineSegment(sketch, "E29.1", {"start": v(-47.24, 26.2) * mm, "end": v(-47.24, 3.56) * mm});
            skLineSegment(sketch, "E29.2", {"start": v(-47.24, 3.56) * mm, "end": v(-24.6, 3.56) * mm});
            skLineSegment(sketch, "E29.3", {"start": v(-24.6, 26.2) * mm, "end": v(-24.6, 3.56) * mm});
            skSolve(sketch);
        }
        {
            var Q0;
            Q0=makeQuery(id+"F19.imprint","IMPRINT",FACE,{"disambiguationData":[TD([[makeQuery(id+"F19.imprint","IMPRINT",EDGE,{"derivedFrom":sQuery(id+"F19.wireOp",EDGE,"E29.0")}),-1.0]])]});
            extrude(context, id + "F20", {"entities" : qUnion([Q0]), "operationType" : NewBodyOperationType.REMOVE, "oppositeDirection" : true, "depth" : 103.38 * mm, "offsetDistance" : 25.4 * mm});
        }
        {
            var Q0;
            {var subQ0=sQuery(id+"F2.wireOp",EDGE,"E6.bottom");var subQ3=sQuery(id+"F0.wireOp",EDGE,"E0.left");var subQ5=sQuery(id+"F0.wireOp",EDGE,"E0.top");var subQ6=makeQuery(id+"F0.imprint","INTERSECT",VERTEX,{"derivedFrom":[subQ5,subQ3]});Q0=makeQuery(id+"F3.boolean.opBoolean","SPLIT",FACE,{"disambiguationData":[TD([makeQuery(id+"F3.opExtrude","SWEPT_FACE",FACE,{"disambiguationData":[OSD([subQ0])]})])],"derivedFrom":makeQuery(id+"F1.opExtrude","SWEPT_FACE",FACE,{"disambiguationData":[OSD([subQ3]),TDD([makeQuery(id+"F0.imprint","IMPRINT",EDGE,{"disambiguationData":[TD([[subQ6,1.0]])],"derivedFrom":subQ3})])]})});}
            var sketch = newSketch(context, id + "F21", { "sketchPlane" : qUnion([Q0])});
            skLineSegment(sketch, "E30.bottom", {"start": v(-50.8, 101.6) * mm, "end": v(-21.04, 101.6) * mm});
            skLineSegment(sketch, "E30.top", {"start": v(-50.8, 71.84) * mm, "end": v(-21.04, 71.84) * mm});
            skLineSegment(sketch, "E30.left", {"start": v(-50.8, 101.6) * mm, "end": v(-50.8, 71.84) * mm});
            skLineSegment(sketch, "E30.right", {"start": v(-21.04, 101.6) * mm, "end": v(-21.04, 71.84) * mm});
            skLineSegment(sketch, "E31.0", {"start": v(-47.24, 98.04) * mm, "end": v(-24.6, 98.04) * mm});
            skLineSegment(sketch, "E31.1", {"start": v(-47.24, 98.04) * mm, "end": v(-47.24, 75.4) * mm});
            skLineSegment(sketch, "E31.2", {"start": v(-47.24, 75.4) * mm, "end": v(-24.6, 75.4) * mm});
            skLineSegment(sketch, "E31.3", {"start": v(-24.6, 98.04) * mm, "end": v(-24.6, 75.4) * mm});
            skSolve(sketch);
        }
        {
            var Q0;
            Q0=makeQuery(id+"F21.imprint","IMPRINT",FACE,{"disambiguationData":[TD([[makeQuery(id+"F21.imprint","IMPRINT",EDGE,{"derivedFrom":sQuery(id+"F21.wireOp",EDGE,"E31.0")}),-1.0]])]});
            extrude(context, id + "F22", {"entities" : qUnion([Q0]), "operationType" : NewBodyOperationType.REMOVE, "oppositeDirection" : true, "depth" : 129.03 * mm, "offsetDistance" : 25.4 * mm});
        }
        {
            var Q0;
            {var subQ0=sQuery(id+"F0.wireOp",EDGE,"E5.right");var subQ1=sQuery(id+"F0.wireOp",EDGE,"E5.top");var subQ2=sQuery(id+"F0.wireOp",EDGE,"E0.top");var subQ4=sQuery(id+"F0.wireOp",EDGE,"E5.left");var subQ5=sQuery(id+"F0.wireOp",EDGE,"E0.right");var subQ6=sQuery(id+"F2.wireOp",EDGE,"E6.left");var subQ7=sQuery(id+"F2.wireOp",EDGE,"E6.top");var subQ8=sQuery(id+"F2.wireOp",EDGE,"E6.bottom");var subQ9=makeQuery(id+"F0.imprint","INTERSECT",VERTEX,{"derivedFrom":[subQ2,subQ5]});var subQ10=makeQuery(id+"F0.imprint","IMPRINT",EDGE,{"disambiguationData":[TD([[subQ9,1.0]])],"derivedFrom":subQ2});var subQ11=makeQuery(id+"F1.opExtrude","SWEPT_FACE",FACE,{"disambiguationData":[OSD([subQ2]),TDD([subQ10])]});var subQ12=makeQuery(id+"F3.opExtrude","CAP_FACE",FACE,{"disambiguationData":[OSD([subQ2,subQ5,subQ7,subQ6])],"isStart":true});var subQ13=sQuery(id+"F4.wireOp",EDGE,"E11.top");Q0=makeQuery(id+"F5.boolean.opBoolean","SPLIT",FACE,{"disambiguationData":[TD([makeQuery(id+"F1.opExtrude","CAP_FACE",FACE,{"disambiguationData":[OSD([sQuery(id+"F0.wireOp",EDGE,"E0.bottom"),subQ2,sQuery(id+"F0.wireOp",EDGE,"E0.left"),subQ5,sQuery(id+"F0.wireOp",EDGE,"E5.bottom"),subQ1,subQ4,subQ0])],"isStart":false}),subQ11,makeQuery(id+"F1.opExtrude","SWEPT_FACE",FACE,{"disambiguationData":[OSD([subQ5]),TDD([makeQuery(id+"F0.imprint","IMPRINT",EDGE,{"disambiguationData":[TD([[subQ9,1.0]])],"derivedFrom":subQ5})])]}),makeQuery(id+"F1.opExtrude","SWEPT_FACE",FACE,{"disambiguationData":[OSD([subQ1]),TDD([makeQuery(id+"F0.imprint","IMPRINT",EDGE,{"disambiguationData":[TD([[makeQuery(id+"F0.imprint","INTERSECT",VERTEX,{"derivedFrom":[subQ1,subQ0]}),1.0]])],"derivedFrom":subQ1})])]}),makeQuery(id+"F3.opExtrude","CAP_FACE",FACE,{"disambiguationData":[OSD([subQ2,subQ1,subQ8,subQ7,subQ6,sQuery(id+"F2.wireOp",EDGE,"E6.right")])],"isStart":true}),subQ12,makeQuery(id+"F3.opExtrude","SWEPT_FACE",FACE,{"disambiguationData":[OSD([subQ6]),TDD([makeQuery(id+"F2.imprint","IMPRINT",EDGE,{"disambiguationData":[TD([[makeQuery(id+"F2.imprint","INTERSECT",VERTEX,{"derivedFrom":[subQ8,subQ6]}),-1.0]])],"derivedFrom":subQ6})])]}),makeQuery(id+"F3.opExtrude","SWEPT_FACE",FACE,{"disambiguationData":[OSD([subQ6]),TDD([makeQuery(id+"F2.imprint","IMPRINT",EDGE,{"disambiguationData":[TD([[makeQuery(id+"F2.imprint","INTERSECT",VERTEX,{"derivedFrom":[subQ7,subQ6]}),1.0]])],"derivedFrom":subQ6})])]}),makeQuery(id+"F5.opExtrude","CAP_FACE",FACE,{"disambiguationData":[OSD([subQ2,subQ5,subQ4,subQ7,sQuery(id+"F4.wireOp",EDGE,"E11.bottom"),subQ13,sQuery(id+"F4.wireOp",EDGE,"E11.left"),sQuery(id+"F4.wireOp",EDGE,"E11.right")])],"isStart":true}),makeQuery(id+"F5.opExtrude","SWEPT_FACE",FACE,{"disambiguationData":[OSD([subQ13])]})])],"derivedFrom":makeQuery(id+"F3.boolean.opBoolean","MERGE",FACE,{"derivedFrom":[subQ11,subQ12]})});}
            var sketch = newSketch(context, id + "F23", { "sketchPlane" : qUnion([Q0])});
            skLineSegment(sketch, "E32.bottom", {"start": v(-50.8, 101.6) * mm, "end": v(-21.04, 101.6) * mm});
            skLineSegment(sketch, "E32.top", {"start": v(-50.8, 71.84) * mm, "end": v(-21.04, 71.84) * mm});
            skLineSegment(sketch, "E32.left", {"start": v(-50.8, 101.6) * mm, "end": v(-50.8, 71.84) * mm});
            skLineSegment(sketch, "E32.right", {"start": v(-21.04, 101.6) * mm, "end": v(-21.04, 71.84) * mm});
            skLineSegment(sketch, "E33.0", {"start": v(-47.24, 98.04) * mm, "end": v(-24.6, 98.04) * mm});
            skLineSegment(sketch, "E33.1", {"start": v(-47.24, 98.04) * mm, "end": v(-47.24, 75.4) * mm});
            skLineSegment(sketch, "E33.2", {"start": v(-47.24, 75.4) * mm, "end": v(-24.6, 75.4) * mm});
            skLineSegment(sketch, "E33.3", {"start": v(-24.6, 98.04) * mm, "end": v(-24.6, 75.4) * mm});
            skSolve(sketch);
        }
        {
            var Q0;
            Q0=makeQuery(id+"F23.imprint","IMPRINT",FACE,{"disambiguationData":[TD([[makeQuery(id+"F23.imprint","IMPRINT",EDGE,{"derivedFrom":sQuery(id+"F23.wireOp",EDGE,"E33.0")}),-1.0]])]});
            extrude(context, id + "F24", {"entities" : qUnion([Q0]), "operationType" : NewBodyOperationType.REMOVE, "oppositeDirection" : true, "depth" : 115.06 * mm, "offsetDistance" : 25.4 * mm});
        }
        {
            var Q0;
            {var subQ2=sQuery(id+"F0.wireOp",EDGE,"E0.right");var subQ4=sQuery(id+"F2.wireOp",EDGE,"E6.left");var subQ5=sQuery(id+"F2.wireOp",EDGE,"E6.top");var subQ7=sQuery(id+"F0.wireOp",EDGE,"E0.bottom");var subQ8=makeQuery(id+"F0.imprint","INTERSECT",VERTEX,{"derivedFrom":[subQ7,subQ2]});Q0=makeQuery(id+"F3.boolean.opBoolean","SPLIT",FACE,{"disambiguationData":[TD([makeQuery(id+"F3.opExtrude","SWEPT_FACE",FACE,{"disambiguationData":[OSD([subQ4]),TDD([makeQuery(id+"F2.imprint","IMPRINT",EDGE,{"disambiguationData":[TD([[makeQuery(id+"F2.imprint","INTERSECT",VERTEX,{"derivedFrom":[subQ5,subQ4]}),1.0]])],"derivedFrom":subQ4})])]})])],"derivedFrom":makeQuery(id+"F1.opExtrude","SWEPT_FACE",FACE,{"disambiguationData":[OSD([subQ2]),TDD([makeQuery(id+"F0.imprint","IMPRINT",EDGE,{"disambiguationData":[TD([[subQ8,-1.0]])],"derivedFrom":subQ2})])]})});}
            var sketch = newSketch(context, id + "F25", { "sketchPlane" : qUnion([Q0])});
            skLineSegment(sketch, "E34.bottom", {"start": v(-50.8, 101.6) * mm, "end": v(-21.04, 101.6) * mm});
            skLineSegment(sketch, "E34.top", {"start": v(-50.8, 71.84) * mm, "end": v(-21.04, 71.84) * mm});
            skLineSegment(sketch, "E34.left", {"start": v(-50.8, 101.6) * mm, "end": v(-50.8, 71.84) * mm});
            skLineSegment(sketch, "E34.right", {"start": v(-21.04, 101.6) * mm, "end": v(-21.04, 71.84) * mm});
            skLineSegment(sketch, "E35.0", {"start": v(-47.24, 98.04) * mm, "end": v(-24.6, 98.04) * mm});
            skLineSegment(sketch, "E35.1", {"start": v(-47.24, 98.04) * mm, "end": v(-47.24, 75.4) * mm});
            skLineSegment(sketch, "E35.2", {"start": v(-47.24, 75.4) * mm, "end": v(-24.6, 75.4) * mm});
            skLineSegment(sketch, "E35.3", {"start": v(-24.6, 98.04) * mm, "end": v(-24.6, 75.4) * mm});
            skSolve(sketch);
        }
        {
            var Q0;
            Q0=makeQuery(id+"F25.imprint","IMPRINT",FACE,{"disambiguationData":[TD([[makeQuery(id+"F25.imprint","IMPRINT",EDGE,{"derivedFrom":sQuery(id+"F25.wireOp",EDGE,"E35.0")}),-1.0]])]});
            extrude(context, id + "F26", {"entities" : qUnion([Q0]), "operationType" : NewBodyOperationType.REMOVE, "oppositeDirection" : true, "depth" : 128.52 * mm, "offsetDistance" : 25.4 * mm});
        }
        {
            var Q0;
            {var subQ0=sQuery(id+"F0.wireOp",EDGE,"E5.right");var subQ1=sQuery(id+"F0.wireOp",EDGE,"E5.top");var subQ2=sQuery(id+"F0.wireOp",EDGE,"E0.top");var subQ4=sQuery(id+"F0.wireOp",EDGE,"E0.left");var subQ5=makeQuery(id+"F0.imprint","INTERSECT",VERTEX,{"derivedFrom":[subQ2,subQ4]});var subQ6=makeQuery(id+"F1.opExtrude","SWEPT_FACE",FACE,{"disambiguationData":[OSD([subQ2]),TDD([makeQuery(id+"F0.imprint","IMPRINT",EDGE,{"disambiguationData":[TD([[subQ5,-1.0]])],"derivedFrom":subQ2})])]});var subQ7=sQuery(id+"F0.wireOp",EDGE,"E5.left");var subQ8=sQuery(id+"F0.wireOp",EDGE,"E0.right");var subQ9=sQuery(id+"F4.wireOp",EDGE,"E11.right");var subQ10=sQuery(id+"F2.wireOp",EDGE,"E6.right");var subQ11=sQuery(id+"F2.wireOp",EDGE,"E6.top");var subQ12=makeQuery(id+"F3.opExtrude","CAP_FACE",FACE,{"disambiguationData":[OSD([subQ2,subQ1,sQuery(id+"F2.wireOp",EDGE,"E6.bottom"),subQ11,sQuery(id+"F2.wireOp",EDGE,"E6.left"),subQ10])],"isStart":true});Q0=makeQuery(id+"F5.boolean.opBoolean","SPLIT",FACE,{"disambiguationData":[TD([makeQuery(id+"F1.opExtrude","CAP_FACE",FACE,{"disambiguationData":[OSD([sQuery(id+"F0.wireOp",EDGE,"E0.bottom"),subQ2,subQ4,subQ8,sQuery(id+"F0.wireOp",EDGE,"E5.bottom"),subQ1,subQ7,subQ0])],"isStart":true}),subQ6,makeQuery(id+"F1.opExtrude","SWEPT_FACE",FACE,{"disambiguationData":[OSD([subQ4]),TDD([makeQuery(id+"F0.imprint","IMPRINT",EDGE,{"disambiguationData":[TD([[subQ5,1.0]])],"derivedFrom":subQ4})])]}),makeQuery(id+"F1.opExtrude","SWEPT_FACE",FACE,{"disambiguationData":[OSD([subQ0]),TDD([makeQuery(id+"F0.imprint","IMPRINT",EDGE,{"disambiguationData":[TD([[makeQuery(id+"F0.imprint","INTERSECT",VERTEX,{"derivedFrom":[subQ1,subQ0]}),1.0]])],"derivedFrom":subQ0})])]}),subQ12,makeQuery(id+"F3.opExtrude","SWEPT_FACE",FACE,{"disambiguationData":[OSD([subQ10])]}),makeQuery(id+"F5.opExtrude","CAP_FACE",FACE,{"disambiguationData":[OSD([subQ2,subQ8,subQ7,subQ11,sQuery(id+"F4.wireOp",EDGE,"E11.bottom"),sQuery(id+"F4.wireOp",EDGE,"E11.top"),sQuery(id+"F4.wireOp",EDGE,"E11.left"),subQ9])],"isStart":false}),makeQuery(id+"F5.opExtrude","SWEPT_FACE",FACE,{"disambiguationData":[OSD([subQ9])]})])],"derivedFrom":makeQuery(id+"F3.boolean.opBoolean","MERGE",FACE,{"derivedFrom":[subQ6,subQ12]})});}
            var sketch = newSketch(context, id + "F27", { "sketchPlane" : qUnion([Q0])});
            skLineSegment(sketch, "E36.bottom", {"start": v(21.04, 29.76) * mm, "end": v(50.8, 29.76) * mm});
            skLineSegment(sketch, "E36.top", {"start": v(21.04, 0) * mm, "end": v(50.8, 0) * mm});
            skLineSegment(sketch, "E36.left", {"start": v(21.04, 29.76) * mm, "end": v(21.04, 0) * mm});
            skLineSegment(sketch, "E36.right", {"start": v(50.8, 29.76) * mm, "end": v(50.8, 0) * mm});
            skLineSegment(sketch, "E37.0", {"start": v(47.24, 26.2) * mm, "end": v(47.24, 3.56) * mm});
            skLineSegment(sketch, "E37.1", {"start": v(24.6, 26.2) * mm, "end": v(47.24, 26.2) * mm});
            skLineSegment(sketch, "E37.2", {"start": v(24.6, 26.2) * mm, "end": v(24.6, 3.56) * mm});
            skLineSegment(sketch, "E37.3", {"start": v(24.6, 3.56) * mm, "end": v(47.24, 3.56) * mm});
            skSolve(sketch);
        }
        {
            var Q0;
            Q0=makeQuery(id+"F27.imprint","IMPRINT",FACE,{"disambiguationData":[TD([[makeQuery(id+"F27.imprint","IMPRINT",EDGE,{"derivedFrom":sQuery(id+"F27.wireOp",EDGE,"E37.0")}),-1.0]])]});
            extrude(context, id + "F28", {"entities" : qUnion([Q0]), "operationType" : NewBodyOperationType.REMOVE, "oppositeDirection" : true, "depth" : 137.4 * mm, "offsetDistance" : 25.4 * mm});
        }
        {
            var Q0;
            {var subQ0=sQuery(id+"F0.wireOp",EDGE,"E0.left");var subQ1=sQuery(id+"F0.wireOp",EDGE,"E0.top");var subQ2=makeQuery(id+"F0.imprint","INTERSECT",VERTEX,{"derivedFrom":[subQ1,subQ0]});var subQ3=sQuery(id+"F0.wireOp",EDGE,"E5.right");var subQ5=makeQuery(id+"F1.opExtrude","SWEPT_FACE",FACE,{"disambiguationData":[OSD([subQ1]),TDD([makeQuery(id+"F0.imprint","IMPRINT",EDGE,{"disambiguationData":[TD([[subQ2,-1.0]])],"derivedFrom":subQ1})])]});var subQ6=sQuery(id+"F0.wireOp",EDGE,"E5.top");var subQ7=sQuery(id+"F0.wireOp",EDGE,"E5.left");var subQ8=sQuery(id+"F0.wireOp",EDGE,"E0.right");var subQ9=sQuery(id+"F2.wireOp",EDGE,"E6.top");var subQ10=sQuery(id+"F2.wireOp",EDGE,"E6.bottom");var subQ11=makeQuery(id+"F3.opExtrude","CAP_FACE",FACE,{"disambiguationData":[OSD([subQ1,subQ6,subQ10,subQ9,sQuery(id+"F2.wireOp",EDGE,"E6.left"),sQuery(id+"F2.wireOp",EDGE,"E6.right")])],"isStart":true});var subQ12=sQuery(id+"F4.wireOp",EDGE,"E11.top");Q0=makeQuery(id+"F5.boolean.opBoolean","SPLIT",FACE,{"disambiguationData":[TD([makeQuery(id+"F1.opExtrude","CAP_FACE",FACE,{"disambiguationData":[OSD([sQuery(id+"F0.wireOp",EDGE,"E0.bottom"),subQ1,subQ0,subQ8,sQuery(id+"F0.wireOp",EDGE,"E5.bottom"),subQ6,subQ7,subQ3])],"isStart":false}),subQ5,makeQuery(id+"F1.opExtrude","SWEPT_FACE",FACE,{"disambiguationData":[OSD([subQ0]),TDD([makeQuery(id+"F0.imprint","IMPRINT",EDGE,{"disambiguationData":[TD([[subQ2,1.0]])],"derivedFrom":subQ0})])]}),makeQuery(id+"F1.opExtrude","SWEPT_FACE",FACE,{"disambiguationData":[OSD([subQ3]),TDD([makeQuery(id+"F0.imprint","IMPRINT",EDGE,{"disambiguationData":[TD([[makeQuery(id+"F0.imprint","INTERSECT",VERTEX,{"derivedFrom":[subQ6,subQ3]}),1.0]])],"derivedFrom":subQ3})])]}),makeQuery(id+"F3.opExtrude","SWEPT_FACE",FACE,{"disambiguationData":[OSD([subQ10])]}),subQ11,makeQuery(id+"F5.opExtrude","CAP_FACE",FACE,{"disambiguationData":[OSD([subQ1,subQ8,subQ7,subQ9,sQuery(id+"F4.wireOp",EDGE,"E11.bottom"),subQ12,sQuery(id+"F4.wireOp",EDGE,"E11.left"),sQuery(id+"F4.wireOp",EDGE,"E11.right")])],"isStart":false}),makeQuery(id+"F5.opExtrude","SWEPT_FACE",FACE,{"disambiguationData":[OSD([subQ12])]})])],"derivedFrom":makeQuery(id+"F3.boolean.opBoolean","MERGE",FACE,{"derivedFrom":[subQ5,subQ11]})});}
            var sketch = newSketch(context, id + "F29", { "sketchPlane" : qUnion([Q0])});
            skLineSegment(sketch, "E38.bottom", {"start": v(21.04, 101.6) * mm, "end": v(50.8, 101.6) * mm});
            skLineSegment(sketch, "E38.top", {"start": v(21.04, 71.84) * mm, "end": v(50.8, 71.84) * mm});
            skLineSegment(sketch, "E38.left", {"start": v(21.04, 101.6) * mm, "end": v(21.04, 71.84) * mm});
            skLineSegment(sketch, "E38.right", {"start": v(50.8, 101.6) * mm, "end": v(50.8, 71.84) * mm});
            skLineSegment(sketch, "E39.0", {"start": v(24.6, 98.04) * mm, "end": v(47.24, 98.04) * mm});
            skLineSegment(sketch, "E39.1", {"start": v(24.6, 98.04) * mm, "end": v(24.6, 75.4) * mm});
            skLineSegment(sketch, "E39.2", {"start": v(24.6, 75.4) * mm, "end": v(47.24, 75.4) * mm});
            skLineSegment(sketch, "E39.3", {"start": v(47.24, 98.04) * mm, "end": v(47.24, 75.4) * mm});
            skSolve(sketch);
        }
        {
            var Q0;
            Q0=makeQuery(id+"F29.imprint","IMPRINT",FACE,{"disambiguationData":[TD([[makeQuery(id+"F29.imprint","IMPRINT",EDGE,{"derivedFrom":sQuery(id+"F29.wireOp",EDGE,"E39.0")}),-1.0]])]});
            extrude(context, id + "F30", {"entities" : qUnion([Q0]), "operationType" : NewBodyOperationType.REMOVE, "oppositeDirection" : true, "depth" : 127.76 * mm, "offsetDistance" : 25.4 * mm});
        }
        {
            var Q0;
            {var subQ0=sQuery(id+"F0.wireOp",EDGE,"E5.right");var subQ1=sQuery(id+"F0.wireOp",EDGE,"E5.top");var subQ2=sQuery(id+"F0.wireOp",EDGE,"E0.top");var subQ4=sQuery(id+"F2.wireOp",EDGE,"E6.right");var subQ5=sQuery(id+"F2.wireOp",EDGE,"E6.left");var subQ6=sQuery(id+"F2.wireOp",EDGE,"E6.top");var subQ7=sQuery(id+"F0.wireOp",EDGE,"E0.right");var subQ8=makeQuery(id+"F0.imprint","INTERSECT",VERTEX,{"derivedFrom":[subQ2,subQ7]});var subQ9=makeQuery(id+"F0.imprint","IMPRINT",EDGE,{"disambiguationData":[TD([[subQ8,1.0]])],"derivedFrom":subQ2});var subQ10=makeQuery(id+"F1.opExtrude","SWEPT_FACE",FACE,{"disambiguationData":[OSD([subQ2]),TDD([subQ9])]});var subQ11=makeQuery(id+"F3.opExtrude","CAP_FACE",FACE,{"disambiguationData":[OSD([subQ2,subQ7,subQ6,subQ5])],"isStart":true});var subQ12=sQuery(id+"F0.wireOp",EDGE,"E5.left");var subQ13=sQuery(id+"F4.wireOp",EDGE,"E11.right");Q0=makeQuery(id+"F5.boolean.opBoolean","SPLIT",FACE,{"disambiguationData":[TD([makeQuery(id+"F1.opExtrude","CAP_FACE",FACE,{"disambiguationData":[OSD([sQuery(id+"F0.wireOp",EDGE,"E0.bottom"),subQ2,sQuery(id+"F0.wireOp",EDGE,"E0.left"),subQ7,sQuery(id+"F0.wireOp",EDGE,"E5.bottom"),subQ1,subQ12,subQ0])],"isStart":true}),subQ10,makeQuery(id+"F1.opExtrude","SWEPT_FACE",FACE,{"disambiguationData":[OSD([subQ7]),TDD([makeQuery(id+"F0.imprint","IMPRINT",EDGE,{"disambiguationData":[TD([[subQ8,1.0]])],"derivedFrom":subQ7})])]}),makeQuery(id+"F1.opExtrude","SWEPT_FACE",FACE,{"disambiguationData":[OSD([subQ1]),TDD([makeQuery(id+"F0.imprint","IMPRINT",EDGE,{"disambiguationData":[TD([[makeQuery(id+"F0.imprint","INTERSECT",VERTEX,{"derivedFrom":[subQ1,subQ0]}),1.0]])],"derivedFrom":subQ1})])]}),makeQuery(id+"F3.opExtrude","CAP_FACE",FACE,{"disambiguationData":[OSD([subQ2,subQ1,sQuery(id+"F2.wireOp",EDGE,"E6.bottom"),subQ6,subQ5,subQ4])],"isStart":true}),makeQuery(id+"F3.opExtrude","SWEPT_FACE",FACE,{"disambiguationData":[OSD([subQ6]),TDD([makeQuery(id+"F2.imprint","IMPRINT",EDGE,{"disambiguationData":[TD([[makeQuery(id+"F2.imprint","INTERSECT",VERTEX,{"derivedFrom":[subQ6,subQ5]}),-1.0]])],"derivedFrom":subQ6})])]}),subQ11,makeQuery(id+"F3.opExtrude","SWEPT_FACE",FACE,{"disambiguationData":[OSD([subQ6]),TDD([makeQuery(id+"F2.imprint","IMPRINT",EDGE,{"disambiguationData":[TD([[makeQuery(id+"F2.imprint","INTERSECT",VERTEX,{"derivedFrom":[subQ6,subQ4]}),1.0]])],"derivedFrom":subQ6})])]}),makeQuery(id+"F5.opExtrude","CAP_FACE",FACE,{"disambiguationData":[OSD([subQ2,subQ7,subQ12,subQ6,sQuery(id+"F4.wireOp",EDGE,"E11.bottom"),sQuery(id+"F4.wireOp",EDGE,"E11.top"),sQuery(id+"F4.wireOp",EDGE,"E11.left"),subQ13])],"isStart":true}),makeQuery(id+"F5.opExtrude","SWEPT_FACE",FACE,{"disambiguationData":[OSD([subQ13])]})])],"derivedFrom":makeQuery(id+"F3.boolean.opBoolean","MERGE",FACE,{"derivedFrom":[subQ10,subQ11]})});}
            var sketch = newSketch(context, id + "F31", { "sketchPlane" : qUnion([Q0])});
            skLineSegment(sketch, "E40.bottom", {"start": v(-50.8, 29.76) * mm, "end": v(-21.04, 29.76) * mm});
            skLineSegment(sketch, "E40.top", {"start": v(-50.8, 0) * mm, "end": v(-21.04, 0) * mm});
            skLineSegment(sketch, "E40.left", {"start": v(-50.8, 29.76) * mm, "end": v(-50.8, 0) * mm});
            skLineSegment(sketch, "E40.right", {"start": v(-21.04, 29.76) * mm, "end": v(-21.04, 0) * mm});
            skLineSegment(sketch, "E41.0", {"start": v(-47.24, 26.2) * mm, "end": v(-24.6, 26.2) * mm});
            skLineSegment(sketch, "E41.1", {"start": v(-47.24, 26.2) * mm, "end": v(-47.24, 3.56) * mm});
            skLineSegment(sketch, "E41.2", {"start": v(-47.24, 3.56) * mm, "end": v(-24.6, 3.56) * mm});
            skLineSegment(sketch, "E41.3", {"start": v(-24.6, 26.2) * mm, "end": v(-24.6, 3.56) * mm});
            skSolve(sketch);
        }
        {
            var Q0;
            Q0=makeQuery(id+"F31.imprint","IMPRINT",FACE,{"disambiguationData":[TD([[makeQuery(id+"F31.imprint","IMPRINT",EDGE,{"derivedFrom":sQuery(id+"F31.wireOp",EDGE,"E41.0")}),-1.0]])]});
            extrude(context, id + "F32", {"entities" : qUnion([Q0]), "operationType" : NewBodyOperationType.REMOVE, "oppositeDirection" : true, "depth" : 144.78 * mm, "offsetDistance" : 25.4 * mm});
        }
        {
            var Q0;
            {var subQ0=sQuery(id+"F0.wireOp",EDGE,"E0.left");var subQ1=sQuery(id+"F0.wireOp",EDGE,"E0.top");var subQ2=sQuery(id+"F0.wireOp",EDGE,"E5.right");var subQ4=sQuery(id+"F0.wireOp",EDGE,"E5.bottom");var subQ5=makeQuery(id+"F0.imprint","INTERSECT",VERTEX,{"derivedFrom":[subQ4,subQ2]});var subQ6=makeQuery(id+"F1.opExtrude","SWEPT_FACE",FACE,{"disambiguationData":[OSD([subQ2]),TDD([makeQuery(id+"F0.imprint","IMPRINT",EDGE,{"disambiguationData":[TD([[subQ5,-1.0]])],"derivedFrom":subQ2})])]});Q0=makeQuery(id+"F3.boolean.opBoolean","SPLIT",FACE,{"disambiguationData":[TD([makeQuery(id+"F1.opExtrude","CAP_FACE",FACE,{"disambiguationData":[OSD([sQuery(id+"F0.wireOp",EDGE,"E0.bottom"),subQ1,subQ0,sQuery(id+"F0.wireOp",EDGE,"E0.right"),subQ4,sQuery(id+"F0.wireOp",EDGE,"E5.top"),sQuery(id+"F0.wireOp",EDGE,"E5.left"),subQ2])],"isStart":true})])],"derivedFrom":subQ6});}
            var sketch = newSketch(context, id + "F33", { "sketchPlane" : qUnion([Q0])});
            skLineSegment(sketch, "E42", {"start": v(21.04, 29.76) * mm, "end": v(50.8, 50.8) * mm});
            skLineSegment(sketch, "E43", {"start": v(50.8, 50.8) * mm, "end": v(50.8, 0) * mm});
            skLineSegment(sketch, "E44", {"start": v(50.8, 0) * mm, "end": v(21.04, 0) * mm});
            skLineSegment(sketch, "E45", {"start": v(21.04, 0) * mm, "end": v(21.04, 29.76) * mm});
            skLineSegment(sketch, "E46.0", {"start": v(24.6, 27.92) * mm, "end": v(47.24, 43.93) * mm});
            skLineSegment(sketch, "E46.1", {"start": v(24.6, 3.56) * mm, "end": v(24.6, 27.92) * mm});
            skLineSegment(sketch, "E46.2", {"start": v(47.24, 3.56) * mm, "end": v(24.6, 3.56) * mm});
            skLineSegment(sketch, "E46.3", {"start": v(47.24, 43.93) * mm, "end": v(47.24, 3.56) * mm});
            skSolve(sketch);
        }
        {
            var Q0;
            Q0=makeQuery(id+"F33.imprint","IMPRINT",FACE,{"disambiguationData":[TD([[makeQuery(id+"F33.imprint","IMPRINT",EDGE,{"derivedFrom":sQuery(id+"F33.wireOp",EDGE,"E46.0")}),-1.0]])]});
            extrude(context, id + "F34", {"entities" : qUnion([Q0]), "operationType" : NewBodyOperationType.REMOVE, "oppositeDirection" : true, "depth" : 127.76 * mm, "offsetDistance" : 25.4 * mm});
        }
        {
            var Q0;
            {var subQ0=sQuery(id+"F0.wireOp",EDGE,"E5.left");var subQ1=sQuery(id+"F0.wireOp",EDGE,"E5.top");var subQ2=makeQuery(id+"F0.imprint","INTERSECT",VERTEX,{"derivedFrom":[subQ1,subQ0]});var subQ3=sQuery(id+"F0.wireOp",EDGE,"E0.right");var subQ5=makeQuery(id+"F1.opExtrude","SWEPT_FACE",FACE,{"disambiguationData":[OSD([subQ0]),TDD([makeQuery(id+"F0.imprint","IMPRINT",EDGE,{"disambiguationData":[TD([[subQ2,1.0]])],"derivedFrom":subQ0})])]});var subQ9=sQuery(id+"F0.wireOp",EDGE,"E0.top");var subQ11=sQuery(id+"F0.wireOp",EDGE,"E0.bottom");Q0=makeQuery(id+"F3.boolean.opBoolean","SPLIT",FACE,{"disambiguationData":[TD([makeQuery(id+"F1.opExtrude","CAP_FACE",FACE,{"disambiguationData":[OSD([subQ11,subQ9,sQuery(id+"F0.wireOp",EDGE,"E0.left"),subQ3,sQuery(id+"F0.wireOp",EDGE,"E5.bottom"),subQ1,subQ0,sQuery(id+"F0.wireOp",EDGE,"E5.right")])],"isStart":true})])],"derivedFrom":subQ5});}
            var sketch = newSketch(context, id + "F35", { "sketchPlane" : qUnion([Q0])});
            skLineSegment(sketch, "E47", {"start": v(50.8, 50.8) * mm, "end": v(21.04, 29.76) * mm});
            skLineSegment(sketch, "E48", {"start": v(21.04, 29.76) * mm, "end": v(21.04, 0) * mm});
            skLineSegment(sketch, "E49", {"start": v(21.04, 0) * mm, "end": v(50.8, 0) * mm});
            skLineSegment(sketch, "E50", {"start": v(50.8, 0) * mm, "end": v(50.8, 50.8) * mm});
            skLineSegment(sketch, "E51.0", {"start": v(47.24, 43.93) * mm, "end": v(24.6, 27.92) * mm});
            skLineSegment(sketch, "E51.1", {"start": v(47.24, 3.56) * mm, "end": v(47.24, 43.93) * mm});
            skLineSegment(sketch, "E51.2", {"start": v(24.6, 3.56) * mm, "end": v(47.24, 3.56) * mm});
            skLineSegment(sketch, "E51.3", {"start": v(24.6, 27.92) * mm, "end": v(24.6, 3.56) * mm});
            skSolve(sketch);
        }
        {
            var Q0;
            Q0=makeQuery(id+"F35.imprint","IMPRINT",FACE,{"disambiguationData":[TD([[makeQuery(id+"F35.imprint","IMPRINT",EDGE,{"derivedFrom":sQuery(id+"F35.wireOp",EDGE,"E51.0")}),1.0]])]});
            extrude(context, id + "F36", {"entities" : qUnion([Q0]), "operationType" : NewBodyOperationType.REMOVE, "oppositeDirection" : true, "depth" : 183.64 * mm, "offsetDistance" : 25.4 * mm});
        }
        {
            var Q0;
            {var subQ0=sQuery(id+"F0.wireOp",EDGE,"E5.right");var subQ1=sQuery(id+"F0.wireOp",EDGE,"E5.top");var subQ2=makeQuery(id+"F0.imprint","INTERSECT",VERTEX,{"derivedFrom":[subQ1,subQ0]});var subQ5=makeQuery(id+"F1.opExtrude","SWEPT_FACE",FACE,{"disambiguationData":[OSD([subQ1]),TDD([makeQuery(id+"F0.imprint","IMPRINT",EDGE,{"disambiguationData":[TD([[subQ2,1.0]])],"derivedFrom":subQ1})])]});var subQ6=sQuery(id+"F2.wireOp",EDGE,"E6.right");var subQ8=sQuery(id+"F2.wireOp",EDGE,"E6.top");Q0=makeQuery(id+"F5.boolean.opBoolean","SPLIT",FACE,{"disambiguationData":[TD([makeQuery(id+"F3.opExtrude","SWEPT_FACE",FACE,{"disambiguationData":[OSD([subQ8]),TDD([makeQuery(id+"F2.imprint","IMPRINT",EDGE,{"disambiguationData":[TD([[makeQuery(id+"F2.imprint","INTERSECT",VERTEX,{"derivedFrom":[subQ8,subQ6]}),1.0]])],"derivedFrom":subQ8})])]})])],"derivedFrom":subQ5});}
            var sketch = newSketch(context, id + "F37", { "sketchPlane" : qUnion([Q0])});
            skLineSegment(sketch, "E52", {"start": v(50.8, 50.8) * mm, "end": v(21.04, 29.76) * mm});
            skLineSegment(sketch, "E53", {"start": v(21.04, 29.76) * mm, "end": v(21.04, 0) * mm});
            skLineSegment(sketch, "E54", {"start": v(21.04, 0) * mm, "end": v(50.8, 0) * mm});
            skLineSegment(sketch, "E55", {"start": v(50.8, 0) * mm, "end": v(50.8, 50.8) * mm});
            skLineSegment(sketch, "E56.0", {"start": v(47.24, 43.93) * mm, "end": v(24.6, 27.92) * mm});
            skLineSegment(sketch, "E56.1", {"start": v(47.24, 3.56) * mm, "end": v(47.24, 43.93) * mm});
            skLineSegment(sketch, "E56.2", {"start": v(24.6, 3.56) * mm, "end": v(47.24, 3.56) * mm});
            skLineSegment(sketch, "E56.3", {"start": v(24.6, 27.92) * mm, "end": v(24.6, 3.56) * mm});
            skSolve(sketch);
        }
        {
            var Q0;
            Q0=makeQuery(id+"F37.imprint","IMPRINT",FACE,{"disambiguationData":[TD([[makeQuery(id+"F37.imprint","IMPRINT",EDGE,{"derivedFrom":sQuery(id+"F37.wireOp",EDGE,"E56.0")}),1.0]])]});
            extrude(context, id + "F38", {"entities" : qUnion([Q0]), "operationType" : NewBodyOperationType.REMOVE, "oppositeDirection" : true, "depth" : 158.5 * mm, "offsetDistance" : 25.4 * mm});
        }
        {
            var Q0;
            {var subQ3=sQuery(id+"F0.wireOp",EDGE,"E0.top");var subQ5=sQuery(id+"F0.wireOp",EDGE,"E0.right");var subQ6=makeQuery(id+"F0.imprint","INTERSECT",VERTEX,{"derivedFrom":[subQ3,subQ5]});var subQ9=sQuery(id+"F4.wireOp",EDGE,"E11.right");var subQ11=makeQuery(id+"F5.opExtrude","SWEPT_FACE",FACE,{"disambiguationData":[OSD([subQ9])]});Q0=makeQuery(id+"F5.boolean.opBoolean","SPLIT",FACE,{"disambiguationData":[TD([makeQuery(id+"F1.opExtrude","SWEPT_FACE",FACE,{"disambiguationData":[OSD([subQ3]),TDD([makeQuery(id+"F0.imprint","IMPRINT",EDGE,{"disambiguationData":[TD([[subQ6,1.0]])],"derivedFrom":subQ3})])]})])],"derivedFrom":subQ11});}
            var sketch = newSketch(context, id + "F39", { "sketchPlane" : qUnion([Q0])});
            skLineSegment(sketch, "E57", {"start": v(0, 86.72) * mm, "end": v(-21.04, 56.96) * mm});
            skLineSegment(sketch, "E58", {"start": v(-21.04, 56.96) * mm, "end": v(-50.8, 56.96) * mm});
            skLineSegment(sketch, "E59", {"start": v(-50.8, 56.96) * mm, "end": v(-50.8, 86.72) * mm});
            skLineSegment(sketch, "E60", {"start": v(-50.8, 86.72) * mm, "end": v(0, 86.72) * mm});
            skLineSegment(sketch, "E61.0", {"start": v(-47.24, 83.17) * mm, "end": v(-6.87, 83.17) * mm});
            skLineSegment(sketch, "E61.1", {"start": v(-47.24, 60.52) * mm, "end": v(-47.24, 83.17) * mm});
            skLineSegment(sketch, "E61.2", {"start": v(-22.88, 60.52) * mm, "end": v(-47.24, 60.52) * mm});
            skLineSegment(sketch, "E61.3", {"start": v(-6.87, 83.17) * mm, "end": v(-22.88, 60.52) * mm});
            skSolve(sketch);
        }
        {
            var Q0;
            Q0=makeQuery(id+"F39.imprint","IMPRINT",FACE,{"disambiguationData":[TD([[makeQuery(id+"F39.imprint","IMPRINT",EDGE,{"derivedFrom":sQuery(id+"F39.wireOp",EDGE,"E61.0")}),-1.0]])]});
            extrude(context, id + "F40", {"entities" : qUnion([Q0]), "operationType" : NewBodyOperationType.REMOVE, "oppositeDirection" : true, "depth" : 174.5 * mm, "offsetDistance" : 25.4 * mm});
        }
        {
            var Q0;
            {var subQ3=sQuery(id+"F0.wireOp",EDGE,"E0.top");var subQ5=sQuery(id+"F0.wireOp",EDGE,"E0.right");var subQ6=makeQuery(id+"F0.imprint","INTERSECT",VERTEX,{"derivedFrom":[subQ3,subQ5]});var subQ10=sQuery(id+"F4.wireOp",EDGE,"E11.top");var subQ11=makeQuery(id+"F5.opExtrude","SWEPT_FACE",FACE,{"disambiguationData":[OSD([subQ10])]});Q0=makeQuery(id+"F5.boolean.opBoolean","SPLIT",FACE,{"disambiguationData":[TD([makeQuery(id+"F1.opExtrude","SWEPT_FACE",FACE,{"disambiguationData":[OSD([subQ3]),TDD([makeQuery(id+"F0.imprint","IMPRINT",EDGE,{"disambiguationData":[TD([[subQ6,1.0]])],"derivedFrom":subQ3})])]})])],"derivedFrom":subQ11});}
            var sketch = newSketch(context, id + "F41", { "sketchPlane" : qUnion([Q0])});
            skLineSegment(sketch, "E62", {"start": v(-50.8, 14.88) * mm, "end": v(-50.8, -14.88) * mm});
            skLineSegment(sketch, "E63", {"start": v(-50.8, -14.88) * mm, "end": v(0, -14.88) * mm});
            skLineSegment(sketch, "E64", {"start": v(0, -14.88) * mm, "end": v(-21.04, 14.88) * mm});
            skLineSegment(sketch, "E65", {"start": v(-21.04, 14.88) * mm, "end": v(-50.8, 14.88) * mm});
            skLineSegment(sketch, "E66.0", {"start": v(-22.88, 11.32) * mm, "end": v(-47.24, 11.32) * mm});
            skLineSegment(sketch, "E66.1", {"start": v(-6.87, -11.32) * mm, "end": v(-22.88, 11.32) * mm});
            skLineSegment(sketch, "E66.2", {"start": v(-47.24, -11.32) * mm, "end": v(-6.87, -11.32) * mm});
            skLineSegment(sketch, "E66.3", {"start": v(-47.24, 11.32) * mm, "end": v(-47.24, -11.32) * mm});
            skSolve(sketch);
        }
        {
            var Q0;
            Q0=makeQuery(id+"F41.imprint","IMPRINT",FACE,{"disambiguationData":[TD([[makeQuery(id+"F41.imprint","IMPRINT",EDGE,{"derivedFrom":sQuery(id+"F41.wireOp",EDGE,"E66.0")}),1.0]])]});
            extrude(context, id + "F42", {"entities" : qUnion([Q0]), "operationType" : NewBodyOperationType.REMOVE, "oppositeDirection" : true, "depth" : 196.6 * mm, "offsetDistance" : 25.4 * mm});
        }
        {
            var Q0;
            {var subQ3=sQuery(id+"F0.wireOp",EDGE,"E0.top");var subQ7=sQuery(id+"F0.wireOp",EDGE,"E0.left");var subQ8=makeQuery(id+"F0.imprint","INTERSECT",VERTEX,{"derivedFrom":[subQ3,subQ7]});var subQ10=sQuery(id+"F4.wireOp",EDGE,"E11.top");var subQ11=makeQuery(id+"F5.opExtrude","SWEPT_FACE",FACE,{"disambiguationData":[OSD([subQ10])]});Q0=makeQuery(id+"F5.boolean.opBoolean","SPLIT",FACE,{"disambiguationData":[TD([makeQuery(id+"F1.opExtrude","SWEPT_FACE",FACE,{"disambiguationData":[OSD([subQ3]),TDD([makeQuery(id+"F0.imprint","IMPRINT",EDGE,{"disambiguationData":[TD([[subQ8,-1.0]])],"derivedFrom":subQ3})])]})])],"derivedFrom":subQ11});}
            var sketch = newSketch(context, id + "F43", { "sketchPlane" : qUnion([Q0])});
            skLineSegment(sketch, "E67", {"start": v(50.8, 14.88) * mm, "end": v(21.04, 14.88) * mm});
            skLineSegment(sketch, "E68", {"start": v(21.04, 14.88) * mm, "end": v(0, -14.88) * mm});
            skLineSegment(sketch, "E69", {"start": v(0, -14.88) * mm, "end": v(50.8, -14.88) * mm});
            skLineSegment(sketch, "E70", {"start": v(50.8, -14.88) * mm, "end": v(50.8, 14.88) * mm});
            skLineSegment(sketch, "E71.0", {"start": v(47.24, 11.32) * mm, "end": v(22.88, 11.32) * mm});
            skLineSegment(sketch, "E71.1", {"start": v(47.24, -11.32) * mm, "end": v(47.24, 11.32) * mm});
            skLineSegment(sketch, "E71.2", {"start": v(6.87, -11.32) * mm, "end": v(47.24, -11.32) * mm});
            skLineSegment(sketch, "E71.3", {"start": v(22.88, 11.32) * mm, "end": v(6.87, -11.32) * mm});
            skSolve(sketch);
        }
        {
            var Q0;
            Q0=makeQuery(id+"F43.imprint","IMPRINT",FACE,{"disambiguationData":[TD([[makeQuery(id+"F43.imprint","IMPRINT",EDGE,{"derivedFrom":sQuery(id+"F43.wireOp",EDGE,"E71.0")}),1.0]])]});
            extrude(context, id + "F44", {"entities" : qUnion([Q0]), "operationType" : NewBodyOperationType.REMOVE, "oppositeDirection" : true, "depth" : 148.6 * mm, "offsetDistance" : 25.4 * mm});
        }
        {
            var Q0;
            {var subQ3=sQuery(id+"F0.wireOp",EDGE,"E0.right");var subQ5=sQuery(id+"F2.wireOp",EDGE,"E6.left");var subQ6=sQuery(id+"F2.wireOp",EDGE,"E6.top");var subQ7=makeQuery(id+"F2.imprint","INTERSECT",VERTEX,{"derivedFrom":[subQ6,subQ5]});var subQ10=makeQuery(id+"F3.opExtrude","SWEPT_FACE",FACE,{"disambiguationData":[OSD([subQ6]),TDD([makeQuery(id+"F2.imprint","IMPRINT",EDGE,{"disambiguationData":[TD([[subQ7,-1.0]])],"derivedFrom":subQ6})])]});var subQ11=sQuery(id+"F0.wireOp",EDGE,"E0.bottom");var subQ12=makeQuery(id+"F0.imprint","INTERSECT",VERTEX,{"derivedFrom":[subQ11,subQ3]});Q0=makeQuery(id+"F3.boolean.opBoolean","SPLIT",FACE,{"disambiguationData":[TD([makeQuery(id+"F1.opExtrude","SWEPT_FACE",FACE,{"disambiguationData":[OSD([subQ11]),TDD([makeQuery(id+"F0.imprint","IMPRINT",EDGE,{"disambiguationData":[TD([[subQ12,1.0]])],"derivedFrom":subQ11})])]})])],"derivedFrom":subQ10});}
            var sketch = newSketch(context, id + "F45", { "sketchPlane" : qUnion([Q0])});
            skLineSegment(sketch, "E72", {"start": v(-86.72, 0) * mm, "end": v(-86.72, -50.8) * mm});
            skLineSegment(sketch, "E73", {"start": v(-86.72, -50.8) * mm, "end": v(-56.96, -50.8) * mm});
            skLineSegment(sketch, "E74", {"start": v(-56.96, -50.8) * mm, "end": v(-56.96, -21.04) * mm});
            skLineSegment(sketch, "E75", {"start": v(-56.96, -21.04) * mm, "end": v(-86.72, 0) * mm});
            skLineSegment(sketch, "E76.0", {"start": v(-83.17, -6.87) * mm, "end": v(-83.17, -47.24) * mm});
            skLineSegment(sketch, "E76.1", {"start": v(-60.52, -22.88) * mm, "end": v(-83.17, -6.87) * mm});
            skLineSegment(sketch, "E76.2", {"start": v(-60.52, -47.24) * mm, "end": v(-60.52, -22.88) * mm});
            skLineSegment(sketch, "E76.3", {"start": v(-83.17, -47.24) * mm, "end": v(-60.52, -47.24) * mm});
            skSolve(sketch);
        }
        {
            var Q0;
            Q0=makeQuery(id+"F45.imprint","IMPRINT",FACE,{"disambiguationData":[TD([[makeQuery(id+"F45.imprint","IMPRINT",EDGE,{"derivedFrom":sQuery(id+"F45.wireOp",EDGE,"E76.0")}),1.0]])]});
            extrude(context, id + "F46", {"entities" : qUnion([Q0]), "operationType" : NewBodyOperationType.REMOVE, "oppositeDirection" : true, "depth" : 138.18 * mm, "offsetDistance" : 25.4 * mm});
        }
        {
            var Q0;
            {var subQ3=sQuery(id+"F0.wireOp",EDGE,"E0.right");var subQ5=sQuery(id+"F0.wireOp",EDGE,"E0.top");var subQ6=makeQuery(id+"F0.imprint","INTERSECT",VERTEX,{"derivedFrom":[subQ5,subQ3]});var subQ7=sQuery(id+"F2.wireOp",EDGE,"E6.left");var subQ8=sQuery(id+"F2.wireOp",EDGE,"E6.top");var subQ9=makeQuery(id+"F2.imprint","INTERSECT",VERTEX,{"derivedFrom":[subQ8,subQ7]});var subQ11=makeQuery(id+"F3.opExtrude","SWEPT_FACE",FACE,{"disambiguationData":[OSD([subQ8]),TDD([makeQuery(id+"F2.imprint","IMPRINT",EDGE,{"disambiguationData":[TD([[subQ9,-1.0]])],"derivedFrom":subQ8})])]});Q0=makeQuery(id+"F3.boolean.opBoolean","SPLIT",FACE,{"disambiguationData":[TD([makeQuery(id+"F1.opExtrude","SWEPT_FACE",FACE,{"disambiguationData":[OSD([subQ5]),TDD([makeQuery(id+"F0.imprint","IMPRINT",EDGE,{"disambiguationData":[TD([[subQ6,1.0]])],"derivedFrom":subQ5})])]})])],"derivedFrom":subQ11});}
            var sketch = newSketch(context, id + "F47", { "sketchPlane" : qUnion([Q0])});
            skLineSegment(sketch, "E77", {"start": v(-86.72, 0) * mm, "end": v(-86.72, 50.8) * mm});
            skLineSegment(sketch, "E78", {"start": v(-86.72, 50.8) * mm, "end": v(-56.96, 50.8) * mm});
            skLineSegment(sketch, "E79", {"start": v(-56.96, 50.8) * mm, "end": v(-56.96, 21.04) * mm});
            skLineSegment(sketch, "E80", {"start": v(-56.96, 21.04) * mm, "end": v(-86.72, 0) * mm});
            skLineSegment(sketch, "E81.0", {"start": v(-83.17, 6.87) * mm, "end": v(-83.17, 47.24) * mm});
            skLineSegment(sketch, "E81.1", {"start": v(-60.52, 22.88) * mm, "end": v(-83.17, 6.87) * mm});
            skLineSegment(sketch, "E81.2", {"start": v(-60.52, 47.24) * mm, "end": v(-60.52, 22.88) * mm});
            skLineSegment(sketch, "E81.3", {"start": v(-83.17, 47.24) * mm, "end": v(-60.52, 47.24) * mm});
            skSolve(sketch);
        }
        {
            var Q0;
            Q0=makeQuery(id+"F47.imprint","IMPRINT",FACE,{"disambiguationData":[TD([[makeQuery(id+"F47.imprint","IMPRINT",EDGE,{"derivedFrom":sQuery(id+"F47.wireOp",EDGE,"E81.0")}),-1.0]])]});
            extrude(context, id + "F48", {"entities" : qUnion([Q0]), "operationType" : NewBodyOperationType.REMOVE, "oppositeDirection" : true, "depth" : 137.92 * mm, "offsetDistance" : 25.4 * mm});
        }
        {
            var Q0;
            {var subQ3=sQuery(id+"F0.wireOp",EDGE,"E0.right");var subQ5=sQuery(id+"F0.wireOp",EDGE,"E0.top");var subQ6=makeQuery(id+"F0.imprint","INTERSECT",VERTEX,{"derivedFrom":[subQ5,subQ3]});var subQ7=sQuery(id+"F2.wireOp",EDGE,"E6.left");var subQ8=sQuery(id+"F2.wireOp",EDGE,"E6.top");var subQ9=makeQuery(id+"F2.imprint","INTERSECT",VERTEX,{"derivedFrom":[subQ8,subQ7]});var subQ11=makeQuery(id+"F3.opExtrude","SWEPT_FACE",FACE,{"disambiguationData":[OSD([subQ7]),TDD([makeQuery(id+"F2.imprint","IMPRINT",EDGE,{"disambiguationData":[TD([[subQ9,1.0]])],"derivedFrom":subQ7})])]});Q0=makeQuery(id+"F3.boolean.opBoolean","SPLIT",FACE,{"disambiguationData":[TD([makeQuery(id+"F1.opExtrude","SWEPT_FACE",FACE,{"disambiguationData":[OSD([subQ5]),TDD([makeQuery(id+"F0.imprint","IMPRINT",EDGE,{"disambiguationData":[TD([[subQ6,1.0]])],"derivedFrom":subQ5})])]})])],"derivedFrom":subQ11});}
            var sketch = newSketch(context, id + "F49", { "sketchPlane" : qUnion([Q0])});
            skLineSegment(sketch, "E82", {"start": v(0, -14.88) * mm, "end": v(21.04, 14.88) * mm});
            skLineSegment(sketch, "E83", {"start": v(21.04, 14.88) * mm, "end": v(50.8, 14.88) * mm});
            skLineSegment(sketch, "E84", {"start": v(50.8, 14.88) * mm, "end": v(50.8, -14.88) * mm});
            skLineSegment(sketch, "E85", {"start": v(50.8, -14.88) * mm, "end": v(0, -14.88) * mm});
            skLineSegment(sketch, "E86.0", {"start": v(6.87, -11.32) * mm, "end": v(22.88, 11.32) * mm});
            skLineSegment(sketch, "E86.1", {"start": v(47.24, -11.32) * mm, "end": v(6.87, -11.32) * mm});
            skLineSegment(sketch, "E86.2", {"start": v(47.24, 11.32) * mm, "end": v(47.24, -11.32) * mm});
            skLineSegment(sketch, "E86.3", {"start": v(22.88, 11.32) * mm, "end": v(47.24, 11.32) * mm});
            skSolve(sketch);
        }
        {
            var Q0;
            Q0=makeQuery(id+"F49.imprint","IMPRINT",FACE,{"disambiguationData":[TD([[makeQuery(id+"F49.imprint","IMPRINT",EDGE,{"derivedFrom":sQuery(id+"F49.wireOp",EDGE,"E86.0")}),-1.0]])]});
            extrude(context, id + "F50", {"entities" : qUnion([Q0]), "operationType" : NewBodyOperationType.REMOVE, "oppositeDirection" : true, "depth" : 160.53 * mm, "offsetDistance" : 25.4 * mm});
        }
        {
            var Q0;
            {var subQ3=sQuery(id+"F0.wireOp",EDGE,"E0.right");var subQ5=sQuery(id+"F2.wireOp",EDGE,"E6.left");var subQ6=sQuery(id+"F2.wireOp",EDGE,"E6.top");var subQ7=makeQuery(id+"F2.imprint","INTERSECT",VERTEX,{"derivedFrom":[subQ6,subQ5]});var subQ10=sQuery(id+"F0.wireOp",EDGE,"E0.bottom");var subQ11=makeQuery(id+"F0.imprint","INTERSECT",VERTEX,{"derivedFrom":[subQ10,subQ3]});var subQ12=makeQuery(id+"F3.opExtrude","SWEPT_FACE",FACE,{"disambiguationData":[OSD([subQ5]),TDD([makeQuery(id+"F2.imprint","IMPRINT",EDGE,{"disambiguationData":[TD([[subQ7,1.0]])],"derivedFrom":subQ5})])]});Q0=makeQuery(id+"F3.boolean.opBoolean","SPLIT",FACE,{"disambiguationData":[TD([makeQuery(id+"F1.opExtrude","SWEPT_FACE",FACE,{"disambiguationData":[OSD([subQ10]),TDD([makeQuery(id+"F0.imprint","IMPRINT",EDGE,{"disambiguationData":[TD([[subQ11,1.0]])],"derivedFrom":subQ10})])]})])],"derivedFrom":subQ12});}
            var sketch = newSketch(context, id + "F51", { "sketchPlane" : qUnion([Q0])});
            skLineSegment(sketch, "E87", {"start": v(0, -14.88) * mm, "end": v(-21.04, 14.88) * mm});
            skLineSegment(sketch, "E88", {"start": v(-21.04, 14.88) * mm, "end": v(-50.8, 14.88) * mm});
            skLineSegment(sketch, "E89", {"start": v(-50.8, 14.88) * mm, "end": v(-50.8, -14.88) * mm});
            skLineSegment(sketch, "E90", {"start": v(-50.8, -14.88) * mm, "end": v(0, -14.88) * mm});
            skLineSegment(sketch, "E91.0", {"start": v(-47.24, 11.32) * mm, "end": v(-47.24, -11.32) * mm});
            skLineSegment(sketch, "E91.1", {"start": v(-22.88, 11.32) * mm, "end": v(-47.24, 11.32) * mm});
            skLineSegment(sketch, "E91.2", {"start": v(-6.87, -11.32) * mm, "end": v(-22.88, 11.32) * mm});
            skLineSegment(sketch, "E91.3", {"start": v(-47.24, -11.32) * mm, "end": v(-6.87, -11.32) * mm});
            skSolve(sketch);
        }
        {
            var Q0;
            Q0=makeQuery(id+"F51.imprint","IMPRINT",FACE,{"disambiguationData":[TD([[makeQuery(id+"F51.imprint","IMPRINT",EDGE,{"derivedFrom":sQuery(id+"F51.wireOp",EDGE,"E91.0")}),1.0]])]});
            extrude(context, id + "F52", {"entities" : qUnion([Q0]), "operationType" : NewBodyOperationType.REMOVE, "oppositeDirection" : true, "depth" : 256.54 * mm, "offsetDistance" : 25.4 * mm});
        }
        {
            var Q0;
            {var subQ0=sQuery(id+"F0.wireOp",EDGE,"E5.left");var subQ1=sQuery(id+"F0.wireOp",EDGE,"E5.top");var subQ2=makeQuery(id+"F0.imprint","INTERSECT",VERTEX,{"derivedFrom":[subQ1,subQ0]});var subQ3=sQuery(id+"F0.wireOp",EDGE,"E0.right");var subQ7=sQuery(id+"F0.wireOp",EDGE,"E0.top");var subQ10=makeQuery(id+"F1.opExtrude","SWEPT_FACE",FACE,{"disambiguationData":[OSD([subQ1]),TDD([makeQuery(id+"F0.imprint","IMPRINT",EDGE,{"disambiguationData":[TD([[subQ2,-1.0]])],"derivedFrom":subQ1})])]});Q0=makeQuery(id+"F3.boolean.opBoolean","SPLIT",FACE,{"disambiguationData":[TD([makeQuery(id+"F1.opExtrude","CAP_FACE",FACE,{"disambiguationData":[OSD([sQuery(id+"F0.wireOp",EDGE,"E0.bottom"),subQ7,sQuery(id+"F0.wireOp",EDGE,"E0.left"),subQ3,sQuery(id+"F0.wireOp",EDGE,"E5.bottom"),subQ1,subQ0,sQuery(id+"F0.wireOp",EDGE,"E5.right")])],"isStart":false})])],"derivedFrom":subQ10});}
            var sketch = newSketch(context, id + "F53", { "sketchPlane" : qUnion([Q0])});
            skLineSegment(sketch, "E92.0", {"start": v(-47.24, 98.04) * mm, "end": v(-47.24, 57.67) * mm});
            skLineSegment(sketch, "E92.1", {"start": v(-24.6, 98.04) * mm, "end": v(-47.24, 98.04) * mm});
            skLineSegment(sketch, "E92.2", {"start": v(-24.6, 73.68) * mm, "end": v(-24.6, 98.04) * mm});
            skLineSegment(sketch, "E92.3", {"start": v(-47.24, 57.67) * mm, "end": v(-24.6, 73.68) * mm});
            skSolve(sketch);
        }
        {
            var Q0;
            Q0=makeQuery(id+"F53.imprint","IMPRINT",FACE,{"disambiguationData":[TD([[makeQuery(id+"F53.imprint","IMPRINT",EDGE,{"derivedFrom":sQuery(id+"F53.wireOp",EDGE,"E92.0")}),1.0]])]});
            extrude(context, id + "F54", {"entities" : qUnion([Q0]), "operationType" : NewBodyOperationType.REMOVE, "oppositeDirection" : true, "depth" : 227.84 * mm, "offsetDistance" : 25.4 * mm});
        }
        {
            var Q0;
            {var subQ0=sQuery(id+"F0.wireOp",EDGE,"E5.left");var subQ1=sQuery(id+"F0.wireOp",EDGE,"E5.top");var subQ2=makeQuery(id+"F0.imprint","INTERSECT",VERTEX,{"derivedFrom":[subQ1,subQ0]});var subQ3=sQuery(id+"F0.wireOp",EDGE,"E0.right");var subQ5=makeQuery(id+"F1.opExtrude","SWEPT_FACE",FACE,{"disambiguationData":[OSD([subQ0]),TDD([makeQuery(id+"F0.imprint","IMPRINT",EDGE,{"disambiguationData":[TD([[subQ2,1.0]])],"derivedFrom":subQ0})])]});var subQ9=sQuery(id+"F0.wireOp",EDGE,"E0.top");var subQ11=sQuery(id+"F0.wireOp",EDGE,"E0.bottom");Q0=makeQuery(id+"F3.boolean.opBoolean","SPLIT",FACE,{"disambiguationData":[TD([makeQuery(id+"F1.opExtrude","CAP_FACE",FACE,{"disambiguationData":[OSD([subQ11,subQ9,sQuery(id+"F0.wireOp",EDGE,"E0.left"),subQ3,sQuery(id+"F0.wireOp",EDGE,"E5.bottom"),subQ1,subQ0,sQuery(id+"F0.wireOp",EDGE,"E5.right")])],"isStart":false})])],"derivedFrom":subQ5});}
            var sketch = newSketch(context, id + "F55", { "sketchPlane" : qUnion([Q0])});
            skLineSegment(sketch, "E93.0", {"start": v(24.6, 98.04) * mm, "end": v(24.6, 73.68) * mm});
            skLineSegment(sketch, "E93.1", {"start": v(47.24, 98.04) * mm, "end": v(24.6, 98.04) * mm});
            skLineSegment(sketch, "E93.2", {"start": v(47.24, 57.67) * mm, "end": v(47.24, 98.04) * mm});
            skLineSegment(sketch, "E93.3", {"start": v(24.6, 73.68) * mm, "end": v(47.24, 57.67) * mm});
            skSolve(sketch);
        }
        {
            var Q0;
            Q0=makeQuery(id+"F55.imprint","IMPRINT",FACE,{"disambiguationData":[TD([[makeQuery(id+"F55.imprint","IMPRINT",EDGE,{"derivedFrom":sQuery(id+"F55.wireOp",EDGE,"E93.0")}),1.0]])]});
            extrude(context, id + "F56", {"entities" : qUnion([Q0]), "operationType" : NewBodyOperationType.REMOVE, "oppositeDirection" : true, "depth" : 169.42 * mm, "offsetDistance" : 25.4 * mm});
        }
        {
            var Q0;
            {var subQ0=sQuery(id+"F0.wireOp",EDGE,"E5.left");var subQ1=sQuery(id+"F0.wireOp",EDGE,"E5.top");var subQ2=makeQuery(id+"F0.imprint","INTERSECT",VERTEX,{"derivedFrom":[subQ1,subQ0]});var subQ3=sQuery(id+"F0.wireOp",EDGE,"E0.right");var subQ7=sQuery(id+"F0.wireOp",EDGE,"E0.top");var subQ10=makeQuery(id+"F1.opExtrude","SWEPT_FACE",FACE,{"disambiguationData":[OSD([subQ1]),TDD([makeQuery(id+"F0.imprint","IMPRINT",EDGE,{"disambiguationData":[TD([[subQ2,-1.0]])],"derivedFrom":subQ1})])]});Q0=makeQuery(id+"F3.boolean.opBoolean","SPLIT",FACE,{"disambiguationData":[TD([makeQuery(id+"F1.opExtrude","CAP_FACE",FACE,{"disambiguationData":[OSD([sQuery(id+"F0.wireOp",EDGE,"E0.bottom"),subQ7,sQuery(id+"F0.wireOp",EDGE,"E0.left"),subQ3,sQuery(id+"F0.wireOp",EDGE,"E5.bottom"),subQ1,subQ0,sQuery(id+"F0.wireOp",EDGE,"E5.right")])],"isStart":true})])],"derivedFrom":subQ10});}
            var sketch = newSketch(context, id + "F57", { "sketchPlane" : qUnion([Q0])});
            skLineSegment(sketch, "E94.0", {"start": v(-24.6, 3.56) * mm, "end": v(-24.6, 27.92) * mm});
            skLineSegment(sketch, "E94.1", {"start": v(-47.24, 3.56) * mm, "end": v(-24.6, 3.56) * mm});
            skLineSegment(sketch, "E94.2", {"start": v(-47.24, 43.93) * mm, "end": v(-47.24, 3.56) * mm});
            skLineSegment(sketch, "E94.3", {"start": v(-24.6, 27.92) * mm, "end": v(-47.24, 43.93) * mm});
            skSolve(sketch);
        }
        {
            var Q0;
            Q0=makeQuery(id+"F57.imprint","IMPRINT",FACE,{"disambiguationData":[TD([[makeQuery(id+"F57.imprint","IMPRINT",EDGE,{"derivedFrom":sQuery(id+"F57.wireOp",EDGE,"E94.0")}),1.0]])]});
            extrude(context, id + "F58", {"entities" : qUnion([Q0]), "operationType" : NewBodyOperationType.REMOVE, "oppositeDirection" : true, "depth" : 138.43 * mm, "offsetDistance" : 25.4 * mm});
        }
        {
            var Q0;
            {var subQ2=sQuery(id+"F0.wireOp",EDGE,"E0.bottom");var subQ4=sQuery(id+"F0.wireOp",EDGE,"E0.right");var subQ5=sQuery(id+"F2.wireOp",EDGE,"E6.left");var subQ7=sQuery(id+"F2.wireOp",EDGE,"E6.bottom");var subQ10=makeQuery(id+"F3.opExtrude","SWEPT_FACE",FACE,{"disambiguationData":[OSD([subQ5]),TDD([makeQuery(id+"F2.imprint","IMPRINT",EDGE,{"disambiguationData":[TD([[makeQuery(id+"F2.imprint","INTERSECT",VERTEX,{"derivedFrom":[subQ7,subQ5]}),-1.0]])],"derivedFrom":subQ5})])]});Q0=makeQuery(id+"F5.boolean.opBoolean","SPLIT",FACE,{"disambiguationData":[TD([makeQuery(id+"F1.opExtrude","SWEPT_FACE",FACE,{"disambiguationData":[OSD([subQ2]),TDD([makeQuery(id+"F0.imprint","IMPRINT",EDGE,{"disambiguationData":[TD([[makeQuery(id+"F0.imprint","INTERSECT",VERTEX,{"derivedFrom":[subQ2,subQ4]}),1.0]])],"derivedFrom":subQ2})])]})])],"derivedFrom":subQ10});}
            var sketch = newSketch(context, id + "F59", { "sketchPlane" : qUnion([Q0])});
            skLineSegment(sketch, "E95.0", {"start": v(-47.24, 60.52) * mm, "end": v(-22.88, 60.52) * mm});
            skLineSegment(sketch, "E95.1", {"start": v(-47.24, 83.17) * mm, "end": v(-47.24, 60.52) * mm});
            skLineSegment(sketch, "E95.2", {"start": v(-6.87, 83.17) * mm, "end": v(-47.24, 83.17) * mm});
            skLineSegment(sketch, "E95.3", {"start": v(-22.88, 60.52) * mm, "end": v(-6.87, 83.17) * mm});
            skSolve(sketch);
        }
        {
            var Q0;
            Q0=makeQuery(id+"F59.imprint","IMPRINT",FACE,{"disambiguationData":[TD([[makeQuery(id+"F59.imprint","IMPRINT",EDGE,{"derivedFrom":sQuery(id+"F59.wireOp",EDGE,"E95.0")}),1.0]])]});
            extrude(context, id + "F60", {"entities" : qUnion([Q0]), "operationType" : NewBodyOperationType.REMOVE, "oppositeDirection" : true, "depth" : 188.98 * mm, "offsetDistance" : 25.4 * mm});
        }
        {
            var Q0;
            {var subQ0=sQuery(id+"F2.wireOp",EDGE,"E6.bottom");var subQ3=sQuery(id+"F0.wireOp",EDGE,"E0.top");var subQ5=sQuery(id+"F0.wireOp",EDGE,"E0.right");var subQ6=sQuery(id+"F2.wireOp",EDGE,"E6.left");var subQ8=makeQuery(id+"F0.imprint","IMPRINT",EDGE,{"disambiguationData":[TD([[makeQuery(id+"F0.imprint","INTERSECT",VERTEX,{"derivedFrom":[subQ3,subQ5]}),1.0]])],"derivedFrom":subQ3});var subQ9=makeQuery(id+"F3.opExtrude","SWEPT_FACE",FACE,{"disambiguationData":[OSD([subQ6]),TDD([makeQuery(id+"F2.imprint","IMPRINT",EDGE,{"disambiguationData":[TD([[makeQuery(id+"F2.imprint","INTERSECT",VERTEX,{"derivedFrom":[subQ0,subQ6]}),-1.0]])],"derivedFrom":subQ6})])]});Q0=makeQuery(id+"F5.boolean.opBoolean","SPLIT",FACE,{"disambiguationData":[TD([makeQuery(id+"F1.opExtrude","SWEPT_FACE",FACE,{"disambiguationData":[OSD([subQ3]),TDD([subQ8])]})])],"derivedFrom":subQ9});}
            var sketch = newSketch(context, id + "F61", { "sketchPlane" : qUnion([Q0])});
            skLineSegment(sketch, "E96.0", {"start": v(47.24, 83.17) * mm, "end": v(6.87, 83.17) * mm});
            skLineSegment(sketch, "E96.1", {"start": v(47.24, 60.52) * mm, "end": v(47.24, 83.17) * mm});
            skLineSegment(sketch, "E96.2", {"start": v(22.88, 60.52) * mm, "end": v(47.24, 60.52) * mm});
            skLineSegment(sketch, "E96.3", {"start": v(6.87, 83.17) * mm, "end": v(22.88, 60.52) * mm});
            skSolve(sketch);
        }
        {
            var Q0;
            Q0=makeQuery(id+"F61.imprint","IMPRINT",FACE,{"disambiguationData":[TD([[makeQuery(id+"F61.imprint","IMPRINT",EDGE,{"derivedFrom":sQuery(id+"F61.wireOp",EDGE,"E96.0")}),1.0]])]});
            extrude(context, id + "F62", {"entities" : qUnion([Q0]), "operationType" : NewBodyOperationType.REMOVE, "oppositeDirection" : true, "depth" : 150.11 * mm, "offsetDistance" : 25.4 * mm});
        }
        {
            var Q0;
            {var subQ1=sQuery(id+"F0.wireOp",EDGE,"E5.left");var subQ2=sQuery(id+"F0.wireOp",EDGE,"E5.top");var subQ9=sQuery(id+"F4.wireOp",EDGE,"E11.top");var subQ10=makeQuery(id+"F5.opExtrude","SWEPT_FACE",FACE,{"disambiguationData":[OSD([subQ9])]});Q0=makeQuery(id+"F5.boolean.opBoolean","SPLIT",FACE,{"disambiguationData":[TD([makeQuery(id+"F1.opExtrude","SWEPT_FACE",FACE,{"disambiguationData":[OSD([subQ2]),TDD([makeQuery(id+"F0.imprint","IMPRINT",EDGE,{"disambiguationData":[TD([[makeQuery(id+"F0.imprint","INTERSECT",VERTEX,{"derivedFrom":[subQ2,subQ1]}),-1.0]])],"derivedFrom":subQ2})])]})])],"derivedFrom":subQ10});}
            var sketch = newSketch(context, id + "F63", { "sketchPlane" : qUnion([Q0])});
            skLineSegment(sketch, "E97.0", {"start": v(-47.24, 60.52) * mm, "end": v(-22.88, 60.52) * mm});
            skLineSegment(sketch, "E97.1", {"start": v(-47.24, 83.17) * mm, "end": v(-47.24, 60.52) * mm});
            skLineSegment(sketch, "E97.2", {"start": v(-6.87, 83.17) * mm, "end": v(-47.24, 83.17) * mm});
            skLineSegment(sketch, "E97.3", {"start": v(-22.88, 60.52) * mm, "end": v(-6.87, 83.17) * mm});
            skSolve(sketch);
        }
        {
            var Q0;
            Q0=makeQuery(id+"F63.imprint","IMPRINT",FACE,{"disambiguationData":[TD([[makeQuery(id+"F63.imprint","IMPRINT",EDGE,{"derivedFrom":sQuery(id+"F63.wireOp",EDGE,"E97.0")}),1.0]])]});
            extrude(context, id + "F64", {"entities" : qUnion([Q0]), "operationType" : NewBodyOperationType.REMOVE, "oppositeDirection" : true, "depth" : 147.57 * mm, "offsetDistance" : 25.4 * mm});
        }
        {
            var Q0;
            {var subQ1=sQuery(id+"F0.wireOp",EDGE,"E5.right");var subQ2=sQuery(id+"F0.wireOp",EDGE,"E5.bottom");var subQ5=sQuery(id+"F4.wireOp",EDGE,"E11.left");var subQ6=makeQuery(id+"F5.opExtrude","SWEPT_FACE",FACE,{"disambiguationData":[OSD([subQ5])]});Q0=makeQuery(id+"F5.boolean.opBoolean","SPLIT",FACE,{"disambiguationData":[TD([makeQuery(id+"F1.opExtrude","SWEPT_FACE",FACE,{"disambiguationData":[OSD([subQ2]),TDD([makeQuery(id+"F0.imprint","IMPRINT",EDGE,{"disambiguationData":[TD([[makeQuery(id+"F0.imprint","INTERSECT",VERTEX,{"derivedFrom":[subQ2,subQ1]}),1.0]])],"derivedFrom":subQ2})])]})])],"derivedFrom":subQ6});}
            var sketch = newSketch(context, id + "F65", { "sketchPlane" : qUnion([Q0])});
            skLineSegment(sketch, "E98.0", {"start": v(-47.24, 60.52) * mm, "end": v(-22.88, 60.52) * mm});
            skLineSegment(sketch, "E98.1", {"start": v(-47.24, 83.17) * mm, "end": v(-47.24, 60.52) * mm});
            skLineSegment(sketch, "E98.2", {"start": v(-6.87, 83.17) * mm, "end": v(-47.24, 83.17) * mm});
            skLineSegment(sketch, "E98.3", {"start": v(-22.88, 60.52) * mm, "end": v(-6.87, 83.17) * mm});
            skSolve(sketch);
        }
        {
            var Q0;
            Q0=makeQuery(id+"F65.imprint","IMPRINT",FACE,{"disambiguationData":[TD([[makeQuery(id+"F65.imprint","IMPRINT",EDGE,{"derivedFrom":sQuery(id+"F65.wireOp",EDGE,"E98.0")}),1.0]])]});
            extrude(context, id + "F66", {"entities" : qUnion([Q0]), "operationType" : NewBodyOperationType.REMOVE, "oppositeDirection" : true, "depth" : 134.87 * mm, "offsetDistance" : 25.4 * mm});
        }
        {
            var Q0;
            {var subQ1=sQuery(id+"F0.wireOp",EDGE,"E5.right");var subQ2=sQuery(id+"F0.wireOp",EDGE,"E5.bottom");var subQ11=sQuery(id+"F4.wireOp",EDGE,"E11.top");var subQ12=makeQuery(id+"F5.opExtrude","SWEPT_FACE",FACE,{"disambiguationData":[OSD([subQ11])]});Q0=makeQuery(id+"F5.boolean.opBoolean","SPLIT",FACE,{"disambiguationData":[TD([makeQuery(id+"F1.opExtrude","SWEPT_FACE",FACE,{"disambiguationData":[OSD([subQ1]),TDD([makeQuery(id+"F0.imprint","IMPRINT",EDGE,{"disambiguationData":[TD([[makeQuery(id+"F0.imprint","INTERSECT",VERTEX,{"derivedFrom":[subQ2,subQ1]}),-1.0]])],"derivedFrom":subQ1})])]})])],"derivedFrom":subQ12});}
            var sketch = newSketch(context, id + "F67", { "sketchPlane" : qUnion([Q0])});
            skLineSegment(sketch, "E99.0", {"start": v(22.88, 60.52) * mm, "end": v(47.24, 60.52) * mm});
            skLineSegment(sketch, "E99.1", {"start": v(6.87, 83.17) * mm, "end": v(22.88, 60.52) * mm});
            skLineSegment(sketch, "E99.2", {"start": v(47.24, 83.17) * mm, "end": v(6.87, 83.17) * mm});
            skLineSegment(sketch, "E99.3", {"start": v(47.24, 60.52) * mm, "end": v(47.24, 83.17) * mm});
            skSolve(sketch);
        }
        {
            var Q0;
            Q0=makeQuery(id+"F67.imprint","IMPRINT",FACE,{"disambiguationData":[TD([[makeQuery(id+"F67.imprint","IMPRINT",EDGE,{"derivedFrom":sQuery(id+"F67.wireOp",EDGE,"E99.0")}),1.0]])]});
            extrude(context, id + "F68", {"entities" : qUnion([Q0]), "operationType" : NewBodyOperationType.REMOVE, "oppositeDirection" : true, "depth" : 172.97 * mm, "offsetDistance" : 25.4 * mm});
        }
        {
            var Q0;
            {var subQ0=sQuery(id+"F0.wireOp",EDGE,"E5.right");var subQ1=sQuery(id+"F0.wireOp",EDGE,"E5.top");var subQ2=makeQuery(id+"F0.imprint","INTERSECT",VERTEX,{"derivedFrom":[subQ1,subQ0]});var subQ5=makeQuery(id+"F1.opExtrude","SWEPT_FACE",FACE,{"disambiguationData":[OSD([subQ1]),TDD([makeQuery(id+"F0.imprint","IMPRINT",EDGE,{"disambiguationData":[TD([[subQ2,1.0]])],"derivedFrom":subQ1})])]});var subQ7=sQuery(id+"F2.wireOp",EDGE,"E6.left");var subQ9=sQuery(id+"F2.wireOp",EDGE,"E6.bottom");Q0=makeQuery(id+"F5.boolean.opBoolean","SPLIT",FACE,{"disambiguationData":[TD([makeQuery(id+"F3.opExtrude","SWEPT_FACE",FACE,{"disambiguationData":[OSD([subQ7]),TDD([makeQuery(id+"F2.imprint","IMPRINT",EDGE,{"disambiguationData":[TD([[makeQuery(id+"F2.imprint","INTERSECT",VERTEX,{"derivedFrom":[subQ9,subQ7]}),-1.0]])],"derivedFrom":subQ7})])]})])],"derivedFrom":subQ5});}
            var sketch = newSketch(context, id + "F69", { "sketchPlane" : qUnion([Q0])});
            skLineSegment(sketch, "E100.0", {"start": v(24.6, 73.68) * mm, "end": v(47.24, 57.67) * mm});
            skLineSegment(sketch, "E100.1", {"start": v(24.6, 98.04) * mm, "end": v(24.6, 73.68) * mm});
            skLineSegment(sketch, "E100.2", {"start": v(47.24, 98.04) * mm, "end": v(24.6, 98.04) * mm});
            skLineSegment(sketch, "E100.3", {"start": v(47.24, 57.67) * mm, "end": v(47.24, 98.04) * mm});
            skSolve(sketch);
        }
        {
            var Q0;
            Q0=makeQuery(id+"F69.imprint","IMPRINT",FACE,{"disambiguationData":[TD([[makeQuery(id+"F69.imprint","IMPRINT",EDGE,{"derivedFrom":sQuery(id+"F69.wireOp",EDGE,"E100.0")}),1.0]])]});
            extrude(context, id + "F70", {"entities" : qUnion([Q0]), "operationType" : NewBodyOperationType.REMOVE, "oppositeDirection" : true, "depth" : 182.37 * mm, "offsetDistance" : 25.4 * mm});
        }
        {
            var Q0;
            {var subQ3=sQuery(id+"F0.wireOp",EDGE,"E0.left");var subQ5=sQuery(id+"F0.wireOp",EDGE,"E0.bottom");var subQ6=makeQuery(id+"F0.imprint","INTERSECT",VERTEX,{"derivedFrom":[subQ5,subQ3]});var subQ7=sQuery(id+"F2.wireOp",EDGE,"E6.bottom");var subQ8=makeQuery(id+"F3.opExtrude","SWEPT_FACE",FACE,{"disambiguationData":[OSD([subQ7])]});Q0=makeQuery(id+"F3.boolean.opBoolean","SPLIT",FACE,{"disambiguationData":[TD([makeQuery(id+"F1.opExtrude","SWEPT_FACE",FACE,{"disambiguationData":[OSD([subQ3]),TDD([makeQuery(id+"F0.imprint","IMPRINT",EDGE,{"disambiguationData":[TD([[subQ6,-1.0]])],"derivedFrom":subQ3})])]})])],"derivedFrom":subQ8});}
            var sketch = newSketch(context, id + "F71", { "sketchPlane" : qUnion([Q0])});
            skLineSegment(sketch, "E101.0", {"start": v(22.88, 11.32) * mm, "end": v(6.87, -11.32) * mm});
            skLineSegment(sketch, "E101.1", {"start": v(47.24, 11.32) * mm, "end": v(22.88, 11.32) * mm});
            skLineSegment(sketch, "E101.2", {"start": v(47.24, -11.32) * mm, "end": v(47.24, 11.32) * mm});
            skLineSegment(sketch, "E101.3", {"start": v(6.87, -11.32) * mm, "end": v(47.24, -11.32) * mm});
            skSolve(sketch);
        }
        {
            var Q0;
            Q0=makeQuery(id+"F71.imprint","IMPRINT",FACE,{"disambiguationData":[TD([[makeQuery(id+"F71.imprint","IMPRINT",EDGE,{"derivedFrom":sQuery(id+"F71.wireOp",EDGE,"E101.0")}),1.0]])]});
            extrude(context, id + "F72", {"entities" : qUnion([Q0]), "operationType" : NewBodyOperationType.REMOVE, "oppositeDirection" : true, "depth" : 139.2 * mm, "offsetDistance" : 25.4 * mm});
        }
        {
            var Q0;
            {var subQ0=sQuery(id+"F0.wireOp",EDGE,"E5.right");var subQ1=sQuery(id+"F0.wireOp",EDGE,"E5.bottom");var subQ2=makeQuery(id+"F0.imprint","INTERSECT",VERTEX,{"derivedFrom":[subQ1,subQ0]});var subQ3=sQuery(id+"F0.wireOp",EDGE,"E0.left");var subQ5=makeQuery(id+"F1.opExtrude","SWEPT_FACE",FACE,{"disambiguationData":[OSD([subQ0]),TDD([makeQuery(id+"F0.imprint","IMPRINT",EDGE,{"disambiguationData":[TD([[subQ2,-1.0]])],"derivedFrom":subQ0})])]});var subQ6=sQuery(id+"F0.wireOp",EDGE,"E0.top");Q0=makeQuery(id+"F3.boolean.opBoolean","SPLIT",FACE,{"disambiguationData":[TD([makeQuery(id+"F1.opExtrude","CAP_FACE",FACE,{"disambiguationData":[OSD([sQuery(id+"F0.wireOp",EDGE,"E0.bottom"),subQ6,subQ3,sQuery(id+"F0.wireOp",EDGE,"E0.right"),subQ1,sQuery(id+"F0.wireOp",EDGE,"E5.top"),sQuery(id+"F0.wireOp",EDGE,"E5.left"),subQ0])],"isStart":false})])],"derivedFrom":subQ5});}
            var sketch = newSketch(context, id + "F73", { "sketchPlane" : qUnion([Q0])});
            skLineSegment(sketch, "E102.0", {"start": v(24.6, 98.04) * mm, "end": v(24.6, 73.68) * mm});
            skLineSegment(sketch, "E102.1", {"start": v(47.24, 98.04) * mm, "end": v(24.6, 98.04) * mm});
            skLineSegment(sketch, "E102.2", {"start": v(47.24, 57.67) * mm, "end": v(47.24, 98.04) * mm});
            skLineSegment(sketch, "E102.3", {"start": v(24.6, 73.68) * mm, "end": v(47.24, 57.67) * mm});
            skSolve(sketch);
        }
        {
            var Q0;
            Q0=makeQuery(id+"F73.imprint","IMPRINT",FACE,{"disambiguationData":[TD([[makeQuery(id+"F73.imprint","IMPRINT",EDGE,{"derivedFrom":sQuery(id+"F73.wireOp",EDGE,"E102.0")}),1.0]])]});
            extrude(context, id + "F74", {"entities" : qUnion([Q0]), "operationType" : NewBodyOperationType.REMOVE, "oppositeDirection" : true, "depth" : 185.42 * mm, "offsetDistance" : 25.4 * mm});
        }
        {
            var Q0;
            {var subQ3=sQuery(id+"F0.wireOp",EDGE,"E0.left");var subQ5=sQuery(id+"F0.wireOp",EDGE,"E0.top");var subQ6=makeQuery(id+"F0.imprint","INTERSECT",VERTEX,{"derivedFrom":[subQ5,subQ3]});var subQ7=sQuery(id+"F2.wireOp",EDGE,"E6.bottom");var subQ8=makeQuery(id+"F3.opExtrude","SWEPT_FACE",FACE,{"disambiguationData":[OSD([subQ7])]});Q0=makeQuery(id+"F3.boolean.opBoolean","SPLIT",FACE,{"disambiguationData":[TD([makeQuery(id+"F1.opExtrude","SWEPT_FACE",FACE,{"disambiguationData":[OSD([subQ3]),TDD([makeQuery(id+"F0.imprint","IMPRINT",EDGE,{"disambiguationData":[TD([[subQ6,1.0]])],"derivedFrom":subQ3})])]})])],"derivedFrom":subQ8});}
            var sketch = newSketch(context, id + "F75", { "sketchPlane" : qUnion([Q0])});
            skLineSegment(sketch, "E103.0", {"start": v(-22.88, 11.32) * mm, "end": v(-47.24, 11.32) * mm});
            skLineSegment(sketch, "E103.1", {"start": v(-6.87, -11.32) * mm, "end": v(-22.88, 11.32) * mm});
            skLineSegment(sketch, "E103.2", {"start": v(-47.24, -11.32) * mm, "end": v(-6.87, -11.32) * mm});
            skLineSegment(sketch, "E103.3", {"start": v(-47.24, 11.32) * mm, "end": v(-47.24, -11.32) * mm});
            skSolve(sketch);
        }
        {
            var Q0;
            Q0=makeQuery(id+"F75.imprint","IMPRINT",FACE,{"disambiguationData":[TD([[makeQuery(id+"F75.imprint","IMPRINT",EDGE,{"derivedFrom":sQuery(id+"F75.wireOp",EDGE,"E103.0")}),1.0]])]});
            extrude(context, id + "F76", {"entities" : qUnion([Q0]), "operationType" : NewBodyOperationType.REMOVE, "oppositeDirection" : true, "depth" : 143.5 * mm, "offsetDistance" : 25.4 * mm});
        }
        {
            var Q0;
            {var subQ6=sQuery(id+"F0.wireOp",EDGE,"E5.right");var subQ8=sQuery(id+"F0.wireOp",EDGE,"E5.bottom");var subQ12=sQuery(id+"F4.wireOp",EDGE,"E11.right");var subQ13=makeQuery(id+"F5.opExtrude","SWEPT_FACE",FACE,{"disambiguationData":[OSD([subQ12])]});Q0=makeQuery(id+"F5.boolean.opBoolean","SPLIT",FACE,{"disambiguationData":[TD([makeQuery(id+"F1.opExtrude","SWEPT_FACE",FACE,{"disambiguationData":[OSD([subQ6]),TDD([makeQuery(id+"F0.imprint","IMPRINT",EDGE,{"disambiguationData":[TD([[makeQuery(id+"F0.imprint","INTERSECT",VERTEX,{"derivedFrom":[subQ8,subQ6]}),-1.0]])],"derivedFrom":subQ6})])]})])],"derivedFrom":subQ13});}
            var sketch = newSketch(context, id + "F77", { "sketchPlane" : qUnion([Q0])});
            skLineSegment(sketch, "E104.0", {"start": v(47.24, 11.32) * mm, "end": v(22.88, 11.32) * mm});
            skLineSegment(sketch, "E104.1", {"start": v(47.24, -11.32) * mm, "end": v(47.24, 11.32) * mm});
            skLineSegment(sketch, "E104.2", {"start": v(6.87, -11.32) * mm, "end": v(47.24, -11.32) * mm});
            skLineSegment(sketch, "E104.3", {"start": v(22.88, 11.32) * mm, "end": v(6.87, -11.32) * mm});
            skSolve(sketch);
        }
        {
            var Q0;
            Q0=makeQuery(id+"F77.imprint","IMPRINT",FACE,{"disambiguationData":[TD([[makeQuery(id+"F77.imprint","IMPRINT",EDGE,{"derivedFrom":sQuery(id+"F77.wireOp",EDGE,"E104.0")}),1.0]])]});
            extrude(context, id + "F78", {"entities" : qUnion([Q0]), "operationType" : NewBodyOperationType.REMOVE, "oppositeDirection" : true, "depth" : 177.04 * mm, "offsetDistance" : 25.4 * mm});
        }
        {
            var Q0;
            {var subQ0=sQuery(id+"F0.wireOp",EDGE,"E5.left");var subQ1=sQuery(id+"F0.wireOp",EDGE,"E5.top");var subQ2=makeQuery(id+"F0.imprint","INTERSECT",VERTEX,{"derivedFrom":[subQ1,subQ0]});var subQ8=sQuery(id+"F4.wireOp",EDGE,"E11.right");var subQ9=makeQuery(id+"F5.opExtrude","SWEPT_FACE",FACE,{"disambiguationData":[OSD([subQ8])]});Q0=makeQuery(id+"F5.boolean.opBoolean","SPLIT",FACE,{"disambiguationData":[TD([makeQuery(id+"F1.opExtrude","SWEPT_FACE",FACE,{"disambiguationData":[OSD([subQ1]),TDD([makeQuery(id+"F0.imprint","IMPRINT",EDGE,{"disambiguationData":[TD([[subQ2,-1.0]])],"derivedFrom":subQ1})])]})])],"derivedFrom":subQ9});}
            var sketch = newSketch(context, id + "F79", { "sketchPlane" : qUnion([Q0])});
            skLineSegment(sketch, "E105.0", {"start": v(-22.88, 11.32) * mm, "end": v(-47.24, 11.32) * mm});
            skLineSegment(sketch, "E105.1", {"start": v(-6.87, -11.32) * mm, "end": v(-22.88, 11.32) * mm});
            skLineSegment(sketch, "E105.2", {"start": v(-47.24, -11.32) * mm, "end": v(-6.87, -11.32) * mm});
            skLineSegment(sketch, "E105.3", {"start": v(-47.24, 11.32) * mm, "end": v(-47.24, -11.32) * mm});
            skSolve(sketch);
        }
        {
            var Q0;
            Q0=makeQuery(id+"F79.imprint","IMPRINT",FACE,{"disambiguationData":[TD([[makeQuery(id+"F79.imprint","IMPRINT",EDGE,{"derivedFrom":sQuery(id+"F79.wireOp",EDGE,"E105.0")}),1.0]])]});
            extrude(context, id + "F80", {"entities" : qUnion([Q0]), "operationType" : NewBodyOperationType.REMOVE, "oppositeDirection" : true, "depth" : 132.08 * mm, "offsetDistance" : 25.4 * mm});
        }
    });
